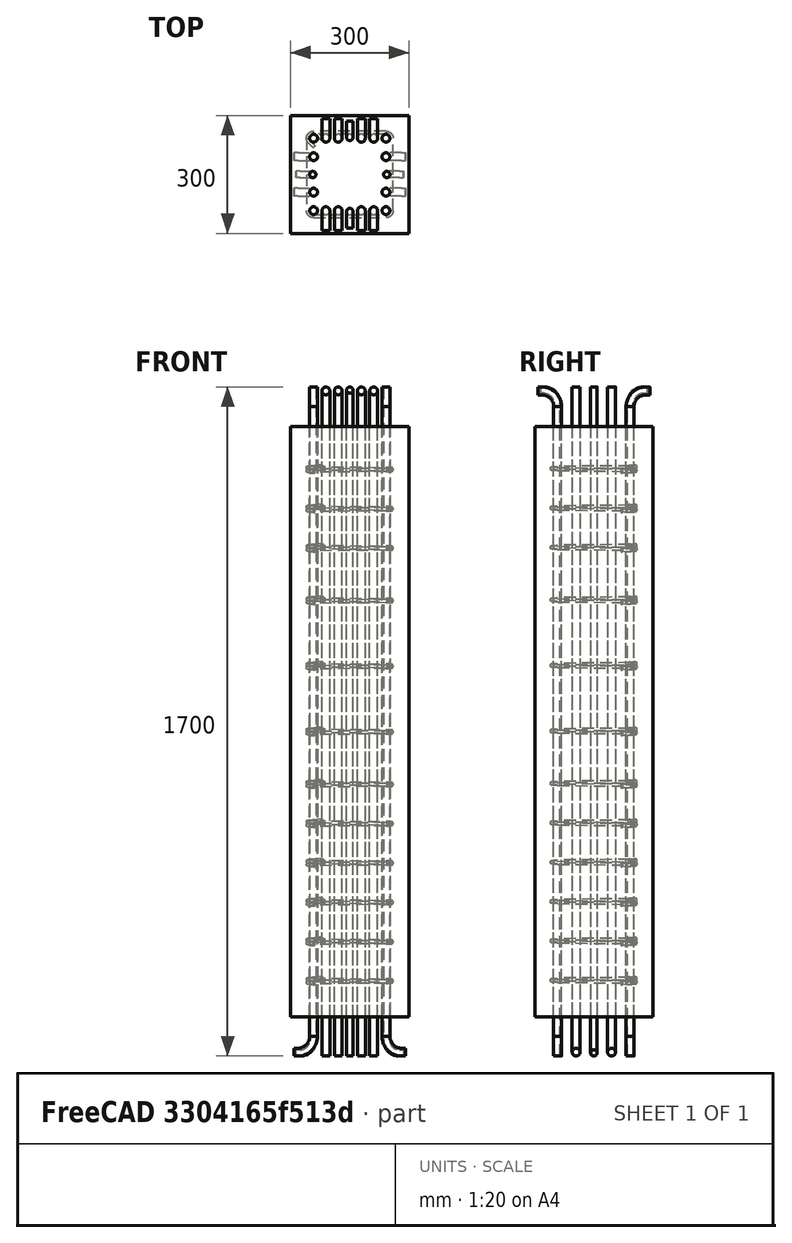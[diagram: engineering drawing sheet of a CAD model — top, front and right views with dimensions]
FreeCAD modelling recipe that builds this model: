
FCSTD DOCUMENT  (FreeCAD 0.19R20802 (Git))
Label: column_drawing_dimensioning
License: All rights reserved
LicenseURL: http://en.wikipedia.org/wiki/All_rights_reserved
objects: TechDraw::DrawViewSymbolPython×86, Part::FeaturePython×16, Sketcher::SketchObject×14, App::DocumentObjectGroupPython×6, TechDraw::DrawSVGTemplate×6, TechDraw::DrawPage×6, Part::Part2DObjectPython×1
note: 31 computed .brp shape members not serialized (recipe doc carries the construction recipe); baked Part::Feature solids carry a one-line shape summary decoded from their .brp

FEATURE [Part::FeaturePython] Structure  label="Column"  # Arch/BIM 24 (typed FeaturePython)
  FaceMaker = 0
  Height = 1500
  HorizontalArea = 90000
  IfcData = attributes={"GlobalId": {"name": "GlobalId", "type": "IfcGloballyUniqueId", "is_enum": false, "enum_values": []}, "Description": {"... (+438 chars omitted),+1 more (map truncated)
  IfcType = 24
  Length = 300
  MoveBase = false
  MoveWithHost = false
  Nodes = (2) [(5.55112e-16,1.51582e-15,0),(5.55112e-16,1.51582e-15,1500)]
  NodesOffset = 0
  Normal = (0,0,0)
  PerimeterLength = 1200
  PredefinedType = 0
  VerticalArea = 1800000
  Width = 300
FEATURE [Sketcher::SketchObject] Sketch
  MapMode = 5
  Placement = pos=(0,-150,0) rot=(1,0,0;1.5708rad)
  Support = -> [Structure]
  sketch-geometry (1):
    g0: LineSegment StartX=92 StartY=-50 StartZ=0 EndX=92 EndY=1550 EndZ=0
FEATURE [Part::FeaturePython] Rebar  label="StraightRebar"  # Arch/BIM 110 (typed FeaturePython)
  Amount = 2
  AmountCheck = true
  Base = -> Sketch
  Cover = 48
  CoverAlong = Right Side
  Diameter = 20
  Direction = (0,0,0)
  Distance = 0
  FrontCover = 48
  HorizontalArea = 0
  Host = -> Structure
  IfcType = 110
  LeftBottomCover = -50
  Length = 1600
  Mark = M
  MoveBase = false
  MoveWithHost = false
  OffsetEnd = 58
  OffsetStart = 58
  Orientation = Vertical
  PerimeterLength = 0
  PlacementList = 2 placements: [(0,58,-1.28786e-14),(0,242,-5.37348e-14)]
  RebarShape = 0
  RightTopCover = -50
  Rounding = 0
  Spacing = 184
  TotalLength = 3200
  TrueSpacing = 2
  VerticalArea = 0
FEATURE [Sketcher::SketchObject] Sketch001
  MapMode = 5
  Placement = pos=(0,-150,0) rot=(1,0,0;1.5708rad)
  Support = -> [Structure]
  sketch-geometry (1):
    g0: LineSegment StartX=-92 StartY=-50 StartZ=0 EndX=-92 EndY=1550 EndZ=0
FEATURE [Part::FeaturePython] Rebar001  label="StraightRebar001"  # Arch/BIM 110 (typed FeaturePython)
  Amount = 2
  AmountCheck = true
  Base = -> Sketch001
  Cover = 48
  CoverAlong = Left Side
  Diameter = 20
  Direction = (0,0,0)
  Distance = 0
  FrontCover = 48
  HorizontalArea = 0
  Host = -> Structure
  IfcType = 110
  LeftBottomCover = -50
  Length = 1600
  Mark = M
  MoveBase = false
  MoveWithHost = false
  OffsetEnd = 58
  OffsetStart = 58
  Orientation = Vertical
  PerimeterLength = 0
  PlacementList = 2 placements: [(0,58,-1.28786e-14),(0,242,-5.37348e-14)]
  RebarShape = 0
  RightTopCover = -50
  Rounding = 0
  Spacing = 184
  TotalLength = 3200
  TrueSpacing = 2
  VerticalArea = 0
FEATURE [Part::Part2DObjectPython] Wire  # Draft 2D object (typed FeaturePython)
  Area = 0
  ChamferSize = 0
  Closed = false
  End = (-90.5858,70.7868,1489.07)
  FilletRadius = 0
  Length = 987.335
  MakeFace = true
  Points = (7) [(-70.7868,90.5858,1502.19),(-106,125.799,1500),(-106,-106,1497.81),(106,-106,1495.63),(106,106,1493.44),(-125.799,106,1491.25),(-90.5858,70.7868,1489.07)]
  Start = (-70.7868,90.5858,1502.19)
  Subdivisions = 0
  Support = -> [Structure]
FEATURE [Part::FeaturePython] Rebar002  label="Stirrup"  # Arch/BIM 110 (typed FeaturePython)
  Amount = 12
  AmountCheck = true
  Base = -> Wire
  BentAngle = 135
  BentFactor = 2
  BottomCover = 40
  CustomSpacing = 3@100.0+3@166.66666666666666+6@100.0
  Diameter = 8
  Direction = (0,0,-1)
  Distance = 0
  FrontCover = 100
  HorizontalArea = 0
  Host = -> Structure
  IfcType = 110
  LeftCover = 40
  Length = 987.335
  Mark = Strp
  MoveBase = false
  MoveWithHost = false
  OffsetEnd = 104
  OffsetStart = 104
  PerimeterLength = 0
  PlacementList = 12 placements: [(0,0,-104),(0,0,-204),(0,0,-304),(0,0,-437.333),(0,0,-604),(0,0,-770.667),(0,0,-904),(0,0,-1004),(0,0,-1104),(0,0,-1204),(0,0,-1304),(0,0,-1404)]
  RebarShape = 3
  RightCover = 40
  Rounding = 1.75
  Spacing = 0
  TopCover = 40
  TotalLength = 11848
  TrueSpacing = 5
  VerticalArea = 0
FEATURE [App::DocumentObjectGroupPython] Ties  # scripted group (container) (typed FeaturePython)
  BottomCover = 40
  Group = -> [Rebar002]
  LeftCover = 40
  RightCover = 40
  Ties = -> [Rebar002]
  TiesConfiguration = SingleTie
  TopCover = 40
FEATURE [App::DocumentObjectGroupPython] MainRebars  # scripted group (container) (typed FeaturePython)
  BottomOffset = -50
  Group = -> [Rebar,Rebar001]
  HookExtendAlong = x-axis
  HookExtension = 40
  HookOrientation = Top Inside
  MainRebars = -> [Rebar,Rebar001]
  RebarType = StraightRebar
  TopOffset = -50
FEATURE [Sketcher::SketchObject] Sketch014
  MapMode = 5
  Placement = pos=(150,0,0) rot=(0.57735,0.57735,0.57735;2.0944rad)
  Support = -> [Structure]
  sketch-geometry (2):
    g0: LineSegment StartX=-92 StartY=-100 StartZ=0 EndX=-92 EndY=1590 EndZ=0
    g1: LineSegment StartX=-92 StartY=1590 StartZ=0 EndX=-142 EndY=1590 EndZ=0
FEATURE [Part::FeaturePython] Rebar015  label="LShapeRebar"  # Arch/BIM 110 (typed FeaturePython)
  Amount = 2
  AmountCheck = true
  Base = -> Sketch014
  BottomCover = -100
  Diameter = 20
  Direction = (0,0,0)
  Distance = 0
  FrontCover = 79.3333
  HorizontalArea = 0
  Host = -> Structure
  IfcType = 110
  LeftCover = 48
  Length = 1740
  Mark = XD
  MoveBase = false
  MoveWithHost = false
  OffsetEnd = 179.333
  OffsetStart = 89.3333
  Orientation = Top Left
  PerimeterLength = 0
  PlacementList = 2 placements: [(-89.3333,0,0),(-120.667,0,0)]
  RebarShape = 2
  RightCover = 292
  Rounding = 2
  Spacing = 31.3333
  TopCover = -100
  TotalLength = 3480
  TrueSpacing = 2
  VerticalArea = 0
FEATURE [Sketcher::SketchObject] Sketch015
  MapMode = 5
  Placement = pos=(150,0,0) rot=(0.57735,0.57735,0.57735;2.0944rad)
  Support = -> [Structure]
  sketch-geometry (2):
    g0: LineSegment StartX=-94 StartY=-100 StartZ=0 EndX=-94 EndY=1592 EndZ=0
    g1: LineSegment StartX=-94 StartY=1592 StartZ=0 EndX=-136 EndY=1592 EndZ=0
FEATURE [Part::FeaturePython] Rebar016  label="LShapeRebar001"  # Arch/BIM 110 (typed FeaturePython)
  Amount = 1
  AmountCheck = true
  Base = -> Sketch015
  BottomCover = -100
  Diameter = 16
  Direction = (0,0,0)
  Distance = 0
  FrontCover = 142
  HorizontalArea = 0
  Host = -> Structure
  IfcType = 110
  LeftCover = 48
  Length = 1734
  Mark = XD
  MoveBase = false
  MoveWithHost = false
  OffsetEnd = 150
  OffsetStart = 150
  Orientation = Top Left
  PerimeterLength = 0
  PlacementList = 1 placements: [(-150,0,0)]
  RebarShape = 2
  RightCover = 286
  Rounding = 2
  Spacing = 0
  TopCover = -100
  TotalLength = 1734
  TrueSpacing = 1
  VerticalArea = 0
FEATURE [Sketcher::SketchObject] Sketch016
  MapMode = 5
  Placement = pos=(150,0,0) rot=(0.57735,0.57735,0.57735;2.0944rad)
  Support = -> [Structure]
  sketch-geometry (2):
    g0: LineSegment StartX=-92 StartY=-100 StartZ=0 EndX=-92 EndY=1590 EndZ=0
    g1: LineSegment StartX=-92 StartY=1590 StartZ=0 EndX=-142 EndY=1590 EndZ=0
FEATURE [Part::FeaturePython] Rebar017  label="LShapeRebar002"  # Arch/BIM 110 (typed FeaturePython)
  Amount = 2
  AmountCheck = true
  Base = -> Sketch016
  BottomCover = -100
  Diameter = 20
  Direction = (0,0,0)
  Distance = 0
  FrontCover = 169.333
  HorizontalArea = 0
  Host = -> Structure
  IfcType = 110
  LeftCover = 48
  Length = 1740
  Mark = XD
  MoveBase = false
  MoveWithHost = false
  OffsetEnd = 89.3333
  OffsetStart = 179.333
  Orientation = Top Left
  PerimeterLength = 0
  PlacementList = 2 placements: [(-179.333,0,0),(-210.667,0,0)]
  RebarShape = 2
  RightCover = 292
  Rounding = 2
  Spacing = 31.3333
  TopCover = -100
  TotalLength = 3480
  TrueSpacing = 2
  VerticalArea = 0
FEATURE [Sketcher::SketchObject] Sketch017
  MapMode = 5
  Placement = pos=(150,0,0) rot=(0.57735,0.57735,0.57735;2.0944rad)
  Support = -> [Structure]
  sketch-geometry (2):
    g0: LineSegment StartX=92 StartY=-100 StartZ=0 EndX=92 EndY=1590 EndZ=0
    g1: LineSegment StartX=92 StartY=1590 StartZ=0 EndX=142 EndY=1590 EndZ=0
FEATURE [Part::FeaturePython] Rebar018  label="LShapeRebar003"  # Arch/BIM 110 (typed FeaturePython)
  Amount = 2
  AmountCheck = true
  Base = -> Sketch017
  BottomCover = -100
  Diameter = 20
  Direction = (0,0,0)
  Distance = 0
  FrontCover = 79.3333
  HorizontalArea = 0
  Host = -> Structure
  IfcType = 110
  LeftCover = 292
  Length = 1740
  Mark = XD
  MoveBase = false
  MoveWithHost = false
  OffsetEnd = 179.333
  OffsetStart = 89.3333
  Orientation = Top Right
  PerimeterLength = 0
  PlacementList = 2 placements: [(-89.3333,0,0),(-120.667,0,0)]
  RebarShape = 2
  RightCover = 48
  Rounding = 2
  Spacing = 31.3333
  TopCover = -100
  TotalLength = 3480
  TrueSpacing = 2
  VerticalArea = 0
FEATURE [Sketcher::SketchObject] Sketch018
  MapMode = 5
  Placement = pos=(150,0,0) rot=(0.57735,0.57735,0.57735;2.0944rad)
  Support = -> [Structure]
  sketch-geometry (2):
    g0: LineSegment StartX=94 StartY=-100 StartZ=0 EndX=94 EndY=1592 EndZ=0
    g1: LineSegment StartX=94 StartY=1592 StartZ=0 EndX=136 EndY=1592 EndZ=0
FEATURE [Part::FeaturePython] Rebar019  label="LShapeRebar004"  # Arch/BIM 110 (typed FeaturePython)
  Amount = 1
  AmountCheck = true
  Base = -> Sketch018
  BottomCover = -100
  Diameter = 16
  Direction = (0,0,0)
  Distance = 0
  FrontCover = 142
  HorizontalArea = 0
  Host = -> Structure
  IfcType = 110
  LeftCover = 286
  Length = 1734
  Mark = XD
  MoveBase = false
  MoveWithHost = false
  OffsetEnd = 150
  OffsetStart = 150
  Orientation = Top Right
  PerimeterLength = 0
  PlacementList = 1 placements: [(-150,0,0)]
  RebarShape = 2
  RightCover = 48
  Rounding = 2
  Spacing = 0
  TopCover = -100
  TotalLength = 1734
  TrueSpacing = 1
  VerticalArea = 0
FEATURE [Sketcher::SketchObject] Sketch019
  MapMode = 5
  Placement = pos=(150,0,0) rot=(0.57735,0.57735,0.57735;2.0944rad)
  Support = -> [Structure]
  sketch-geometry (2):
    g0: LineSegment StartX=92 StartY=-100 StartZ=0 EndX=92 EndY=1590 EndZ=0
    g1: LineSegment StartX=92 StartY=1590 StartZ=0 EndX=142 EndY=1590 EndZ=0
FEATURE [Part::FeaturePython] Rebar020  label="LShapeRebar005"  # Arch/BIM 110 (typed FeaturePython)
  Amount = 2
  AmountCheck = true
  Base = -> Sketch019
  BottomCover = -100
  Diameter = 20
  Direction = (0,0,0)
  Distance = 0
  FrontCover = 169.333
  HorizontalArea = 0
  Host = -> Structure
  IfcType = 110
  LeftCover = 292
  Length = 1740
  Mark = XD
  MoveBase = false
  MoveWithHost = false
  OffsetEnd = 89.3333
  OffsetStart = 179.333
  Orientation = Top Right
  PerimeterLength = 0
  PlacementList = 2 placements: [(-179.333,0,0),(-210.667,0,0)]
  RebarShape = 2
  RightCover = 48
  Rounding = 2
  Spacing = 31.3333
  TopCover = -100
  TotalLength = 3480
  TrueSpacing = 2
  VerticalArea = 0
FEATURE [App::DocumentObjectGroupPython] XDirRebars  # scripted group (container) (typed FeaturePython)
  BottomOffset = -100
  Group = -> [Rebar015,Rebar016,Rebar017,Rebar018,Rebar019,Rebar020]
  HookExtension = 10
  HookOrientation = Top Outside
  NumberDiameter = 2#20mm+1#16mm+2#20mm
  RebarType = LShapeRebar
  TopOffset = -100
  XDirRebars = -> [Rebar015,Rebar016,Rebar017,Rebar018,Rebar019,Rebar020]
FEATURE [Sketcher::SketchObject] Sketch020
  MapMode = 5
  Placement = pos=(0,-150,0) rot=(1,0,0;1.5708rad)
  Support = -> [Structure]
  sketch-geometry (2):
    g0: LineSegment StartX=-92 StartY=1600 StartZ=0 EndX=-92 EndY=-90 EndZ=0
    g1: LineSegment StartX=-92 StartY=-90 StartZ=0 EndX=-142 EndY=-90 EndZ=0
FEATURE [Part::FeaturePython] Rebar021  label="LShapeRebar006"  # Arch/BIM 110 (typed FeaturePython)
  Amount = 1
  AmountCheck = true
  Base = -> Sketch020
  BottomCover = -100
  Diameter = 20
  Direction = (0,0,0)
  Distance = 0
  FrontCover = 95
  HorizontalArea = 0
  Host = -> Structure
  IfcType = 110
  LeftCover = 48
  Length = 1740
  Mark = YD
  MoveBase = false
  MoveWithHost = false
  OffsetEnd = 195
  OffsetStart = 105
  Orientation = Bottom Left
  PerimeterLength = 0
  PlacementList = 1 placements: [(0,105,-2.33147e-14)]
  RebarShape = 2
  RightCover = 292
  Rounding = 2
  Spacing = 0
  TopCover = -100
  TotalLength = 1740
  TrueSpacing = 1
  VerticalArea = 0
FEATURE [Sketcher::SketchObject] Sketch021
  MapMode = 5
  Placement = pos=(0,-150,0) rot=(1,0,0;1.5708rad)
  Support = -> [Structure]
  sketch-geometry (2):
    g0: LineSegment StartX=-94 StartY=1600 StartZ=0 EndX=-94 EndY=-92 EndZ=0
    g1: LineSegment StartX=-94 StartY=-92 StartZ=0 EndX=-136 EndY=-92 EndZ=0
FEATURE [Part::FeaturePython] Rebar022  label="LShapeRebar007"  # Arch/BIM 110 (typed FeaturePython)
  Amount = 1
  AmountCheck = true
  Base = -> Sketch021
  BottomCover = -100
  Diameter = 16
  Direction = (0,0,0)
  Distance = 0
  FrontCover = 142
  HorizontalArea = 0
  Host = -> Structure
  IfcType = 110
  LeftCover = 48
  Length = 1734
  Mark = YD
  MoveBase = false
  MoveWithHost = false
  OffsetEnd = 150
  OffsetStart = 150
  Orientation = Bottom Left
  PerimeterLength = 0
  PlacementList = 1 placements: [(0,150,-3.33067e-14)]
  RebarShape = 2
  RightCover = 286
  Rounding = 2
  Spacing = 0
  TopCover = -100
  TotalLength = 1734
  TrueSpacing = 1
  VerticalArea = 0
FEATURE [Sketcher::SketchObject] Sketch022
  MapMode = 5
  Placement = pos=(0,-150,0) rot=(1,0,0;1.5708rad)
  Support = -> [Structure]
  sketch-geometry (2):
    g0: LineSegment StartX=-92 StartY=1600 StartZ=0 EndX=-92 EndY=-90 EndZ=0
    g1: LineSegment StartX=-92 StartY=-90 StartZ=0 EndX=-142 EndY=-90 EndZ=0
FEATURE [Part::FeaturePython] Rebar023  label="LShapeRebar008"  # Arch/BIM 110 (typed FeaturePython)
  Amount = 1
  AmountCheck = true
  Base = -> Sketch022
  BottomCover = -100
  Diameter = 20
  Direction = (0,0,0)
  Distance = 0
  FrontCover = 185
  HorizontalArea = 0
  Host = -> Structure
  IfcType = 110
  LeftCover = 48
  Length = 1740
  Mark = YD
  MoveBase = false
  MoveWithHost = false
  OffsetEnd = 105
  OffsetStart = 195
  Orientation = Bottom Left
  PerimeterLength = 0
  PlacementList = 1 placements: [(0,195,-4.32987e-14)]
  RebarShape = 2
  RightCover = 292
  Rounding = 2
  Spacing = 0
  TopCover = -100
  TotalLength = 1740
  TrueSpacing = 1
  VerticalArea = 0
FEATURE [Sketcher::SketchObject] Sketch023
  MapMode = 5
  Placement = pos=(0,-150,0) rot=(1,0,0;1.5708rad)
  Support = -> [Structure]
  sketch-geometry (2):
    g0: LineSegment StartX=92 StartY=1600 StartZ=0 EndX=92 EndY=-90 EndZ=0
    g1: LineSegment StartX=92 StartY=-90 StartZ=0 EndX=142 EndY=-90 EndZ=0
FEATURE [Part::FeaturePython] Rebar024  label="LShapeRebar009"  # Arch/BIM 110 (typed FeaturePython)
  Amount = 1
  AmountCheck = true
  Base = -> Sketch023
  BottomCover = -100
  Diameter = 20
  Direction = (0,0,0)
  Distance = 0
  FrontCover = 95
  HorizontalArea = 0
  Host = -> Structure
  IfcType = 110
  LeftCover = 292
  Length = 1740
  Mark = YD
  MoveBase = false
  MoveWithHost = false
  OffsetEnd = 195
  OffsetStart = 105
  Orientation = Bottom Right
  PerimeterLength = 0
  PlacementList = 1 placements: [(0,105,-2.33147e-14)]
  RebarShape = 2
  RightCover = 48
  Rounding = 2
  Spacing = 0
  TopCover = -100
  TotalLength = 1740
  TrueSpacing = 1
  VerticalArea = 0
FEATURE [Sketcher::SketchObject] Sketch024
  MapMode = 5
  Placement = pos=(0,-150,0) rot=(1,0,0;1.5708rad)
  Support = -> [Structure]
  sketch-geometry (2):
    g0: LineSegment StartX=94 StartY=1600 StartZ=0 EndX=94 EndY=-92 EndZ=0
    g1: LineSegment StartX=94 StartY=-92 StartZ=0 EndX=136 EndY=-92 EndZ=0
FEATURE [Part::FeaturePython] Rebar025  label="LShapeRebar010"  # Arch/BIM 110 (typed FeaturePython)
  Amount = 1
  AmountCheck = true
  Base = -> Sketch024
  BottomCover = -100
  Diameter = 16
  Direction = (0,0,0)
  Distance = 0
  FrontCover = 142
  HorizontalArea = 0
  Host = -> Structure
  IfcType = 110
  LeftCover = 286
  Length = 1734
  Mark = YD
  MoveBase = false
  MoveWithHost = false
  OffsetEnd = 150
  OffsetStart = 150
  Orientation = Bottom Right
  PerimeterLength = 0
  PlacementList = 1 placements: [(0,150,-3.33067e-14)]
  RebarShape = 2
  RightCover = 48
  Rounding = 2
  Spacing = 0
  TopCover = -100
  TotalLength = 1734
  TrueSpacing = 1
  VerticalArea = 0
FEATURE [Sketcher::SketchObject] Sketch025
  MapMode = 5
  Placement = pos=(0,-150,0) rot=(1,0,0;1.5708rad)
  Support = -> [Structure]
  sketch-geometry (2):
    g0: LineSegment StartX=92 StartY=1600 StartZ=0 EndX=92 EndY=-90 EndZ=0
    g1: LineSegment StartX=92 StartY=-90 StartZ=0 EndX=142 EndY=-90 EndZ=0
FEATURE [Part::FeaturePython] Rebar026  label="LShapeRebar011"  # Arch/BIM 110 (typed FeaturePython)
  Amount = 1
  AmountCheck = true
  Base = -> Sketch025
  BottomCover = -100
  Diameter = 20
  Direction = (0,0,0)
  Distance = 0
  FrontCover = 185
  HorizontalArea = 0
  Host = -> Structure
  IfcType = 110
  LeftCover = 292
  Length = 1740
  Mark = YD
  MoveBase = false
  MoveWithHost = false
  OffsetEnd = 105
  OffsetStart = 195
  Orientation = Bottom Right
  PerimeterLength = 0
  PlacementList = 1 placements: [(0,195,-4.32987e-14)]
  RebarShape = 2
  RightCover = 48
  Rounding = 2
  Spacing = 0
  TopCover = -100
  TotalLength = 1740
  TrueSpacing = 1
  VerticalArea = 0
FEATURE [App::DocumentObjectGroupPython] YDirRebars  # scripted group (container) (typed FeaturePython)
  BottomOffset = -100
  Group = -> [Rebar021,Rebar022,Rebar023,Rebar024,Rebar025,Rebar026]
  HookExtension = 10
  HookOrientation = Bottom Outside
  NumberDiameter = 1#20mm+1#16mm+1#20mm
  RebarType = LShapeRebar
  TopOffset = -100
  YDirRebars = -> [Rebar021,Rebar022,Rebar023,Rebar024,Rebar025,Rebar026]
FEATURE [App::DocumentObjectGroupPython] SecondaryRebars  # scripted group (container) (typed FeaturePython)
  Group = -> [XDirRebars,YDirRebars]
  SecondaryRebars = -> [XDirRebars,YDirRebars]
FEATURE [App::DocumentObjectGroupPython] ColumnReinforcement  # scripted group (container) (typed FeaturePython)
  ColumnType = RectangularColumn
  Group = -> [Ties,MainRebars,SecondaryRebars]
  RebarGroups = -> [Ties,MainRebars,SecondaryRebars]
FEATURE [TechDraw::DrawSVGTemplate] Template
  Height = 210
  Orientation = 1
  Width = 297
FEATURE [TechDraw::DrawViewSymbolPython] ReinforcementDrawingView  label="Front View"  # drawing view (typed FeaturePython)
  DimensionBottomOffset = 58
  DimensionLeftOffset = 16
  DimensionRightOffset = 34
  DimensionTopOffset = 10
  Height = 1700
  LeftOffset = 136.147
  LockPosition = false
  MaxHeight = 210
  MaxWidth = 297
  MinBottomOffset = 50
  MinRightOffset = 20
  PositionType = 0
  Rebars = -> [Rebar,Rebar001,Rebar002,Rebar015,Rebar016,Rebar017,Rebar018,Rebar019,Rebar020,Rebar021,Rebar022,Rebar023,Rebar024,Rebar025,Rebar026]
  RebarsColorStyle = 0
  RebarsStrokeWidth = 0.35
  Rotation = 0
  Scale = 0.0882353
  ScaleType = 1
  Structure = -> Structure
  StructureColorStyle = 0
  StructureStrokeWidth = 0.5
  Symbol = <blob: 8015 chars omitted>
  Template = -> Template
  TopOffset = 10
  View = 0
  VisibleRebars = -> [Rebar002,Rebar015,Rebar016,Rebar017,Rebar018,Rebar019,Rebar020,Rebar021,Rebar022,Rebar024,Rebar025,Rebar,Rebar001]
  Width = 300
  X = 149.382
  Y = 125
  expr: LeftOffset = .Template.Width.Value / 2 - .Width.Value * .Scale / 2
FEATURE [TechDraw::DrawViewSymbolPython] ReinforcementDimensioning  # drawing view (typed FeaturePython)
  DimensionBottomOffset = 10
  DimensionFormat = %M %C⌀%D,span=%S
  DimensionLeftOffset = 10
  DimensionRightOffset = 10
  DimensionTopOffset = 10
  Font = DejaVu Sans
  FontSize = 3
  LineEndSymbol = 0
  LineMidPointSymbol = 1
  LineStartSymbol = 3
  LineStyle = 0
  LockPosition = false
  MultiRebar_LineEndSymbol = 0
  MultiRebar_LineStartSymbol = 0
  MultiRebar_OuterDimension = true
  MultiRebar_TextPositionType = 0
  ParentDrawingView = -> ReinforcementDrawingView
  Rebar = -> Rebar002
  Rotation = 0
  Scale = 0.0882353
  ScaleType = 2
  SingleRebar_LineEndSymbol = 0
  SingleRebar_LineStartSymbol = 3
  SingleRebar_OuterDimension = false
  SingleRebar_TextPositionType = 1
  StrokeWidth = 0.25
  Symbol = <blob: 5409 chars omitted>
  TextPositionType = 0
  WayPoints = (2) [(0,0,0),(50,0,0)]
  WayPointsType = 0
  X = 149.382
  Y = 125
FEATURE [TechDraw::DrawViewSymbolPython] ReinforcementDimensioning001  # drawing view (typed FeaturePython)
  DimensionBottomOffset = 10
  DimensionFormat = %M %C⌀%D,span=%S
  DimensionLeftOffset = 10
  DimensionRightOffset = 16
  DimensionTopOffset = 10
  Font = DejaVu Sans
  FontSize = 3
  LineEndSymbol = 0
  LineMidPointSymbol = 1
  LineStartSymbol = 3
  LineStyle = 0
  LockPosition = false
  MultiRebar_LineEndSymbol = 0
  MultiRebar_LineStartSymbol = 0
  MultiRebar_OuterDimension = true
  MultiRebar_TextPositionType = 0
  ParentDrawingView = -> ReinforcementDrawingView
  Rebar = -> Rebar015
  Rotation = 0
  Scale = 0.0882353
  ScaleType = 2
  SingleRebar_LineEndSymbol = 0
  SingleRebar_LineStartSymbol = 3
  SingleRebar_OuterDimension = false
  SingleRebar_TextPositionType = 1
  StrokeWidth = 0.25
  Symbol = <svg version="1.1" xmlns="http://www.w3.org/2000/svg" xmlns:xlink="http://www.w3.org/1999/xlink" xmlns:freecad="http://www.freecadweb.org/wiki/index.php?title=Svg_Namespace" width="300.0mm" height="1700.0mm" viewBox="0 0 300.0 1700.0"><g transform="translate(150.0, 1600.0)"><g><path d="M60.66666666666667 156.6666666666667 L60.66666666666667 213.33333333333337 L29.333333333333357 213.33333333333337 L29.333333333333357 156.6666666666667" style="stroke:#00007f;stroke-width:2.833333333333333;stroke-linecap:round;fill:none;" stroke-dasharray="" /><path d="M0,0 -8,-1.5 V1.5 L0,0" style="stroke:#00007f;fill:#00007f;stroke-width:2.833333333333333;stroke-linecap:round;stroke-linejoin:bevel;" transform="translate(60.66666666666667 156.6666666666667) rotate(-90.0 0 0)" /><g id="line_mid_points"><circle cx="0" cy="0" r="5.666666666666666" fill="#00007f" transform="translate(60.66666666666667 213.33333333333337) rotate(90.0 0 0)" /><circle cx="0" cy="0" r="5.666666666666666" fill="#00007f" transform="translate(29.333333333333357 213.33333333333337) rotate(180.0 0 0)" /></g><path d="M0,0 -8,-1.5 V1.5 L0,0" style="stroke:#00007f;fill:#00007f;stroke-width:2.833333333333333;stroke-linecap:round;stroke-linejoin:bevel;" transform="translate(29.333333333333357 156.6666666666667) rotate(-90.0 0 0)" /></g><text x="45.000000000000014" y="207.6666666666667" style="white-space:pre;" fill="#005400" font-family="DejaVu Sans" font-size="34.0" text-anchor="middle" dominant-baseline="baseline" xml:space="preserve" transform="rotate(-0.0 45.000000000000014 213.33333333333337)">XD 2⌀20,span=31</text></g></svg>
  TextPositionType = 0
  WayPoints = (2) [(0,0,0),(50,0,0)]
  WayPointsType = 0
  X = 149.382
  Y = 125
FEATURE [TechDraw::DrawViewSymbolPython] ReinforcementDimensioning002  # drawing view (typed FeaturePython)
  DimensionBottomOffset = 16
  DimensionFormat = %M %C⌀%D,span=%S
  DimensionLeftOffset = 10
  DimensionRightOffset = 16
  DimensionTopOffset = 10
  Font = DejaVu Sans
  FontSize = 3
  LineEndSymbol = 0
  LineMidPointSymbol = 1
  LineStartSymbol = 3
  LineStyle = 0
  LockPosition = false
  MultiRebar_LineEndSymbol = 0
  MultiRebar_LineStartSymbol = 0
  MultiRebar_OuterDimension = true
  MultiRebar_TextPositionType = 0
  ParentDrawingView = -> ReinforcementDrawingView
  Rebar = -> Rebar016
  Rotation = 0
  Scale = 0.0882353
  ScaleType = 2
  SingleRebar_LineEndSymbol = 0
  SingleRebar_LineStartSymbol = 3
  SingleRebar_OuterDimension = false
  SingleRebar_TextPositionType = 1
  StrokeWidth = 0.25
  Symbol = <svg version="1.1" xmlns="http://www.w3.org/2000/svg" xmlns:xlink="http://www.w3.org/1999/xlink" xmlns:freecad="http://www.freecadweb.org/wiki/index.php?title=Svg_Namespace" width="300.0mm" height="1700.0mm" viewBox="0 0 300.0 1700.0"><g transform="translate(150.0, 1600.0)"><g><path d="M331.3333333333333 -870.0 L0.0 -870.0" style="stroke:#00007f;stroke-width:2.833333333333333;stroke-linecap:round;fill:none;" stroke-dasharray="" /><g id="line_mid_points" /><path d="M0,0 -8,-1.5 V1.5 L0,0" style="stroke:#00007f;fill:#00007f;stroke-width:2.833333333333333;stroke-linecap:round;stroke-linejoin:bevel;" transform="translate(0.0 -870.0) rotate(180.0 0 0)" /></g><text x="331.3333333333333" y="-853.0" style="white-space:pre;" fill="#005400" font-family="DejaVu Sans" font-size="34.0" text-anchor="start" dominant-baseline="baseline" xml:space="preserve">XD 1⌀16,span=0</text></g></svg>
  TextPositionType = 0
  WayPoints = (2) [(0,0,0),(50,0,0)]
  WayPointsType = 0
  X = 149.382
  Y = 125
FEATURE [TechDraw::DrawViewSymbolPython] ReinforcementDimensioning003  # drawing view (typed FeaturePython)
  DimensionBottomOffset = 16
  DimensionFormat = %M %C⌀%D,span=%S
  DimensionLeftOffset = 10
  DimensionRightOffset = 22
  DimensionTopOffset = 10
  Font = DejaVu Sans
  FontSize = 3
  LineEndSymbol = 0
  LineMidPointSymbol = 1
  LineStartSymbol = 3
  LineStyle = 0
  LockPosition = false
  MultiRebar_LineEndSymbol = 0
  MultiRebar_LineStartSymbol = 0
  MultiRebar_OuterDimension = true
  MultiRebar_TextPositionType = 0
  ParentDrawingView = -> ReinforcementDrawingView
  Rebar = -> Rebar017
  Rotation = 0
  Scale = 0.0882353
  ScaleType = 2
  SingleRebar_LineEndSymbol = 0
  SingleRebar_LineStartSymbol = 3
  SingleRebar_OuterDimension = false
  SingleRebar_TextPositionType = 1
  StrokeWidth = 0.25
  Symbol = <svg version="1.1" xmlns="http://www.w3.org/2000/svg" xmlns:xlink="http://www.w3.org/1999/xlink" xmlns:freecad="http://www.freecadweb.org/wiki/index.php?title=Svg_Namespace" width="300.0mm" height="1700.0mm" viewBox="0 0 300.0 1700.0"><g transform="translate(150.0, 1600.0)"><g><path d="M-29.333333333333343 224.6666666666667 L-29.333333333333343 281.33333333333337 L-60.66666666666666 281.33333333333337 L-60.66666666666666 224.6666666666667" style="stroke:#00007f;stroke-width:2.833333333333333;stroke-linecap:round;fill:none;" stroke-dasharray="" /><path d="M0,0 -8,-1.5 V1.5 L0,0" style="stroke:#00007f;fill:#00007f;stroke-width:2.833333333333333;stroke-linecap:round;stroke-linejoin:bevel;" transform="translate(-29.333333333333343 224.6666666666667) rotate(-90.0 0 0)" /><g id="line_mid_points"><circle cx="0" cy="0" r="5.666666666666666" fill="#00007f" transform="translate(-29.333333333333343 281.33333333333337) rotate(90.0 0 0)" /><circle cx="0" cy="0" r="5.666666666666666" fill="#00007f" transform="translate(-60.66666666666666 281.33333333333337) rotate(180.0 0 0)" /></g><path d="M0,0 -8,-1.5 V1.5 L0,0" style="stroke:#00007f;fill:#00007f;stroke-width:2.833333333333333;stroke-linecap:round;stroke-linejoin:bevel;" transform="translate(-60.66666666666666 224.6666666666667) rotate(-90.0 0 0)" /></g><text x="-45.0" y="275.6666666666667" style="white-space:pre;" fill="#005400" font-family="DejaVu Sans" font-size="34.0" text-anchor="middle" dominant-baseline="baseline" xml:space="preserve" transform="rotate(-0.0 -45.0 281.33333333333337)">XD 2⌀20,span=31</text></g></svg>
  TextPositionType = 0
  WayPoints = (2) [(0,0,0),(50,0,0)]
  WayPointsType = 0
  X = 149.382
  Y = 125
FEATURE [TechDraw::DrawViewSymbolPython] ReinforcementDimensioning004  # drawing view (typed FeaturePython)
  DimensionBottomOffset = 22
  DimensionFormat = %M %C⌀%D,span=%S
  DimensionLeftOffset = 10
  DimensionRightOffset = 22
  DimensionTopOffset = 10
  Font = DejaVu Sans
  FontSize = 3
  LineEndSymbol = 0
  LineMidPointSymbol = 1
  LineStartSymbol = 3
  LineStyle = 0
  LockPosition = false
  MultiRebar_LineEndSymbol = 0
  MultiRebar_LineStartSymbol = 0
  MultiRebar_OuterDimension = true
  MultiRebar_TextPositionType = 0
  ParentDrawingView = -> ReinforcementDrawingView
  Rebar = -> Rebar018
  Rotation = 0
  Scale = 0.0882353
  ScaleType = 2
  SingleRebar_LineEndSymbol = 0
  SingleRebar_LineStartSymbol = 3
  SingleRebar_OuterDimension = false
  SingleRebar_TextPositionType = 1
  StrokeWidth = 0.25
  Symbol = <svg version="1.1" xmlns="http://www.w3.org/2000/svg" xmlns:xlink="http://www.w3.org/1999/xlink" xmlns:freecad="http://www.freecadweb.org/wiki/index.php?title=Svg_Namespace" width="300.0mm" height="1700.0mm" viewBox="0 0 300.0 1700.0"><g transform="translate(150.0, 1600.0)"><g><path d="M60.66666666666667 292.6666666666667 L60.66666666666667 349.33333333333337 L29.333333333333357 349.33333333333337 L29.333333333333357 292.6666666666667" style="stroke:#00007f;stroke-width:2.833333333333333;stroke-linecap:round;fill:none;" stroke-dasharray="" /><path d="M0,0 -8,-1.5 V1.5 L0,0" style="stroke:#00007f;fill:#00007f;stroke-width:2.833333333333333;stroke-linecap:round;stroke-linejoin:bevel;" transform="translate(60.66666666666667 292.6666666666667) rotate(-90.0 0 0)" /><g id="line_mid_points"><circle cx="0" cy="0" r="5.666666666666666" fill="#00007f" transform="translate(60.66666666666667 349.33333333333337) rotate(90.0 0 0)" /><circle cx="0" cy="0" r="5.666666666666666" fill="#00007f" transform="translate(29.333333333333357 349.33333333333337) rotate(180.0 0 0)" /></g><path d="M0,0 -8,-1.5 V1.5 L0,0" style="stroke:#00007f;fill:#00007f;stroke-width:2.833333333333333;stroke-linecap:round;stroke-linejoin:bevel;" transform="translate(29.333333333333357 292.6666666666667) rotate(-90.0 0 0)" /></g><text x="45.000000000000014" y="343.6666666666667" style="white-space:pre;" fill="#005400" font-family="DejaVu Sans" font-size="34.0" text-anchor="middle" dominant-baseline="baseline" xml:space="preserve" transform="rotate(-0.0 45.000000000000014 349.33333333333337)">XD 2⌀20,span=31</text></g></svg>
  TextPositionType = 0
  WayPoints = (2) [(0,0,0),(50,0,0)]
  WayPointsType = 0
  X = 149.382
  Y = 125
FEATURE [TechDraw::DrawViewSymbolPython] ReinforcementDimensioning005  # drawing view (typed FeaturePython)
  DimensionBottomOffset = 28
  DimensionFormat = %M %C⌀%D,span=%S
  DimensionLeftOffset = 10
  DimensionRightOffset = 22
  DimensionTopOffset = 10
  Font = DejaVu Sans
  FontSize = 3
  LineEndSymbol = 0
  LineMidPointSymbol = 1
  LineStartSymbol = 3
  LineStyle = 0
  LockPosition = false
  MultiRebar_LineEndSymbol = 0
  MultiRebar_LineStartSymbol = 0
  MultiRebar_OuterDimension = true
  MultiRebar_TextPositionType = 0
  ParentDrawingView = -> ReinforcementDrawingView
  Rebar = -> Rebar019
  Rotation = 0
  Scale = 0.0882353
  ScaleType = 2
  SingleRebar_LineEndSymbol = 0
  SingleRebar_LineStartSymbol = 3
  SingleRebar_OuterDimension = false
  SingleRebar_TextPositionType = 1
  StrokeWidth = 0.25
  Symbol = <svg version="1.1" xmlns="http://www.w3.org/2000/svg" xmlns:xlink="http://www.w3.org/1999/xlink" xmlns:freecad="http://www.freecadweb.org/wiki/index.php?title=Svg_Namespace" width="300.0mm" height="1700.0mm" viewBox="0 0 300.0 1700.0"><g transform="translate(150.0, 1600.0)"><g><path d="M399.3333333333333 -161.0 L0.0 -161.0" style="stroke:#00007f;stroke-width:2.833333333333333;stroke-linecap:round;fill:none;" stroke-dasharray="" /><g id="line_mid_points" /><path d="M0,0 -8,-1.5 V1.5 L0,0" style="stroke:#00007f;fill:#00007f;stroke-width:2.833333333333333;stroke-linecap:round;stroke-linejoin:bevel;" transform="translate(0.0 -161.0) rotate(180.0 0 0)" /></g><text x="399.3333333333333" y="-144.0" style="white-space:pre;" fill="#005400" font-family="DejaVu Sans" font-size="34.0" text-anchor="start" dominant-baseline="baseline" xml:space="preserve">XD 1⌀16,span=0</text></g></svg>
  TextPositionType = 0
  WayPoints = (2) [(0,0,0),(50,0,0)]
  WayPointsType = 0
  X = 149.382
  Y = 125
FEATURE [TechDraw::DrawViewSymbolPython] ReinforcementDimensioning006  # drawing view (typed FeaturePython)
  DimensionBottomOffset = 28
  DimensionFormat = %M %C⌀%D,span=%S
  DimensionLeftOffset = 10
  DimensionRightOffset = 28
  DimensionTopOffset = 10
  Font = DejaVu Sans
  FontSize = 3
  LineEndSymbol = 0
  LineMidPointSymbol = 1
  LineStartSymbol = 3
  LineStyle = 0
  LockPosition = false
  MultiRebar_LineEndSymbol = 0
  MultiRebar_LineStartSymbol = 0
  MultiRebar_OuterDimension = true
  MultiRebar_TextPositionType = 0
  ParentDrawingView = -> ReinforcementDrawingView
  Rebar = -> Rebar020
  Rotation = 0
  Scale = 0.0882353
  ScaleType = 2
  SingleRebar_LineEndSymbol = 0
  SingleRebar_LineStartSymbol = 3
  SingleRebar_OuterDimension = false
  SingleRebar_TextPositionType = 1
  StrokeWidth = 0.25
  Symbol = <svg version="1.1" xmlns="http://www.w3.org/2000/svg" xmlns:xlink="http://www.w3.org/1999/xlink" xmlns:freecad="http://www.freecadweb.org/wiki/index.php?title=Svg_Namespace" width="300.0mm" height="1700.0mm" viewBox="0 0 300.0 1700.0"><g transform="translate(150.0, 1600.0)"><g><path d="M-29.333333333333343 360.6666666666667 L-29.333333333333343 417.33333333333337 L-60.66666666666666 417.33333333333337 L-60.66666666666666 360.6666666666667" style="stroke:#00007f;stroke-width:2.833333333333333;stroke-linecap:round;fill:none;" stroke-dasharray="" /><path d="M0,0 -8,-1.5 V1.5 L0,0" style="stroke:#00007f;fill:#00007f;stroke-width:2.833333333333333;stroke-linecap:round;stroke-linejoin:bevel;" transform="translate(-29.333333333333343 360.6666666666667) rotate(-90.0 0 0)" /><g id="line_mid_points"><circle cx="0" cy="0" r="5.666666666666666" fill="#00007f" transform="translate(-29.333333333333343 417.33333333333337) rotate(90.0 0 0)" /><circle cx="0" cy="0" r="5.666666666666666" fill="#00007f" transform="translate(-60.66666666666666 417.33333333333337) rotate(180.0 0 0)" /></g><path d="M0,0 -8,-1.5 V1.5 L0,0" style="stroke:#00007f;fill:#00007f;stroke-width:2.833333333333333;stroke-linecap:round;stroke-linejoin:bevel;" transform="translate(-60.66666666666666 360.6666666666667) rotate(-90.0 0 0)" /></g><text x="-45.0" y="411.6666666666667" style="white-space:pre;" fill="#005400" font-family="DejaVu Sans" font-size="34.0" text-anchor="middle" dominant-baseline="baseline" xml:space="preserve" transform="rotate(-0.0 -45.0 417.33333333333337)">XD 2⌀20,span=31</text></g></svg>
  TextPositionType = 0
  WayPoints = (2) [(0,0,0),(50,0,0)]
  WayPointsType = 0
  X = 149.382
  Y = 125
FEATURE [TechDraw::DrawViewSymbolPython] ReinforcementDimensioning007  # drawing view (typed FeaturePython)
  DimensionBottomOffset = 34
  DimensionFormat = %M %C⌀%D,span=%S
  DimensionLeftOffset = 10
  DimensionRightOffset = 28
  DimensionTopOffset = 10
  Font = DejaVu Sans
  FontSize = 3
  LineEndSymbol = 0
  LineMidPointSymbol = 1
  LineStartSymbol = 3
  LineStyle = 0
  LockPosition = false
  MultiRebar_LineEndSymbol = 0
  MultiRebar_LineStartSymbol = 0
  MultiRebar_OuterDimension = true
  MultiRebar_TextPositionType = 0
  ParentDrawingView = -> ReinforcementDrawingView
  Rebar = -> Rebar021
  Rotation = 0
  Scale = 0.0882353
  ScaleType = 2
  SingleRebar_LineEndSymbol = 0
  SingleRebar_LineStartSymbol = 3
  SingleRebar_OuterDimension = false
  SingleRebar_TextPositionType = 1
  StrokeWidth = 0.25
  Symbol = <svg version="1.1" xmlns="http://www.w3.org/2000/svg" xmlns:xlink="http://www.w3.org/1999/xlink" xmlns:freecad="http://www.freecadweb.org/wiki/index.php?title=Svg_Namespace" width="300.0mm" height="1700.0mm" viewBox="0 0 300.0 1700.0"><g transform="translate(150.0, 1600.0)"><g><path d="M-95.0 485.33333333333337 L-95.0 90.00000000000003" style="stroke:#00007f;stroke-width:2.833333333333333;stroke-linecap:round;fill:none;" stroke-dasharray="" /><g id="line_mid_points" /><path d="M0,0 -8,-1.5 V1.5 L0,0" style="stroke:#00007f;fill:#00007f;stroke-width:2.833333333333333;stroke-linecap:round;stroke-linejoin:bevel;" transform="translate(-95.0 90.00000000000003) rotate(-90.0 0 0)" /></g><text x="-95.0" y="502.33333333333337" style="white-space:pre;" fill="#005400" font-family="DejaVu Sans" font-size="34.0" text-anchor="middle" dominant-baseline="baseline" xml:space="preserve">YD 1⌀20,span=0</text></g></svg>
  TextPositionType = 0
  WayPoints = (2) [(0,0,0),(50,0,0)]
  WayPointsType = 0
  X = 149.382
  Y = 125
FEATURE [TechDraw::DrawViewSymbolPython] ReinforcementDimensioning008  # drawing view (typed FeaturePython)
  DimensionBottomOffset = 40
  DimensionFormat = %M %C⌀%D,span=%S
  DimensionLeftOffset = 10
  DimensionRightOffset = 28
  DimensionTopOffset = 10
  Font = DejaVu Sans
  FontSize = 3
  LineEndSymbol = 0
  LineMidPointSymbol = 1
  LineStartSymbol = 3
  LineStyle = 0
  LockPosition = false
  MultiRebar_LineEndSymbol = 0
  MultiRebar_LineStartSymbol = 0
  MultiRebar_OuterDimension = true
  MultiRebar_TextPositionType = 0
  ParentDrawingView = -> ReinforcementDrawingView
  Rebar = -> Rebar022
  Rotation = 0
  Scale = 0.0882353
  ScaleType = 2
  SingleRebar_LineEndSymbol = 0
  SingleRebar_LineStartSymbol = 3
  SingleRebar_OuterDimension = false
  SingleRebar_TextPositionType = 1
  StrokeWidth = 0.25
  Symbol = <svg version="1.1" xmlns="http://www.w3.org/2000/svg" xmlns:xlink="http://www.w3.org/1999/xlink" xmlns:freecad="http://www.freecadweb.org/wiki/index.php?title=Svg_Namespace" width="300.0mm" height="1700.0mm" viewBox="0 0 300.0 1700.0"><g transform="translate(150.0, 1600.0)"><g><path d="M-110.0 553.3333333333334 L-110.0 92.00000000000003" style="stroke:#00007f;stroke-width:2.833333333333333;stroke-linecap:round;fill:none;" stroke-dasharray="" /><g id="line_mid_points" /><path d="M0,0 -8,-1.5 V1.5 L0,0" style="stroke:#00007f;fill:#00007f;stroke-width:2.833333333333333;stroke-linecap:round;stroke-linejoin:bevel;" transform="translate(-110.0 92.00000000000003) rotate(-90.0 0 0)" /></g><text x="-110.0" y="570.3333333333334" style="white-space:pre;" fill="#005400" font-family="DejaVu Sans" font-size="34.0" text-anchor="middle" dominant-baseline="baseline" xml:space="preserve">YD 1⌀16,span=0</text></g></svg>
  TextPositionType = 0
  WayPoints = (2) [(0,0,0),(50,0,0)]
  WayPointsType = 0
  X = 149.382
  Y = 125
FEATURE [TechDraw::DrawViewSymbolPython] ReinforcementDimensioning009  # drawing view (typed FeaturePython)
  DimensionBottomOffset = 46
  DimensionFormat = %M %C⌀%D,span=%S
  DimensionLeftOffset = 10
  DimensionRightOffset = 28
  DimensionTopOffset = 10
  Font = DejaVu Sans
  FontSize = 3
  LineEndSymbol = 0
  LineMidPointSymbol = 1
  LineStartSymbol = 3
  LineStyle = 0
  LockPosition = false
  MultiRebar_LineEndSymbol = 0
  MultiRebar_LineStartSymbol = 0
  MultiRebar_OuterDimension = true
  MultiRebar_TextPositionType = 0
  ParentDrawingView = -> ReinforcementDrawingView
  Rebar = -> Rebar024
  Rotation = 0
  Scale = 0.0882353
  ScaleType = 2
  SingleRebar_LineEndSymbol = 0
  SingleRebar_LineStartSymbol = 3
  SingleRebar_OuterDimension = false
  SingleRebar_TextPositionType = 1
  StrokeWidth = 0.25
  Symbol = <svg version="1.1" xmlns="http://www.w3.org/2000/svg" xmlns:xlink="http://www.w3.org/1999/xlink" xmlns:freecad="http://www.freecadweb.org/wiki/index.php?title=Svg_Namespace" width="300.0mm" height="1700.0mm" viewBox="0 0 300.0 1700.0"><g transform="translate(150.0, 1600.0)"><g><path d="M92.0 621.3333333333333 L92.0 90.00000000000003" style="stroke:#00007f;stroke-width:2.833333333333333;stroke-linecap:round;fill:none;" stroke-dasharray="" /><g id="line_mid_points" /><path d="M0,0 -8,-1.5 V1.5 L0,0" style="stroke:#00007f;fill:#00007f;stroke-width:2.833333333333333;stroke-linecap:round;stroke-linejoin:bevel;" transform="translate(92.0 90.00000000000003) rotate(-90.0 0 0)" /></g><text x="92.0" y="638.3333333333333" style="white-space:pre;" fill="#005400" font-family="DejaVu Sans" font-size="34.0" text-anchor="middle" dominant-baseline="baseline" xml:space="preserve">YD 1⌀20,span=0</text></g></svg>
  TextPositionType = 0
  WayPoints = (2) [(0,0,0),(50,0,0)]
  WayPointsType = 0
  X = 149.382
  Y = 125
FEATURE [TechDraw::DrawViewSymbolPython] ReinforcementDimensioning010  # drawing view (typed FeaturePython)
  DimensionBottomOffset = 52
  DimensionFormat = %M %C⌀%D,span=%S
  DimensionLeftOffset = 10
  DimensionRightOffset = 28
  DimensionTopOffset = 10
  Font = DejaVu Sans
  FontSize = 3
  LineEndSymbol = 0
  LineMidPointSymbol = 1
  LineStartSymbol = 3
  LineStyle = 0
  LockPosition = false
  MultiRebar_LineEndSymbol = 0
  MultiRebar_LineStartSymbol = 0
  MultiRebar_OuterDimension = true
  MultiRebar_TextPositionType = 0
  ParentDrawingView = -> ReinforcementDrawingView
  Rebar = -> Rebar025
  Rotation = 0
  Scale = 0.0882353
  ScaleType = 2
  SingleRebar_LineEndSymbol = 0
  SingleRebar_LineStartSymbol = 3
  SingleRebar_OuterDimension = false
  SingleRebar_TextPositionType = 1
  StrokeWidth = 0.25
  Symbol = <svg version="1.1" xmlns="http://www.w3.org/2000/svg" xmlns:xlink="http://www.w3.org/1999/xlink" xmlns:freecad="http://www.freecadweb.org/wiki/index.php?title=Svg_Namespace" width="300.0mm" height="1700.0mm" viewBox="0 0 300.0 1700.0"><g transform="translate(150.0, 1600.0)"><g><path d="M99.0 689.3333333333333 L99.0 92.00000000000003" style="stroke:#00007f;stroke-width:2.833333333333333;stroke-linecap:round;fill:none;" stroke-dasharray="" /><g id="line_mid_points" /><path d="M0,0 -8,-1.5 V1.5 L0,0" style="stroke:#00007f;fill:#00007f;stroke-width:2.833333333333333;stroke-linecap:round;stroke-linejoin:bevel;" transform="translate(99.0 92.00000000000003) rotate(-90.0 0 0)" /></g><text x="99.0" y="706.3333333333333" style="white-space:pre;" fill="#005400" font-family="DejaVu Sans" font-size="34.0" text-anchor="middle" dominant-baseline="baseline" xml:space="preserve">YD 1⌀16,span=0</text></g></svg>
  TextPositionType = 0
  WayPoints = (2) [(0,0,0),(50,0,0)]
  WayPointsType = 0
  X = 149.382
  Y = 125
FEATURE [TechDraw::DrawViewSymbolPython] ReinforcementDimensioning011  # drawing view (typed FeaturePython)
  DimensionBottomOffset = 58
  DimensionFormat = %M %C⌀%D,span=%S
  DimensionLeftOffset = 10
  DimensionRightOffset = 28
  DimensionTopOffset = 10
  Font = DejaVu Sans
  FontSize = 3
  LineEndSymbol = 0
  LineMidPointSymbol = 1
  LineStartSymbol = 3
  LineStyle = 0
  LockPosition = false
  MultiRebar_LineEndSymbol = 0
  MultiRebar_LineStartSymbol = 0
  MultiRebar_OuterDimension = true
  MultiRebar_TextPositionType = 0
  ParentDrawingView = -> ReinforcementDrawingView
  Rebar = -> Rebar
  Rotation = 0
  Scale = 0.0882353
  ScaleType = 2
  SingleRebar_LineEndSymbol = 0
  SingleRebar_LineStartSymbol = 3
  SingleRebar_OuterDimension = false
  SingleRebar_TextPositionType = 1
  StrokeWidth = 0.25
  Symbol = <svg version="1.1" xmlns="http://www.w3.org/2000/svg" xmlns:xlink="http://www.w3.org/1999/xlink" xmlns:freecad="http://www.freecadweb.org/wiki/index.php?title=Svg_Namespace" width="300.0mm" height="1700.0mm" viewBox="0 0 300.0 1700.0"><g transform="translate(150.0, 1600.0)"><g><path d="M467.3333333333333 -215.0 L92.0 -215.0" style="stroke:#00007f;stroke-width:2.833333333333333;stroke-linecap:round;fill:none;" stroke-dasharray="" /><g id="line_mid_points" /><path d="M0,0 -8,-1.5 V1.5 L0,0" style="stroke:#00007f;fill:#00007f;stroke-width:2.833333333333333;stroke-linecap:round;stroke-linejoin:bevel;" transform="translate(92.0 -215.0) rotate(180.0 0 0)" /></g><text x="467.3333333333333" y="-198.0" style="white-space:pre;" fill="#005400" font-family="DejaVu Sans" font-size="34.0" text-anchor="start" dominant-baseline="baseline" xml:space="preserve">M 2⌀20,span=184</text></g></svg>
  TextPositionType = 0
  WayPoints = (2) [(0,0,0),(50,0,0)]
  WayPointsType = 0
  X = 149.382
  Y = 125
FEATURE [TechDraw::DrawViewSymbolPython] ReinforcementDimensioning012  # drawing view (typed FeaturePython)
  DimensionBottomOffset = 58
  DimensionFormat = %M %C⌀%D,span=%S
  DimensionLeftOffset = 10
  DimensionRightOffset = 34
  DimensionTopOffset = 10
  Font = DejaVu Sans
  FontSize = 3
  LineEndSymbol = 0
  LineMidPointSymbol = 1
  LineStartSymbol = 3
  LineStyle = 0
  LockPosition = false
  MultiRebar_LineEndSymbol = 0
  MultiRebar_LineStartSymbol = 0
  MultiRebar_OuterDimension = true
  MultiRebar_TextPositionType = 0
  ParentDrawingView = -> ReinforcementDrawingView
  Rebar = -> Rebar001
  Rotation = 0
  Scale = 0.0882353
  ScaleType = 2
  SingleRebar_LineEndSymbol = 0
  SingleRebar_LineStartSymbol = 3
  SingleRebar_OuterDimension = false
  SingleRebar_TextPositionType = 1
  StrokeWidth = 0.25
  Symbol = <svg version="1.1" xmlns="http://www.w3.org/2000/svg" xmlns:xlink="http://www.w3.org/1999/xlink" xmlns:freecad="http://www.freecadweb.org/wiki/index.php?title=Svg_Namespace" width="300.0mm" height="1700.0mm" viewBox="0 0 300.0 1700.0"><g transform="translate(150.0, 1600.0)"><g><path d="M-263.3333333333333 -751.0 L-92.0 -751.0" style="stroke:#00007f;stroke-width:2.833333333333333;stroke-linecap:round;fill:none;" stroke-dasharray="" /><g id="line_mid_points" /><path d="M0,0 -8,-1.5 V1.5 L0,0" style="stroke:#00007f;fill:#00007f;stroke-width:2.833333333333333;stroke-linecap:round;stroke-linejoin:bevel;" transform="translate(-92.0 -751.0) rotate(0.0 0 0)" /></g><text x="-263.3333333333333" y="-734.0" style="white-space:pre;" fill="#005400" font-family="DejaVu Sans" font-size="34.0" text-anchor="end" dominant-baseline="baseline" xml:space="preserve">M 2⌀20,span=184</text></g></svg>
  TextPositionType = 0
  WayPoints = (2) [(0,0,0),(50,0,0)]
  WayPointsType = 0
  X = 149.382
  Y = 125
FEATURE [TechDraw::DrawPage] TechDraw__DrawPage  label="Column Drawing"
  KeepUpdated = true
  NextBalloonIndex = 1
  ProjectionType = 0
  Template = -> Template
  Views = -> [ReinforcementDrawingView,ReinforcementDimensioning,ReinforcementDimensioning001,ReinforcementDimensioning002,ReinforcementDimensioning003,ReinforcementDimensioning004,ReinforcementDimensioning005,ReinforcementDimensioning006,ReinforcementDimensioning007,ReinforcementDimensioning008,ReinforcementDimensioning009,ReinforcementDimensioning010,ReinforcementDimensioning011,ReinforcementDimensioning012]
FEATURE [TechDraw::DrawSVGTemplate] Template001
  Height = 210
  Orientation = 1
  Width = 297
FEATURE [TechDraw::DrawViewSymbolPython] ReinforcementDrawingView001  label="Rear View"  # drawing view (typed FeaturePython)
  DimensionBottomOffset = 58
  DimensionLeftOffset = 16
  DimensionRightOffset = 34
  DimensionTopOffset = 10
  Height = 1700
  LeftOffset = 134.382
  LockPosition = false
  MaxHeight = 210
  MaxWidth = 297
  MinBottomOffset = 50
  MinRightOffset = 20
  PositionType = 0
  Rebars = -> [Rebar,Rebar001,Rebar002,Rebar015,Rebar016,Rebar017,Rebar018,Rebar019,Rebar020,Rebar021,Rebar022,Rebar023,Rebar024,Rebar025,Rebar026]
  RebarsColorStyle = 0
  RebarsStrokeWidth = 0.35
  Rotation = 0
  Scale = 0.0882353
  ScaleType = 1
  Structure = -> Structure
  StructureColorStyle = 0
  StructureStrokeWidth = 0.5
  Symbol = <blob: 8015 chars omitted>
  Template = -> Template001
  TopOffset = 10
  View = 1
  VisibleRebars = -> [Rebar002,Rebar015,Rebar016,Rebar017,Rebar018,Rebar019,Rebar020,Rebar021,Rebar022,Rebar024,Rebar025,Rebar,Rebar001]
  Width = 300
  X = 147.618
  Y = 125
  expr: LeftOffset = .Template.Width.Value / 2 - .Width.Value * .Scale / 2
FEATURE [TechDraw::DrawViewSymbolPython] ReinforcementDimensioning013  # drawing view (typed FeaturePython)
  DimensionBottomOffset = 10
  DimensionFormat = %M %C⌀%D,span=%S
  DimensionLeftOffset = 10
  DimensionRightOffset = 10
  DimensionTopOffset = 10
  Font = DejaVu Sans
  FontSize = 3
  LineEndSymbol = 0
  LineMidPointSymbol = 1
  LineStartSymbol = 3
  LineStyle = 0
  LockPosition = false
  MultiRebar_LineEndSymbol = 0
  MultiRebar_LineStartSymbol = 0
  MultiRebar_OuterDimension = true
  MultiRebar_TextPositionType = 0
  ParentDrawingView = -> ReinforcementDrawingView001
  Rebar = -> Rebar002
  Rotation = 0
  Scale = 0.0882353
  ScaleType = 2
  SingleRebar_LineEndSymbol = 0
  SingleRebar_LineStartSymbol = 3
  SingleRebar_OuterDimension = false
  SingleRebar_TextPositionType = 1
  StrokeWidth = 0.25
  Symbol = <blob: 5409 chars omitted>
  TextPositionType = 0
  WayPoints = (2) [(0,0,0),(50,0,0)]
  WayPointsType = 0
  X = 147.618
  Y = 125
FEATURE [TechDraw::DrawViewSymbolPython] ReinforcementDimensioning014  # drawing view (typed FeaturePython)
  DimensionBottomOffset = 10
  DimensionFormat = %M %C⌀%D,span=%S
  DimensionLeftOffset = 10
  DimensionRightOffset = 16
  DimensionTopOffset = 10
  Font = DejaVu Sans
  FontSize = 3
  LineEndSymbol = 0
  LineMidPointSymbol = 1
  LineStartSymbol = 3
  LineStyle = 0
  LockPosition = false
  MultiRebar_LineEndSymbol = 0
  MultiRebar_LineStartSymbol = 0
  MultiRebar_OuterDimension = true
  MultiRebar_TextPositionType = 0
  ParentDrawingView = -> ReinforcementDrawingView001
  Rebar = -> Rebar015
  Rotation = 0
  Scale = 0.0882353
  ScaleType = 2
  SingleRebar_LineEndSymbol = 0
  SingleRebar_LineStartSymbol = 3
  SingleRebar_OuterDimension = false
  SingleRebar_TextPositionType = 1
  StrokeWidth = 0.25
  Symbol = <svg version="1.1" xmlns="http://www.w3.org/2000/svg" xmlns:xlink="http://www.w3.org/1999/xlink" xmlns:freecad="http://www.freecadweb.org/wiki/index.php?title=Svg_Namespace" width="300.0mm" height="1700.0mm" viewBox="0 0 300.0 1700.0"><g transform="translate(150.0, 1600.0)"><g><path d="M-60.66666666666667 156.6666666666667 L-60.66666666666667 213.33333333333337 L-29.333333333333357 213.33333333333337 L-29.333333333333357 156.6666666666667" style="stroke:#00007f;stroke-width:2.833333333333333;stroke-linecap:round;fill:none;" stroke-dasharray="" /><path d="M0,0 -8,-1.5 V1.5 L0,0" style="stroke:#00007f;fill:#00007f;stroke-width:2.833333333333333;stroke-linecap:round;stroke-linejoin:bevel;" transform="translate(-60.66666666666667 156.6666666666667) rotate(-90.0 0 0)" /><g id="line_mid_points"><circle cx="0" cy="0" r="5.666666666666666" fill="#00007f" transform="translate(-60.66666666666667 213.33333333333337) rotate(90.0 0 0)" /><circle cx="0" cy="0" r="5.666666666666666" fill="#00007f" transform="translate(-29.333333333333357 213.33333333333337) rotate(0.0 0 0)" /></g><path d="M0,0 -8,-1.5 V1.5 L0,0" style="stroke:#00007f;fill:#00007f;stroke-width:2.833333333333333;stroke-linecap:round;stroke-linejoin:bevel;" transform="translate(-29.333333333333357 156.6666666666667) rotate(-90.0 0 0)" /></g><text x="-45.000000000000014" y="207.6666666666667" style="white-space:pre;" fill="#005400" font-family="DejaVu Sans" font-size="34.0" text-anchor="middle" dominant-baseline="baseline" xml:space="preserve" transform="rotate(0.0 -45.000000000000014 213.33333333333337)">XD 2⌀20,span=31</text></g></svg>
  TextPositionType = 0
  WayPoints = (2) [(0,0,0),(50,0,0)]
  WayPointsType = 0
  X = 147.618
  Y = 125
FEATURE [TechDraw::DrawViewSymbolPython] ReinforcementDimensioning015  # drawing view (typed FeaturePython)
  DimensionBottomOffset = 16
  DimensionFormat = %M %C⌀%D,span=%S
  DimensionLeftOffset = 10
  DimensionRightOffset = 16
  DimensionTopOffset = 10
  Font = DejaVu Sans
  FontSize = 3
  LineEndSymbol = 0
  LineMidPointSymbol = 1
  LineStartSymbol = 3
  LineStyle = 0
  LockPosition = false
  MultiRebar_LineEndSymbol = 0
  MultiRebar_LineStartSymbol = 0
  MultiRebar_OuterDimension = true
  MultiRebar_TextPositionType = 0
  ParentDrawingView = -> ReinforcementDrawingView001
  Rebar = -> Rebar016
  Rotation = 0
  Scale = 0.0882353
  ScaleType = 2
  SingleRebar_LineEndSymbol = 0
  SingleRebar_LineStartSymbol = 3
  SingleRebar_OuterDimension = false
  SingleRebar_TextPositionType = 1
  StrokeWidth = 0.25
  Symbol = <svg version="1.1" xmlns="http://www.w3.org/2000/svg" xmlns:xlink="http://www.w3.org/1999/xlink" xmlns:freecad="http://www.freecadweb.org/wiki/index.php?title=Svg_Namespace" width="300.0mm" height="1700.0mm" viewBox="0 0 300.0 1700.0"><g transform="translate(150.0, 1600.0)"><g><path d="M331.3333333333333 -404.0 L0.0 -404.0" style="stroke:#00007f;stroke-width:2.833333333333333;stroke-linecap:round;fill:none;" stroke-dasharray="" /><g id="line_mid_points" /><path d="M0,0 -8,-1.5 V1.5 L0,0" style="stroke:#00007f;fill:#00007f;stroke-width:2.833333333333333;stroke-linecap:round;stroke-linejoin:bevel;" transform="translate(0.0 -404.0) rotate(180.0 0 0)" /></g><text x="331.3333333333333" y="-387.0" style="white-space:pre;" fill="#005400" font-family="DejaVu Sans" font-size="34.0" text-anchor="start" dominant-baseline="baseline" xml:space="preserve">XD 1⌀16,span=0</text></g></svg>
  TextPositionType = 0
  WayPoints = (2) [(0,0,0),(50,0,0)]
  WayPointsType = 0
  X = 147.618
  Y = 125
FEATURE [TechDraw::DrawViewSymbolPython] ReinforcementDimensioning016  # drawing view (typed FeaturePython)
  DimensionBottomOffset = 16
  DimensionFormat = %M %C⌀%D,span=%S
  DimensionLeftOffset = 10
  DimensionRightOffset = 22
  DimensionTopOffset = 10
  Font = DejaVu Sans
  FontSize = 3
  LineEndSymbol = 0
  LineMidPointSymbol = 1
  LineStartSymbol = 3
  LineStyle = 0
  LockPosition = false
  MultiRebar_LineEndSymbol = 0
  MultiRebar_LineStartSymbol = 0
  MultiRebar_OuterDimension = true
  MultiRebar_TextPositionType = 0
  ParentDrawingView = -> ReinforcementDrawingView001
  Rebar = -> Rebar017
  Rotation = 0
  Scale = 0.0882353
  ScaleType = 2
  SingleRebar_LineEndSymbol = 0
  SingleRebar_LineStartSymbol = 3
  SingleRebar_OuterDimension = false
  SingleRebar_TextPositionType = 1
  StrokeWidth = 0.25
  Symbol = <svg version="1.1" xmlns="http://www.w3.org/2000/svg" xmlns:xlink="http://www.w3.org/1999/xlink" xmlns:freecad="http://www.freecadweb.org/wiki/index.php?title=Svg_Namespace" width="300.0mm" height="1700.0mm" viewBox="0 0 300.0 1700.0"><g transform="translate(150.0, 1600.0)"><g><path d="M29.333333333333343 224.6666666666667 L29.333333333333343 281.33333333333337 L60.66666666666666 281.33333333333337 L60.66666666666666 224.6666666666667" style="stroke:#00007f;stroke-width:2.833333333333333;stroke-linecap:round;fill:none;" stroke-dasharray="" /><path d="M0,0 -8,-1.5 V1.5 L0,0" style="stroke:#00007f;fill:#00007f;stroke-width:2.833333333333333;stroke-linecap:round;stroke-linejoin:bevel;" transform="translate(29.333333333333343 224.6666666666667) rotate(-90.0 0 0)" /><g id="line_mid_points"><circle cx="0" cy="0" r="5.666666666666666" fill="#00007f" transform="translate(29.333333333333343 281.33333333333337) rotate(90.0 0 0)" /><circle cx="0" cy="0" r="5.666666666666666" fill="#00007f" transform="translate(60.66666666666666 281.33333333333337) rotate(0.0 0 0)" /></g><path d="M0,0 -8,-1.5 V1.5 L0,0" style="stroke:#00007f;fill:#00007f;stroke-width:2.833333333333333;stroke-linecap:round;stroke-linejoin:bevel;" transform="translate(60.66666666666666 224.6666666666667) rotate(-90.0 0 0)" /></g><text x="45.0" y="275.6666666666667" style="white-space:pre;" fill="#005400" font-family="DejaVu Sans" font-size="34.0" text-anchor="middle" dominant-baseline="baseline" xml:space="preserve" transform="rotate(0.0 45.0 281.33333333333337)">XD 2⌀20,span=31</text></g></svg>
  TextPositionType = 0
  WayPoints = (2) [(0,0,0),(50,0,0)]
  WayPointsType = 0
  X = 147.618
  Y = 125
FEATURE [TechDraw::DrawViewSymbolPython] ReinforcementDimensioning017  # drawing view (typed FeaturePython)
  DimensionBottomOffset = 22
  DimensionFormat = %M %C⌀%D,span=%S
  DimensionLeftOffset = 10
  DimensionRightOffset = 22
  DimensionTopOffset = 10
  Font = DejaVu Sans
  FontSize = 3
  LineEndSymbol = 0
  LineMidPointSymbol = 1
  LineStartSymbol = 3
  LineStyle = 0
  LockPosition = false
  MultiRebar_LineEndSymbol = 0
  MultiRebar_LineStartSymbol = 0
  MultiRebar_OuterDimension = true
  MultiRebar_TextPositionType = 0
  ParentDrawingView = -> ReinforcementDrawingView001
  Rebar = -> Rebar018
  Rotation = 0
  Scale = 0.0882353
  ScaleType = 2
  SingleRebar_LineEndSymbol = 0
  SingleRebar_LineStartSymbol = 3
  SingleRebar_OuterDimension = false
  SingleRebar_TextPositionType = 1
  StrokeWidth = 0.25
  Symbol = <svg version="1.1" xmlns="http://www.w3.org/2000/svg" xmlns:xlink="http://www.w3.org/1999/xlink" xmlns:freecad="http://www.freecadweb.org/wiki/index.php?title=Svg_Namespace" width="300.0mm" height="1700.0mm" viewBox="0 0 300.0 1700.0"><g transform="translate(150.0, 1600.0)"><g><path d="M-60.66666666666667 292.6666666666667 L-60.66666666666667 349.33333333333337 L-29.333333333333357 349.33333333333337 L-29.333333333333357 292.6666666666667" style="stroke:#00007f;stroke-width:2.833333333333333;stroke-linecap:round;fill:none;" stroke-dasharray="" /><path d="M0,0 -8,-1.5 V1.5 L0,0" style="stroke:#00007f;fill:#00007f;stroke-width:2.833333333333333;stroke-linecap:round;stroke-linejoin:bevel;" transform="translate(-60.66666666666667 292.6666666666667) rotate(-90.0 0 0)" /><g id="line_mid_points"><circle cx="0" cy="0" r="5.666666666666666" fill="#00007f" transform="translate(-60.66666666666667 349.33333333333337) rotate(90.0 0 0)" /><circle cx="0" cy="0" r="5.666666666666666" fill="#00007f" transform="translate(-29.333333333333357 349.33333333333337) rotate(0.0 0 0)" /></g><path d="M0,0 -8,-1.5 V1.5 L0,0" style="stroke:#00007f;fill:#00007f;stroke-width:2.833333333333333;stroke-linecap:round;stroke-linejoin:bevel;" transform="translate(-29.333333333333357 292.6666666666667) rotate(-90.0 0 0)" /></g><text x="-45.000000000000014" y="343.6666666666667" style="white-space:pre;" fill="#005400" font-family="DejaVu Sans" font-size="34.0" text-anchor="middle" dominant-baseline="baseline" xml:space="preserve" transform="rotate(0.0 -45.000000000000014 349.33333333333337)">XD 2⌀20,span=31</text></g></svg>
  TextPositionType = 0
  WayPoints = (2) [(0,0,0),(50,0,0)]
  WayPointsType = 0
  X = 147.618
  Y = 125
FEATURE [TechDraw::DrawViewSymbolPython] ReinforcementDimensioning018  # drawing view (typed FeaturePython)
  DimensionBottomOffset = 28
  DimensionFormat = %M %C⌀%D,span=%S
  DimensionLeftOffset = 10
  DimensionRightOffset = 22
  DimensionTopOffset = 10
  Font = DejaVu Sans
  FontSize = 3
  LineEndSymbol = 0
  LineMidPointSymbol = 1
  LineStartSymbol = 3
  LineStyle = 0
  LockPosition = false
  MultiRebar_LineEndSymbol = 0
  MultiRebar_LineStartSymbol = 0
  MultiRebar_OuterDimension = true
  MultiRebar_TextPositionType = 0
  ParentDrawingView = -> ReinforcementDrawingView001
  Rebar = -> Rebar019
  Rotation = 0
  Scale = 0.0882353
  ScaleType = 2
  SingleRebar_LineEndSymbol = 0
  SingleRebar_LineStartSymbol = 3
  SingleRebar_OuterDimension = false
  SingleRebar_TextPositionType = 1
  StrokeWidth = 0.25
  Symbol = <svg version="1.1" xmlns="http://www.w3.org/2000/svg" xmlns:xlink="http://www.w3.org/1999/xlink" xmlns:freecad="http://www.freecadweb.org/wiki/index.php?title=Svg_Namespace" width="300.0mm" height="1700.0mm" viewBox="0 0 300.0 1700.0"><g transform="translate(150.0, 1600.0)"><g><path d="M399.3333333333333 -323.0 L0.0 -323.0" style="stroke:#00007f;stroke-width:2.833333333333333;stroke-linecap:round;fill:none;" stroke-dasharray="" /><g id="line_mid_points" /><path d="M0,0 -8,-1.5 V1.5 L0,0" style="stroke:#00007f;fill:#00007f;stroke-width:2.833333333333333;stroke-linecap:round;stroke-linejoin:bevel;" transform="translate(0.0 -323.0) rotate(180.0 0 0)" /></g><text x="399.3333333333333" y="-306.0" style="white-space:pre;" fill="#005400" font-family="DejaVu Sans" font-size="34.0" text-anchor="start" dominant-baseline="baseline" xml:space="preserve">XD 1⌀16,span=0</text></g></svg>
  TextPositionType = 0
  WayPoints = (2) [(0,0,0),(50,0,0)]
  WayPointsType = 0
  X = 147.618
  Y = 125
FEATURE [TechDraw::DrawViewSymbolPython] ReinforcementDimensioning019  # drawing view (typed FeaturePython)
  DimensionBottomOffset = 28
  DimensionFormat = %M %C⌀%D,span=%S
  DimensionLeftOffset = 10
  DimensionRightOffset = 28
  DimensionTopOffset = 10
  Font = DejaVu Sans
  FontSize = 3
  LineEndSymbol = 0
  LineMidPointSymbol = 1
  LineStartSymbol = 3
  LineStyle = 0
  LockPosition = false
  MultiRebar_LineEndSymbol = 0
  MultiRebar_LineStartSymbol = 0
  MultiRebar_OuterDimension = true
  MultiRebar_TextPositionType = 0
  ParentDrawingView = -> ReinforcementDrawingView001
  Rebar = -> Rebar020
  Rotation = 0
  Scale = 0.0882353
  ScaleType = 2
  SingleRebar_LineEndSymbol = 0
  SingleRebar_LineStartSymbol = 3
  SingleRebar_OuterDimension = false
  SingleRebar_TextPositionType = 1
  StrokeWidth = 0.25
  Symbol = <svg version="1.1" xmlns="http://www.w3.org/2000/svg" xmlns:xlink="http://www.w3.org/1999/xlink" xmlns:freecad="http://www.freecadweb.org/wiki/index.php?title=Svg_Namespace" width="300.0mm" height="1700.0mm" viewBox="0 0 300.0 1700.0"><g transform="translate(150.0, 1600.0)"><g><path d="M29.333333333333343 360.6666666666667 L29.333333333333343 417.33333333333337 L60.66666666666666 417.33333333333337 L60.66666666666666 360.6666666666667" style="stroke:#00007f;stroke-width:2.833333333333333;stroke-linecap:round;fill:none;" stroke-dasharray="" /><path d="M0,0 -8,-1.5 V1.5 L0,0" style="stroke:#00007f;fill:#00007f;stroke-width:2.833333333333333;stroke-linecap:round;stroke-linejoin:bevel;" transform="translate(29.333333333333343 360.6666666666667) rotate(-90.0 0 0)" /><g id="line_mid_points"><circle cx="0" cy="0" r="5.666666666666666" fill="#00007f" transform="translate(29.333333333333343 417.33333333333337) rotate(90.0 0 0)" /><circle cx="0" cy="0" r="5.666666666666666" fill="#00007f" transform="translate(60.66666666666666 417.33333333333337) rotate(0.0 0 0)" /></g><path d="M0,0 -8,-1.5 V1.5 L0,0" style="stroke:#00007f;fill:#00007f;stroke-width:2.833333333333333;stroke-linecap:round;stroke-linejoin:bevel;" transform="translate(60.66666666666666 360.6666666666667) rotate(-90.0 0 0)" /></g><text x="45.0" y="411.6666666666667" style="white-space:pre;" fill="#005400" font-family="DejaVu Sans" font-size="34.0" text-anchor="middle" dominant-baseline="baseline" xml:space="preserve" transform="rotate(0.0 45.0 417.33333333333337)">XD 2⌀20,span=31</text></g></svg>
  TextPositionType = 0
  WayPoints = (2) [(0,0,0),(50,0,0)]
  WayPointsType = 0
  X = 147.618
  Y = 125
FEATURE [TechDraw::DrawViewSymbolPython] ReinforcementDimensioning020  # drawing view (typed FeaturePython)
  DimensionBottomOffset = 34
  DimensionFormat = %M %C⌀%D,span=%S
  DimensionLeftOffset = 10
  DimensionRightOffset = 28
  DimensionTopOffset = 10
  Font = DejaVu Sans
  FontSize = 3
  LineEndSymbol = 0
  LineMidPointSymbol = 1
  LineStartSymbol = 3
  LineStyle = 0
  LockPosition = false
  MultiRebar_LineEndSymbol = 0
  MultiRebar_LineStartSymbol = 0
  MultiRebar_OuterDimension = true
  MultiRebar_TextPositionType = 0
  ParentDrawingView = -> ReinforcementDrawingView001
  Rebar = -> Rebar021
  Rotation = 0
  Scale = 0.0882353
  ScaleType = 2
  SingleRebar_LineEndSymbol = 0
  SingleRebar_LineStartSymbol = 3
  SingleRebar_OuterDimension = false
  SingleRebar_TextPositionType = 1
  StrokeWidth = 0.25
  Symbol = <svg version="1.1" xmlns="http://www.w3.org/2000/svg" xmlns:xlink="http://www.w3.org/1999/xlink" xmlns:freecad="http://www.freecadweb.org/wiki/index.php?title=Svg_Namespace" width="300.0mm" height="1700.0mm" viewBox="0 0 300.0 1700.0"><g transform="translate(150.0, 1600.0)"><g><path d="M108.0 485.33333333333337 L108.0 90.00000000000003" style="stroke:#00007f;stroke-width:2.833333333333333;stroke-linecap:round;fill:none;" stroke-dasharray="" /><g id="line_mid_points" /><path d="M0,0 -8,-1.5 V1.5 L0,0" style="stroke:#00007f;fill:#00007f;stroke-width:2.833333333333333;stroke-linecap:round;stroke-linejoin:bevel;" transform="translate(108.0 90.00000000000003) rotate(-90.0 0 0)" /></g><text x="108.0" y="502.33333333333337" style="white-space:pre;" fill="#005400" font-family="DejaVu Sans" font-size="34.0" text-anchor="middle" dominant-baseline="baseline" xml:space="preserve">YD 1⌀20,span=0</text></g></svg>
  TextPositionType = 0
  WayPoints = (2) [(0,0,0),(50,0,0)]
  WayPointsType = 0
  X = 147.618
  Y = 125
FEATURE [TechDraw::DrawViewSymbolPython] ReinforcementDimensioning021  # drawing view (typed FeaturePython)
  DimensionBottomOffset = 40
  DimensionFormat = %M %C⌀%D,span=%S
  DimensionLeftOffset = 10
  DimensionRightOffset = 28
  DimensionTopOffset = 10
  Font = DejaVu Sans
  FontSize = 3
  LineEndSymbol = 0
  LineMidPointSymbol = 1
  LineStartSymbol = 3
  LineStyle = 0
  LockPosition = false
  MultiRebar_LineEndSymbol = 0
  MultiRebar_LineStartSymbol = 0
  MultiRebar_OuterDimension = true
  MultiRebar_TextPositionType = 0
  ParentDrawingView = -> ReinforcementDrawingView001
  Rebar = -> Rebar022
  Rotation = 0
  Scale = 0.0882353
  ScaleType = 2
  SingleRebar_LineEndSymbol = 0
  SingleRebar_LineStartSymbol = 3
  SingleRebar_OuterDimension = false
  SingleRebar_TextPositionType = 1
  StrokeWidth = 0.25
  Symbol = <svg version="1.1" xmlns="http://www.w3.org/2000/svg" xmlns:xlink="http://www.w3.org/1999/xlink" xmlns:freecad="http://www.freecadweb.org/wiki/index.php?title=Svg_Namespace" width="300.0mm" height="1700.0mm" viewBox="0 0 300.0 1700.0"><g transform="translate(150.0, 1600.0)"><g><path d="M107.0 553.3333333333334 L107.0 92.00000000000003" style="stroke:#00007f;stroke-width:2.833333333333333;stroke-linecap:round;fill:none;" stroke-dasharray="" /><g id="line_mid_points" /><path d="M0,0 -8,-1.5 V1.5 L0,0" style="stroke:#00007f;fill:#00007f;stroke-width:2.833333333333333;stroke-linecap:round;stroke-linejoin:bevel;" transform="translate(107.0 92.00000000000003) rotate(-90.0 0 0)" /></g><text x="107.0" y="570.3333333333334" style="white-space:pre;" fill="#005400" font-family="DejaVu Sans" font-size="34.0" text-anchor="middle" dominant-baseline="baseline" xml:space="preserve">YD 1⌀16,span=0</text></g></svg>
  TextPositionType = 0
  WayPoints = (2) [(0,0,0),(50,0,0)]
  WayPointsType = 0
  X = 147.618
  Y = 125
FEATURE [TechDraw::DrawViewSymbolPython] ReinforcementDimensioning022  # drawing view (typed FeaturePython)
  DimensionBottomOffset = 46
  DimensionFormat = %M %C⌀%D,span=%S
  DimensionLeftOffset = 10
  DimensionRightOffset = 28
  DimensionTopOffset = 10
  Font = DejaVu Sans
  FontSize = 3
  LineEndSymbol = 0
  LineMidPointSymbol = 1
  LineStartSymbol = 3
  LineStyle = 0
  LockPosition = false
  MultiRebar_LineEndSymbol = 0
  MultiRebar_LineStartSymbol = 0
  MultiRebar_OuterDimension = true
  MultiRebar_TextPositionType = 0
  ParentDrawingView = -> ReinforcementDrawingView001
  Rebar = -> Rebar024
  Rotation = 0
  Scale = 0.0882353
  ScaleType = 2
  SingleRebar_LineEndSymbol = 0
  SingleRebar_LineStartSymbol = 3
  SingleRebar_OuterDimension = false
  SingleRebar_TextPositionType = 1
  StrokeWidth = 0.25
  Symbol = <svg version="1.1" xmlns="http://www.w3.org/2000/svg" xmlns:xlink="http://www.w3.org/1999/xlink" xmlns:freecad="http://www.freecadweb.org/wiki/index.php?title=Svg_Namespace" width="300.0mm" height="1700.0mm" viewBox="0 0 300.0 1700.0"><g transform="translate(150.0, 1600.0)"><g><path d="M-114.0 621.3333333333333 L-114.0 90.00000000000003" style="stroke:#00007f;stroke-width:2.833333333333333;stroke-linecap:round;fill:none;" stroke-dasharray="" /><g id="line_mid_points" /><path d="M0,0 -8,-1.5 V1.5 L0,0" style="stroke:#00007f;fill:#00007f;stroke-width:2.833333333333333;stroke-linecap:round;stroke-linejoin:bevel;" transform="translate(-114.0 90.00000000000003) rotate(-90.0 0 0)" /></g><text x="-114.0" y="638.3333333333333" style="white-space:pre;" fill="#005400" font-family="DejaVu Sans" font-size="34.0" text-anchor="middle" dominant-baseline="baseline" xml:space="preserve">YD 1⌀20,span=0</text></g></svg>
  TextPositionType = 0
  WayPoints = (2) [(0,0,0),(50,0,0)]
  WayPointsType = 0
  X = 147.618
  Y = 125
FEATURE [TechDraw::DrawViewSymbolPython] ReinforcementDimensioning023  # drawing view (typed FeaturePython)
  DimensionBottomOffset = 52
  DimensionFormat = %M %C⌀%D,span=%S
  DimensionLeftOffset = 10
  DimensionRightOffset = 28
  DimensionTopOffset = 10
  Font = DejaVu Sans
  FontSize = 3
  LineEndSymbol = 0
  LineMidPointSymbol = 1
  LineStartSymbol = 3
  LineStyle = 0
  LockPosition = false
  MultiRebar_LineEndSymbol = 0
  MultiRebar_LineStartSymbol = 0
  MultiRebar_OuterDimension = true
  MultiRebar_TextPositionType = 0
  ParentDrawingView = -> ReinforcementDrawingView001
  Rebar = -> Rebar025
  Rotation = 0
  Scale = 0.0882353
  ScaleType = 2
  SingleRebar_LineEndSymbol = 0
  SingleRebar_LineStartSymbol = 3
  SingleRebar_OuterDimension = false
  SingleRebar_TextPositionType = 1
  StrokeWidth = 0.25
  Symbol = <svg version="1.1" xmlns="http://www.w3.org/2000/svg" xmlns:xlink="http://www.w3.org/1999/xlink" xmlns:freecad="http://www.freecadweb.org/wiki/index.php?title=Svg_Namespace" width="300.0mm" height="1700.0mm" viewBox="0 0 300.0 1700.0"><g transform="translate(150.0, 1600.0)"><g><path d="M-134.0 689.3333333333333 L-134.0 92.00000000000003" style="stroke:#00007f;stroke-width:2.833333333333333;stroke-linecap:round;fill:none;" stroke-dasharray="" /><g id="line_mid_points" /><path d="M0,0 -8,-1.5 V1.5 L0,0" style="stroke:#00007f;fill:#00007f;stroke-width:2.833333333333333;stroke-linecap:round;stroke-linejoin:bevel;" transform="translate(-134.0 92.00000000000003) rotate(-90.0 0 0)" /></g><text x="-134.0" y="706.3333333333333" style="white-space:pre;" fill="#005400" font-family="DejaVu Sans" font-size="34.0" text-anchor="middle" dominant-baseline="baseline" xml:space="preserve">YD 1⌀16,span=0</text></g></svg>
  TextPositionType = 0
  WayPoints = (2) [(0,0,0),(50,0,0)]
  WayPointsType = 0
  X = 147.618
  Y = 125
FEATURE [TechDraw::DrawViewSymbolPython] ReinforcementDimensioning024  # drawing view (typed FeaturePython)
  DimensionBottomOffset = 58
  DimensionFormat = %M %C⌀%D,span=%S
  DimensionLeftOffset = 10
  DimensionRightOffset = 28
  DimensionTopOffset = 10
  Font = DejaVu Sans
  FontSize = 3
  LineEndSymbol = 0
  LineMidPointSymbol = 1
  LineStartSymbol = 3
  LineStyle = 0
  LockPosition = false
  MultiRebar_LineEndSymbol = 0
  MultiRebar_LineStartSymbol = 0
  MultiRebar_OuterDimension = true
  MultiRebar_TextPositionType = 0
  ParentDrawingView = -> ReinforcementDrawingView001
  Rebar = -> Rebar
  Rotation = 0
  Scale = 0.0882353
  ScaleType = 2
  SingleRebar_LineEndSymbol = 0
  SingleRebar_LineStartSymbol = 3
  SingleRebar_OuterDimension = false
  SingleRebar_TextPositionType = 1
  StrokeWidth = 0.25
  Symbol = <svg version="1.1" xmlns="http://www.w3.org/2000/svg" xmlns:xlink="http://www.w3.org/1999/xlink" xmlns:freecad="http://www.freecadweb.org/wiki/index.php?title=Svg_Namespace" width="300.0mm" height="1700.0mm" viewBox="0 0 300.0 1700.0"><g transform="translate(150.0, 1600.0)"><g><path d="M-263.3333333333333 -261.0 L-92.0 -261.0" style="stroke:#00007f;stroke-width:2.833333333333333;stroke-linecap:round;fill:none;" stroke-dasharray="" /><g id="line_mid_points" /><path d="M0,0 -8,-1.5 V1.5 L0,0" style="stroke:#00007f;fill:#00007f;stroke-width:2.833333333333333;stroke-linecap:round;stroke-linejoin:bevel;" transform="translate(-92.0 -261.0) rotate(0.0 0 0)" /></g><text x="-263.3333333333333" y="-244.0" style="white-space:pre;" fill="#005400" font-family="DejaVu Sans" font-size="34.0" text-anchor="end" dominant-baseline="baseline" xml:space="preserve">M 2⌀20,span=184</text></g></svg>
  TextPositionType = 0
  WayPoints = (2) [(0,0,0),(50,0,0)]
  WayPointsType = 0
  X = 147.618
  Y = 125
FEATURE [TechDraw::DrawViewSymbolPython] ReinforcementDimensioning025  # drawing view (typed FeaturePython)
  DimensionBottomOffset = 58
  DimensionFormat = %M %C⌀%D,span=%S
  DimensionLeftOffset = 16
  DimensionRightOffset = 28
  DimensionTopOffset = 10
  Font = DejaVu Sans
  FontSize = 3
  LineEndSymbol = 0
  LineMidPointSymbol = 1
  LineStartSymbol = 3
  LineStyle = 0
  LockPosition = false
  MultiRebar_LineEndSymbol = 0
  MultiRebar_LineStartSymbol = 0
  MultiRebar_OuterDimension = true
  MultiRebar_TextPositionType = 0
  ParentDrawingView = -> ReinforcementDrawingView001
  Rebar = -> Rebar001
  Rotation = 0
  Scale = 0.0882353
  ScaleType = 2
  SingleRebar_LineEndSymbol = 0
  SingleRebar_LineStartSymbol = 3
  SingleRebar_OuterDimension = false
  SingleRebar_TextPositionType = 1
  StrokeWidth = 0.25
  Symbol = <svg version="1.1" xmlns="http://www.w3.org/2000/svg" xmlns:xlink="http://www.w3.org/1999/xlink" xmlns:freecad="http://www.freecadweb.org/wiki/index.php?title=Svg_Namespace" width="300.0mm" height="1700.0mm" viewBox="0 0 300.0 1700.0"><g transform="translate(150.0, 1600.0)"><g><path d="M467.3333333333333 -577.0 L92.0 -577.0" style="stroke:#00007f;stroke-width:2.833333333333333;stroke-linecap:round;fill:none;" stroke-dasharray="" /><g id="line_mid_points" /><path d="M0,0 -8,-1.5 V1.5 L0,0" style="stroke:#00007f;fill:#00007f;stroke-width:2.833333333333333;stroke-linecap:round;stroke-linejoin:bevel;" transform="translate(92.0 -577.0) rotate(180.0 0 0)" /></g><text x="467.3333333333333" y="-560.0" style="white-space:pre;" fill="#005400" font-family="DejaVu Sans" font-size="34.0" text-anchor="start" dominant-baseline="baseline" xml:space="preserve">M 2⌀20,span=184</text></g></svg>
  TextPositionType = 0
  WayPoints = (2) [(0,0,0),(50,0,0)]
  WayPointsType = 0
  X = 147.618
  Y = 125
FEATURE [TechDraw::DrawPage] TechDraw__DrawPage001  label="Column Drawing001"
  KeepUpdated = true
  NextBalloonIndex = 1
  ProjectionType = 0
  Template = -> Template001
  Views = -> [ReinforcementDrawingView001,ReinforcementDimensioning013,ReinforcementDimensioning014,ReinforcementDimensioning015,ReinforcementDimensioning016,ReinforcementDimensioning017,ReinforcementDimensioning018,ReinforcementDimensioning019,ReinforcementDimensioning020,ReinforcementDimensioning021,ReinforcementDimensioning022,ReinforcementDimensioning023,ReinforcementDimensioning024,+1 more]
FEATURE [TechDraw::DrawSVGTemplate] Template002
  Height = 210
  Orientation = 1
  Width = 297
FEATURE [TechDraw::DrawViewSymbolPython] ReinforcementDrawingView002  label="Left View"  # drawing view (typed FeaturePython)
  DimensionBottomOffset = 10
  DimensionLeftOffset = 34
  DimensionRightOffset = 28
  DimensionTopOffset = 40
  Height = 1700
  LeftOffset = 134.382
  LockPosition = false
  MaxHeight = 210
  MaxWidth = 297
  MinBottomOffset = 10
  MinRightOffset = 20
  PositionType = 0
  Rebars = -> [Rebar,Rebar001,Rebar002,Rebar015,Rebar016,Rebar017,Rebar018,Rebar019,Rebar020,Rebar021,Rebar022,Rebar023,Rebar024,Rebar025,Rebar026]
  RebarsColorStyle = 0
  RebarsStrokeWidth = 0.35
  Rotation = 0
  Scale = 0.1
  ScaleType = 1
  Structure = -> Structure
  StructureColorStyle = 0
  StructureStrokeWidth = 0.5
  Symbol = <blob: 6612 chars omitted>
  Template = -> Template002
  TopOffset = 30
  View = 2
  VisibleRebars = -> [Rebar002,Rebar015,Rebar016,Rebar018,Rebar019,Rebar021,Rebar022,Rebar023,Rebar024,Rebar025,Rebar026,Rebar]
  Width = 300
  X = 149.382
  Y = 95
  expr: LeftOffset = .Template.Width.Value / 2 - .Width.Value * .Scale / 2
FEATURE [TechDraw::DrawViewSymbolPython] ReinforcementDimensioning026  # drawing view (typed FeaturePython)
  DimensionBottomOffset = 10
  DimensionFormat = %M %C⌀%D,span=%S
  DimensionLeftOffset = 10
  DimensionRightOffset = 10
  DimensionTopOffset = 10
  Font = DejaVu Sans
  FontSize = 3
  LineEndSymbol = 0
  LineMidPointSymbol = 1
  LineStartSymbol = 3
  LineStyle = 0
  LockPosition = false
  MultiRebar_LineEndSymbol = 0
  MultiRebar_LineStartSymbol = 0
  MultiRebar_OuterDimension = true
  MultiRebar_TextPositionType = 0
  ParentDrawingView = -> ReinforcementDrawingView002
  Rebar = -> Rebar002
  Rotation = 0
  Scale = 0.1
  ScaleType = 2
  SingleRebar_LineEndSymbol = 0
  SingleRebar_LineStartSymbol = 3
  SingleRebar_OuterDimension = false
  SingleRebar_TextPositionType = 1
  StrokeWidth = 0.25
  Symbol = <blob: 4599 chars omitted>
  TextPositionType = 0
  WayPoints = (2) [(0,0,0),(50,0,0)]
  WayPointsType = 0
  X = 149.382
  Y = 95
FEATURE [TechDraw::DrawViewSymbolPython] ReinforcementDimensioning027  # drawing view (typed FeaturePython)
  DimensionBottomOffset = 10
  DimensionFormat = %M %C⌀%D,span=%S
  DimensionLeftOffset = 10
  DimensionRightOffset = 16
  DimensionTopOffset = 10
  Font = DejaVu Sans
  FontSize = 3
  LineEndSymbol = 0
  LineMidPointSymbol = 1
  LineStartSymbol = 3
  LineStyle = 0
  LockPosition = false
  MultiRebar_LineEndSymbol = 0
  MultiRebar_LineStartSymbol = 0
  MultiRebar_OuterDimension = true
  MultiRebar_TextPositionType = 0
  ParentDrawingView = -> ReinforcementDrawingView002
  Rebar = -> Rebar015
  Rotation = 0
  Scale = 0.1
  ScaleType = 2
  SingleRebar_LineEndSymbol = 0
  SingleRebar_LineStartSymbol = 3
  SingleRebar_OuterDimension = false
  SingleRebar_TextPositionType = 1
  StrokeWidth = 0.25
  Symbol = <svg version="1.1" xmlns="http://www.w3.org/2000/svg" xmlns:xlink="http://www.w3.org/1999/xlink" xmlns:freecad="http://www.freecadweb.org/wiki/index.php?title=Svg_Namespace" width="300.0mm" height="1700.0mm" viewBox="0 0 300.0 1700.0"><g transform="translate(150.0, 1600.0)"><g><path d="M128.0 -1700.0 L128.0 -1590.0" style="stroke:#00007f;stroke-width:2.5;stroke-linecap:round;fill:none;" stroke-dasharray="" /><g id="line_mid_points" /><path d="M0,0 -8,-1.5 V1.5 L0,0" style="stroke:#00007f;fill:#00007f;stroke-width:2.5;stroke-linecap:round;stroke-linejoin:bevel;" transform="translate(128.0 -1590.0) rotate(90.0 0 0)" /></g><text x="128.0" y="-1700.0" style="white-space:pre;" fill="#005400" font-family="DejaVu Sans" font-size="30.0" text-anchor="middle" dominant-baseline="baseline" xml:space="preserve">XD 2⌀20,span=31</text></g></svg>
  TextPositionType = 0
  WayPoints = (2) [(0,0,0),(50,0,0)]
  WayPointsType = 0
  X = 149.382
  Y = 95
FEATURE [TechDraw::DrawViewSymbolPython] ReinforcementDimensioning028  # drawing view (typed FeaturePython)
  DimensionBottomOffset = 10
  DimensionFormat = %M %C⌀%D,span=%S
  DimensionLeftOffset = 10
  DimensionRightOffset = 16
  DimensionTopOffset = 16
  Font = DejaVu Sans
  FontSize = 3
  LineEndSymbol = 0
  LineMidPointSymbol = 1
  LineStartSymbol = 3
  LineStyle = 0
  LockPosition = false
  MultiRebar_LineEndSymbol = 0
  MultiRebar_LineStartSymbol = 0
  MultiRebar_OuterDimension = true
  MultiRebar_TextPositionType = 0
  ParentDrawingView = -> ReinforcementDrawingView002
  Rebar = -> Rebar016
  Rotation = 0
  Scale = 0.1
  ScaleType = 2
  SingleRebar_LineEndSymbol = 0
  SingleRebar_LineStartSymbol = 3
  SingleRebar_OuterDimension = false
  SingleRebar_TextPositionType = 1
  StrokeWidth = 0.25
  Symbol = <svg version="1.1" xmlns="http://www.w3.org/2000/svg" xmlns:xlink="http://www.w3.org/1999/xlink" xmlns:freecad="http://www.freecadweb.org/wiki/index.php?title=Svg_Namespace" width="300.0mm" height="1700.0mm" viewBox="0 0 300.0 1700.0"><g transform="translate(150.0, 1600.0)"><g><path d="M111.0 -1760.0 L111.0 -1592.0" style="stroke:#00007f;stroke-width:2.5;stroke-linecap:round;fill:none;" stroke-dasharray="" /><g id="line_mid_points" /><path d="M0,0 -8,-1.5 V1.5 L0,0" style="stroke:#00007f;fill:#00007f;stroke-width:2.5;stroke-linecap:round;stroke-linejoin:bevel;" transform="translate(111.0 -1592.0) rotate(90.0 0 0)" /></g><text x="111.0" y="-1760.0" style="white-space:pre;" fill="#005400" font-family="DejaVu Sans" font-size="30.0" text-anchor="middle" dominant-baseline="baseline" xml:space="preserve">XD 1⌀16,span=0</text></g></svg>
  TextPositionType = 0
  WayPoints = (2) [(0,0,0),(50,0,0)]
  WayPointsType = 0
  X = 149.382
  Y = 95
FEATURE [TechDraw::DrawViewSymbolPython] ReinforcementDimensioning029  # drawing view (typed FeaturePython)
  DimensionBottomOffset = 10
  DimensionFormat = %M %C⌀%D,span=%S
  DimensionLeftOffset = 10
  DimensionRightOffset = 16
  DimensionTopOffset = 22
  Font = DejaVu Sans
  FontSize = 3
  LineEndSymbol = 0
  LineMidPointSymbol = 1
  LineStartSymbol = 3
  LineStyle = 0
  LockPosition = false
  MultiRebar_LineEndSymbol = 0
  MultiRebar_LineStartSymbol = 0
  MultiRebar_OuterDimension = true
  MultiRebar_TextPositionType = 0
  ParentDrawingView = -> ReinforcementDrawingView002
  Rebar = -> Rebar018
  Rotation = 0
  Scale = 0.1
  ScaleType = 2
  SingleRebar_LineEndSymbol = 0
  SingleRebar_LineStartSymbol = 3
  SingleRebar_OuterDimension = false
  SingleRebar_TextPositionType = 1
  StrokeWidth = 0.25
  Symbol = <svg version="1.1" xmlns="http://www.w3.org/2000/svg" xmlns:xlink="http://www.w3.org/1999/xlink" xmlns:freecad="http://www.freecadweb.org/wiki/index.php?title=Svg_Namespace" width="300.0mm" height="1700.0mm" viewBox="0 0 300.0 1700.0"><g transform="translate(150.0, 1600.0)"><g><path d="M-137.0 -1820.0 L-137.0 -1590.0" style="stroke:#00007f;stroke-width:2.5;stroke-linecap:round;fill:none;" stroke-dasharray="" /><g id="line_mid_points" /><path d="M0,0 -8,-1.5 V1.5 L0,0" style="stroke:#00007f;fill:#00007f;stroke-width:2.5;stroke-linecap:round;stroke-linejoin:bevel;" transform="translate(-137.0 -1590.0) rotate(90.0 0 0)" /></g><text x="-137.0" y="-1820.0" style="white-space:pre;" fill="#005400" font-family="DejaVu Sans" font-size="30.0" text-anchor="middle" dominant-baseline="baseline" xml:space="preserve">XD 2⌀20,span=31</text></g></svg>
  TextPositionType = 0
  WayPoints = (2) [(0,0,0),(50,0,0)]
  WayPointsType = 0
  X = 149.382
  Y = 95
FEATURE [TechDraw::DrawViewSymbolPython] ReinforcementDimensioning030  # drawing view (typed FeaturePython)
  DimensionBottomOffset = 10
  DimensionFormat = %M %C⌀%D,span=%S
  DimensionLeftOffset = 10
  DimensionRightOffset = 16
  DimensionTopOffset = 28
  Font = DejaVu Sans
  FontSize = 3
  LineEndSymbol = 0
  LineMidPointSymbol = 1
  LineStartSymbol = 3
  LineStyle = 0
  LockPosition = false
  MultiRebar_LineEndSymbol = 0
  MultiRebar_LineStartSymbol = 0
  MultiRebar_OuterDimension = true
  MultiRebar_TextPositionType = 0
  ParentDrawingView = -> ReinforcementDrawingView002
  Rebar = -> Rebar019
  Rotation = 0
  Scale = 0.1
  ScaleType = 2
  SingleRebar_LineEndSymbol = 0
  SingleRebar_LineStartSymbol = 3
  SingleRebar_OuterDimension = false
  SingleRebar_TextPositionType = 1
  StrokeWidth = 0.25
  Symbol = <svg version="1.1" xmlns="http://www.w3.org/2000/svg" xmlns:xlink="http://www.w3.org/1999/xlink" xmlns:freecad="http://www.freecadweb.org/wiki/index.php?title=Svg_Namespace" width="300.0mm" height="1700.0mm" viewBox="0 0 300.0 1700.0"><g transform="translate(150.0, 1600.0)"><g><path d="M-114.0 -1880.0 L-114.0 -1592.0" style="stroke:#00007f;stroke-width:2.5;stroke-linecap:round;fill:none;" stroke-dasharray="" /><g id="line_mid_points" /><path d="M0,0 -8,-1.5 V1.5 L0,0" style="stroke:#00007f;fill:#00007f;stroke-width:2.5;stroke-linecap:round;stroke-linejoin:bevel;" transform="translate(-114.0 -1592.0) rotate(90.0 0 0)" /></g><text x="-114.0" y="-1880.0" style="white-space:pre;" fill="#005400" font-family="DejaVu Sans" font-size="30.0" text-anchor="middle" dominant-baseline="baseline" xml:space="preserve">XD 1⌀16,span=0</text></g></svg>
  TextPositionType = 0
  WayPoints = (2) [(0,0,0),(50,0,0)]
  WayPointsType = 0
  X = 149.382
  Y = 95
FEATURE [TechDraw::DrawViewSymbolPython] ReinforcementDimensioning031  # drawing view (typed FeaturePython)
  DimensionBottomOffset = 10
  DimensionFormat = %M %C⌀%D,span=%S
  DimensionLeftOffset = 10
  DimensionRightOffset = 16
  DimensionTopOffset = 34
  Font = DejaVu Sans
  FontSize = 3
  LineEndSymbol = 0
  LineMidPointSymbol = 1
  LineStartSymbol = 3
  LineStyle = 0
  LockPosition = false
  MultiRebar_LineEndSymbol = 0
  MultiRebar_LineStartSymbol = 0
  MultiRebar_OuterDimension = true
  MultiRebar_TextPositionType = 0
  ParentDrawingView = -> ReinforcementDrawingView002
  Rebar = -> Rebar021
  Rotation = 0
  Scale = 0.1
  ScaleType = 2
  SingleRebar_LineEndSymbol = 0
  SingleRebar_LineStartSymbol = 3
  SingleRebar_OuterDimension = false
  SingleRebar_TextPositionType = 1
  StrokeWidth = 0.25
  Symbol = <svg version="1.1" xmlns="http://www.w3.org/2000/svg" xmlns:xlink="http://www.w3.org/1999/xlink" xmlns:freecad="http://www.freecadweb.org/wiki/index.php?title=Svg_Namespace" width="300.0mm" height="1700.0mm" viewBox="0 0 300.0 1700.0"><g transform="translate(150.0, 1600.0)"><g><path d="M310.0 -368.0 L44.99999999999993 -368.0" style="stroke:#00007f;stroke-width:2.5;stroke-linecap:round;fill:none;" stroke-dasharray="" /><g id="line_mid_points" /><path d="M0,0 -8,-1.5 V1.5 L0,0" style="stroke:#00007f;fill:#00007f;stroke-width:2.5;stroke-linecap:round;stroke-linejoin:bevel;" transform="translate(44.99999999999993 -368.0) rotate(180.0 0 0)" /></g><text x="310.0" y="-353.0" style="white-space:pre;" fill="#005400" font-family="DejaVu Sans" font-size="30.0" text-anchor="start" dominant-baseline="baseline" xml:space="preserve">YD 1⌀20,span=0</text></g></svg>
  TextPositionType = 0
  WayPoints = (2) [(0,0,0),(50,0,0)]
  WayPointsType = 0
  X = 149.382
  Y = 95
FEATURE [TechDraw::DrawViewSymbolPython] ReinforcementDimensioning032  # drawing view (typed FeaturePython)
  DimensionBottomOffset = 10
  DimensionFormat = %M %C⌀%D,span=%S
  DimensionLeftOffset = 10
  DimensionRightOffset = 22
  DimensionTopOffset = 34
  Font = DejaVu Sans
  FontSize = 3
  LineEndSymbol = 0
  LineMidPointSymbol = 1
  LineStartSymbol = 3
  LineStyle = 0
  LockPosition = false
  MultiRebar_LineEndSymbol = 0
  MultiRebar_LineStartSymbol = 0
  MultiRebar_OuterDimension = true
  MultiRebar_TextPositionType = 0
  ParentDrawingView = -> ReinforcementDrawingView002
  Rebar = -> Rebar022
  Rotation = 0
  Scale = 0.1
  ScaleType = 2
  SingleRebar_LineEndSymbol = 0
  SingleRebar_LineStartSymbol = 3
  SingleRebar_OuterDimension = false
  SingleRebar_TextPositionType = 1
  StrokeWidth = 0.25
  Symbol = <svg version="1.1" xmlns="http://www.w3.org/2000/svg" xmlns:xlink="http://www.w3.org/1999/xlink" xmlns:freecad="http://www.freecadweb.org/wiki/index.php?title=Svg_Namespace" width="300.0mm" height="1700.0mm" viewBox="0 0 300.0 1700.0"><g transform="translate(150.0, 1600.0)"><g><path d="M-250.0 -625.0 L-1.6090517413347518e-13 -625.0" style="stroke:#00007f;stroke-width:2.5;stroke-linecap:round;fill:none;" stroke-dasharray="" /><g id="line_mid_points" /><path d="M0,0 -8,-1.5 V1.5 L0,0" style="stroke:#00007f;fill:#00007f;stroke-width:2.5;stroke-linecap:round;stroke-linejoin:bevel;" transform="translate(-1.6090517413347518e-13 -625.0) rotate(0.0 0 0)" /></g><text x="-250.0" y="-610.0" style="white-space:pre;" fill="#005400" font-family="DejaVu Sans" font-size="30.0" text-anchor="end" dominant-baseline="baseline" xml:space="preserve">YD 1⌀16,span=0</text></g></svg>
  TextPositionType = 0
  WayPoints = (2) [(0,0,0),(50,0,0)]
  WayPointsType = 0
  X = 149.382
  Y = 95
FEATURE [TechDraw::DrawViewSymbolPython] ReinforcementDimensioning033  # drawing view (typed FeaturePython)
  DimensionBottomOffset = 10
  DimensionFormat = %M %C⌀%D,span=%S
  DimensionLeftOffset = 16
  DimensionRightOffset = 22
  DimensionTopOffset = 34
  Font = DejaVu Sans
  FontSize = 3
  LineEndSymbol = 0
  LineMidPointSymbol = 1
  LineStartSymbol = 3
  LineStyle = 0
  LockPosition = false
  MultiRebar_LineEndSymbol = 0
  MultiRebar_LineStartSymbol = 0
  MultiRebar_OuterDimension = true
  MultiRebar_TextPositionType = 0
  ParentDrawingView = -> ReinforcementDrawingView002
  Rebar = -> Rebar023
  Rotation = 0
  Scale = 0.1
  ScaleType = 2
  SingleRebar_LineEndSymbol = 0
  SingleRebar_LineStartSymbol = 3
  SingleRebar_OuterDimension = false
  SingleRebar_TextPositionType = 1
  StrokeWidth = 0.25
  Symbol = <svg version="1.1" xmlns="http://www.w3.org/2000/svg" xmlns:xlink="http://www.w3.org/1999/xlink" xmlns:freecad="http://www.freecadweb.org/wiki/index.php?title=Svg_Namespace" width="300.0mm" height="1700.0mm" viewBox="0 0 300.0 1700.0"><g transform="translate(150.0, 1600.0)"><g><path d="M-310.0 -347.0 L-45.000000000000064 -347.0" style="stroke:#00007f;stroke-width:2.5;stroke-linecap:round;fill:none;" stroke-dasharray="" /><g id="line_mid_points" /><path d="M0,0 -8,-1.5 V1.5 L0,0" style="stroke:#00007f;fill:#00007f;stroke-width:2.5;stroke-linecap:round;stroke-linejoin:bevel;" transform="translate(-45.000000000000064 -347.0) rotate(0.0 0 0)" /></g><text x="-310.0" y="-332.0" style="white-space:pre;" fill="#005400" font-family="DejaVu Sans" font-size="30.0" text-anchor="end" dominant-baseline="baseline" xml:space="preserve">YD 1⌀20,span=0</text></g></svg>
  TextPositionType = 0
  WayPoints = (2) [(0,0,0),(50,0,0)]
  WayPointsType = 0
  X = 149.382
  Y = 95
FEATURE [TechDraw::DrawViewSymbolPython] ReinforcementDimensioning034  # drawing view (typed FeaturePython)
  DimensionBottomOffset = 10
  DimensionFormat = %M %C⌀%D,span=%S
  DimensionLeftOffset = 22
  DimensionRightOffset = 22
  DimensionTopOffset = 34
  Font = DejaVu Sans
  FontSize = 3
  LineEndSymbol = 0
  LineMidPointSymbol = 1
  LineStartSymbol = 3
  LineStyle = 0
  LockPosition = false
  MultiRebar_LineEndSymbol = 0
  MultiRebar_LineStartSymbol = 0
  MultiRebar_OuterDimension = true
  MultiRebar_TextPositionType = 0
  ParentDrawingView = -> ReinforcementDrawingView002
  Rebar = -> Rebar024
  Rotation = 0
  Scale = 0.1
  ScaleType = 2
  SingleRebar_LineEndSymbol = 0
  SingleRebar_LineStartSymbol = 3
  SingleRebar_OuterDimension = false
  SingleRebar_TextPositionType = 1
  StrokeWidth = 0.25
  Symbol = <svg version="1.1" xmlns="http://www.w3.org/2000/svg" xmlns:xlink="http://www.w3.org/1999/xlink" xmlns:freecad="http://www.freecadweb.org/wiki/index.php?title=Svg_Namespace" width="300.0mm" height="1700.0mm" viewBox="0 0 300.0 1700.0"><g transform="translate(150.0, 1600.0)"><g><path d="M370.0 -142.0 L44.99999999999998 -142.0" style="stroke:#00007f;stroke-width:2.5;stroke-linecap:round;fill:none;" stroke-dasharray="" /><g id="line_mid_points" /><path d="M0,0 -8,-1.5 V1.5 L0,0" style="stroke:#00007f;fill:#00007f;stroke-width:2.5;stroke-linecap:round;stroke-linejoin:bevel;" transform="translate(44.99999999999998 -142.0) rotate(180.0 0 0)" /></g><text x="370.0" y="-127.0" style="white-space:pre;" fill="#005400" font-family="DejaVu Sans" font-size="30.0" text-anchor="start" dominant-baseline="baseline" xml:space="preserve">YD 1⌀20,span=0</text></g></svg>
  TextPositionType = 0
  WayPoints = (2) [(0,0,0),(50,0,0)]
  WayPointsType = 0
  X = 149.382
  Y = 95
FEATURE [TechDraw::DrawViewSymbolPython] ReinforcementDimensioning035  # drawing view (typed FeaturePython)
  DimensionBottomOffset = 10
  DimensionFormat = %M %C⌀%D,span=%S
  DimensionLeftOffset = 22
  DimensionRightOffset = 28
  DimensionTopOffset = 34
  Font = DejaVu Sans
  FontSize = 3
  LineEndSymbol = 0
  LineMidPointSymbol = 1
  LineStartSymbol = 3
  LineStyle = 0
  LockPosition = false
  MultiRebar_LineEndSymbol = 0
  MultiRebar_LineStartSymbol = 0
  MultiRebar_OuterDimension = true
  MultiRebar_TextPositionType = 0
  ParentDrawingView = -> ReinforcementDrawingView002
  Rebar = -> Rebar025
  Rotation = 0
  Scale = 0.1
  ScaleType = 2
  SingleRebar_LineEndSymbol = 0
  SingleRebar_LineStartSymbol = 3
  SingleRebar_OuterDimension = false
  SingleRebar_TextPositionType = 1
  StrokeWidth = 0.25
  Symbol = <svg version="1.1" xmlns="http://www.w3.org/2000/svg" xmlns:xlink="http://www.w3.org/1999/xlink" xmlns:freecad="http://www.freecadweb.org/wiki/index.php?title=Svg_Namespace" width="300.0mm" height="1700.0mm" viewBox="0 0 300.0 1700.0"><g transform="translate(150.0, 1600.0)"><g><path d="M-370.0 -799.0 L-1.9305597309907404e-13 -799.0" style="stroke:#00007f;stroke-width:2.5;stroke-linecap:round;fill:none;" stroke-dasharray="" /><g id="line_mid_points" /><path d="M0,0 -8,-1.5 V1.5 L0,0" style="stroke:#00007f;fill:#00007f;stroke-width:2.5;stroke-linecap:round;stroke-linejoin:bevel;" transform="translate(-1.9305597309907404e-13 -799.0) rotate(0.0 0 0)" /></g><text x="-370.0" y="-784.0" style="white-space:pre;" fill="#005400" font-family="DejaVu Sans" font-size="30.0" text-anchor="end" dominant-baseline="baseline" xml:space="preserve">YD 1⌀16,span=0</text></g></svg>
  TextPositionType = 0
  WayPoints = (2) [(0,0,0),(50,0,0)]
  WayPointsType = 0
  X = 149.382
  Y = 95
FEATURE [TechDraw::DrawViewSymbolPython] ReinforcementDimensioning036  # drawing view (typed FeaturePython)
  DimensionBottomOffset = 10
  DimensionFormat = %M %C⌀%D,span=%S
  DimensionLeftOffset = 28
  DimensionRightOffset = 28
  DimensionTopOffset = 34
  Font = DejaVu Sans
  FontSize = 3
  LineEndSymbol = 0
  LineMidPointSymbol = 1
  LineStartSymbol = 3
  LineStyle = 0
  LockPosition = false
  MultiRebar_LineEndSymbol = 0
  MultiRebar_LineStartSymbol = 0
  MultiRebar_OuterDimension = true
  MultiRebar_TextPositionType = 0
  ParentDrawingView = -> ReinforcementDrawingView002
  Rebar = -> Rebar026
  Rotation = 0
  Scale = 0.1
  ScaleType = 2
  SingleRebar_LineEndSymbol = 0
  SingleRebar_LineStartSymbol = 3
  SingleRebar_OuterDimension = false
  SingleRebar_TextPositionType = 1
  StrokeWidth = 0.25
  Symbol = <svg version="1.1" xmlns="http://www.w3.org/2000/svg" xmlns:xlink="http://www.w3.org/1999/xlink" xmlns:freecad="http://www.freecadweb.org/wiki/index.php?title=Svg_Namespace" width="300.0mm" height="1700.0mm" viewBox="0 0 300.0 1700.0"><g transform="translate(150.0, 1600.0)"><g><path d="M-430.0 -539.0 L-45.00000000000011 -539.0" style="stroke:#00007f;stroke-width:2.5;stroke-linecap:round;fill:none;" stroke-dasharray="" /><g id="line_mid_points" /><path d="M0,0 -8,-1.5 V1.5 L0,0" style="stroke:#00007f;fill:#00007f;stroke-width:2.5;stroke-linecap:round;stroke-linejoin:bevel;" transform="translate(-45.00000000000011 -539.0) rotate(0.0 0 0)" /></g><text x="-430.0" y="-524.0" style="white-space:pre;" fill="#005400" font-family="DejaVu Sans" font-size="30.0" text-anchor="end" dominant-baseline="baseline" xml:space="preserve">YD 1⌀20,span=0</text></g></svg>
  TextPositionType = 0
  WayPoints = (2) [(0,0,0),(50,0,0)]
  WayPointsType = 0
  X = 149.382
  Y = 95
FEATURE [TechDraw::DrawViewSymbolPython] ReinforcementDimensioning037  # drawing view (typed FeaturePython)
  DimensionBottomOffset = 10
  DimensionFormat = %M %C⌀%D,span=%S
  DimensionLeftOffset = 34
  DimensionRightOffset = 28
  DimensionTopOffset = 34
  Font = DejaVu Sans
  FontSize = 3
  LineEndSymbol = 0
  LineMidPointSymbol = 1
  LineStartSymbol = 3
  LineStyle = 0
  LockPosition = false
  MultiRebar_LineEndSymbol = 0
  MultiRebar_LineStartSymbol = 0
  MultiRebar_OuterDimension = true
  MultiRebar_TextPositionType = 0
  ParentDrawingView = -> ReinforcementDrawingView002
  Rebar = -> Rebar
  Rotation = 0
  Scale = 0.1
  ScaleType = 2
  SingleRebar_LineEndSymbol = 0
  SingleRebar_LineStartSymbol = 3
  SingleRebar_OuterDimension = false
  SingleRebar_TextPositionType = 1
  StrokeWidth = 0.25
  Symbol = <svg version="1.1" xmlns="http://www.w3.org/2000/svg" xmlns:xlink="http://www.w3.org/1999/xlink" xmlns:freecad="http://www.freecadweb.org/wiki/index.php?title=Svg_Namespace" width="300.0mm" height="1700.0mm" viewBox="0 0 300.0 1700.0"><g transform="translate(150.0, 1600.0)"><g><path d="M91.99999999999966 -1890.0 L91.99999999999966 -1940.0 L-92.00000000000068 -1940.0 L-92.00000000000068 -1890.0" style="stroke:#00007f;stroke-width:2.5;stroke-linecap:round;fill:none;" stroke-dasharray="" /><path d="M0,0 -8,-1.5 V1.5 L0,0" style="stroke:#00007f;fill:#00007f;stroke-width:2.5;stroke-linecap:round;stroke-linejoin:bevel;" transform="translate(91.99999999999966 -1890.0) rotate(90.0 0 0)" /><g id="line_mid_points"><circle cx="0" cy="0" r="5.0" fill="#00007f" transform="translate(91.99999999999966 -1940.0) rotate(-90.0 0 0)" /><circle cx="0" cy="0" r="5.0" fill="#00007f" transform="translate(-92.00000000000068 -1940.0) rotate(180.0 0 0)" /></g><path d="M0,0 -8,-1.5 V1.5 L0,0" style="stroke:#00007f;fill:#00007f;stroke-width:2.5;stroke-linecap:round;stroke-linejoin:bevel;" transform="translate(-92.00000000000068 -1890.0) rotate(90.0 0 0)" /></g><text x="-5.115907697472721e-13" y="-1945.0" style="white-space:pre;" fill="#005400" font-family="DejaVu Sans" font-size="30.0" text-anchor="middle" dominant-baseline="baseline" xml:space="preserve" transform="rotate(-0.0 -5.115907697472721e-13 -1940.0)">M 2⌀20,span=184</text></g></svg>
  TextPositionType = 0
  WayPoints = (2) [(0,0,0),(50,0,0)]
  WayPointsType = 0
  X = 149.382
  Y = 95
FEATURE [TechDraw::DrawPage] TechDraw__DrawPage002  label="Column Drawing002"
  KeepUpdated = true
  NextBalloonIndex = 1
  ProjectionType = 0
  Template = -> Template002
  Views = -> [ReinforcementDrawingView002,ReinforcementDimensioning026,ReinforcementDimensioning027,ReinforcementDimensioning028,ReinforcementDimensioning029,ReinforcementDimensioning030,ReinforcementDimensioning031,ReinforcementDimensioning032,ReinforcementDimensioning033,ReinforcementDimensioning034,ReinforcementDimensioning035,ReinforcementDimensioning036,ReinforcementDimensioning037]
FEATURE [TechDraw::DrawSVGTemplate] Template003
  Height = 210
  Orientation = 1
  Width = 297
FEATURE [TechDraw::DrawViewSymbolPython] ReinforcementDrawingView003  label="Right View"  # drawing view (typed FeaturePython)
  DimensionBottomOffset = 10
  DimensionLeftOffset = 34
  DimensionRightOffset = 28
  DimensionTopOffset = 40
  Height = 1700
  LeftOffset = 134.382
  LockPosition = false
  MaxHeight = 210
  MaxWidth = 297
  MinBottomOffset = 10
  MinRightOffset = 20
  PositionType = 0
  Rebars = -> [Rebar,Rebar001,Rebar002,Rebar015,Rebar016,Rebar017,Rebar018,Rebar019,Rebar020,Rebar021,Rebar022,Rebar023,Rebar024,Rebar025,Rebar026]
  RebarsColorStyle = 0
  RebarsStrokeWidth = 0.35
  Rotation = 0
  Scale = 0.1
  ScaleType = 1
  Structure = -> Structure
  StructureColorStyle = 0
  StructureStrokeWidth = 0.5
  Symbol = <blob: 6614 chars omitted>
  Template = -> Template003
  TopOffset = 30
  View = 3
  VisibleRebars = -> [Rebar002,Rebar015,Rebar016,Rebar018,Rebar019,Rebar021,Rebar022,Rebar023,Rebar024,Rebar025,Rebar026,Rebar]
  Width = 300
  X = 149.382
  Y = 95
  expr: LeftOffset = .Template.Width.Value / 2 - .Width.Value * .Scale / 2
FEATURE [TechDraw::DrawViewSymbolPython] ReinforcementDimensioning038  # drawing view (typed FeaturePython)
  DimensionBottomOffset = 10
  DimensionFormat = %M %C⌀%D,span=%S
  DimensionLeftOffset = 10
  DimensionRightOffset = 10
  DimensionTopOffset = 10
  Font = DejaVu Sans
  FontSize = 3
  LineEndSymbol = 0
  LineMidPointSymbol = 1
  LineStartSymbol = 3
  LineStyle = 0
  LockPosition = false
  MultiRebar_LineEndSymbol = 0
  MultiRebar_LineStartSymbol = 0
  MultiRebar_OuterDimension = true
  MultiRebar_TextPositionType = 0
  ParentDrawingView = -> ReinforcementDrawingView003
  Rebar = -> Rebar002
  Rotation = 0
  Scale = 0.1
  ScaleType = 2
  SingleRebar_LineEndSymbol = 0
  SingleRebar_LineStartSymbol = 3
  SingleRebar_OuterDimension = false
  SingleRebar_TextPositionType = 1
  StrokeWidth = 0.25
  Symbol = <blob: 4599 chars omitted>
  TextPositionType = 0
  WayPoints = (2) [(0,0,0),(50,0,0)]
  WayPointsType = 0
  X = 149.382
  Y = 95
FEATURE [TechDraw::DrawViewSymbolPython] ReinforcementDimensioning039  # drawing view (typed FeaturePython)
  DimensionBottomOffset = 10
  DimensionFormat = %M %C⌀%D,span=%S
  DimensionLeftOffset = 10
  DimensionRightOffset = 16
  DimensionTopOffset = 10
  Font = DejaVu Sans
  FontSize = 3
  LineEndSymbol = 0
  LineMidPointSymbol = 1
  LineStartSymbol = 3
  LineStyle = 0
  LockPosition = false
  MultiRebar_LineEndSymbol = 0
  MultiRebar_LineStartSymbol = 0
  MultiRebar_OuterDimension = true
  MultiRebar_TextPositionType = 0
  ParentDrawingView = -> ReinforcementDrawingView003
  Rebar = -> Rebar015
  Rotation = 0
  Scale = 0.1
  ScaleType = 2
  SingleRebar_LineEndSymbol = 0
  SingleRebar_LineStartSymbol = 3
  SingleRebar_OuterDimension = false
  SingleRebar_TextPositionType = 1
  StrokeWidth = 0.25
  Symbol = <svg version="1.1" xmlns="http://www.w3.org/2000/svg" xmlns:xlink="http://www.w3.org/1999/xlink" xmlns:freecad="http://www.freecadweb.org/wiki/index.php?title=Svg_Namespace" width="300.0mm" height="1700.0mm" viewBox="0 0 300.0 1700.0"><g transform="translate(150.0, 1600.0)"><g><path d="M-112.0 -1700.0 L-112.0 -1590.0" style="stroke:#00007f;stroke-width:2.5;stroke-linecap:round;fill:none;" stroke-dasharray="" /><g id="line_mid_points" /><path d="M0,0 -8,-1.5 V1.5 L0,0" style="stroke:#00007f;fill:#00007f;stroke-width:2.5;stroke-linecap:round;stroke-linejoin:bevel;" transform="translate(-112.0 -1590.0) rotate(90.0 0 0)" /></g><text x="-112.0" y="-1700.0" style="white-space:pre;" fill="#005400" font-family="DejaVu Sans" font-size="30.0" text-anchor="middle" dominant-baseline="baseline" xml:space="preserve">XD 2⌀20,span=31</text></g></svg>
  TextPositionType = 0
  WayPoints = (2) [(0,0,0),(50,0,0)]
  WayPointsType = 0
  X = 149.382
  Y = 95
FEATURE [TechDraw::DrawViewSymbolPython] ReinforcementDimensioning040  # drawing view (typed FeaturePython)
  DimensionBottomOffset = 10
  DimensionFormat = %M %C⌀%D,span=%S
  DimensionLeftOffset = 10
  DimensionRightOffset = 16
  DimensionTopOffset = 16
  Font = DejaVu Sans
  FontSize = 3
  LineEndSymbol = 0
  LineMidPointSymbol = 1
  LineStartSymbol = 3
  LineStyle = 0
  LockPosition = false
  MultiRebar_LineEndSymbol = 0
  MultiRebar_LineStartSymbol = 0
  MultiRebar_OuterDimension = true
  MultiRebar_TextPositionType = 0
  ParentDrawingView = -> ReinforcementDrawingView003
  Rebar = -> Rebar016
  Rotation = 0
  Scale = 0.1
  ScaleType = 2
  SingleRebar_LineEndSymbol = 0
  SingleRebar_LineStartSymbol = 3
  SingleRebar_OuterDimension = false
  SingleRebar_TextPositionType = 1
  StrokeWidth = 0.25
  Symbol = <svg version="1.1" xmlns="http://www.w3.org/2000/svg" xmlns:xlink="http://www.w3.org/1999/xlink" xmlns:freecad="http://www.freecadweb.org/wiki/index.php?title=Svg_Namespace" width="300.0mm" height="1700.0mm" viewBox="0 0 300.0 1700.0"><g transform="translate(150.0, 1600.0)"><g><path d="M-131.0 -1760.0 L-131.0 -1592.0" style="stroke:#00007f;stroke-width:2.5;stroke-linecap:round;fill:none;" stroke-dasharray="" /><g id="line_mid_points" /><path d="M0,0 -8,-1.5 V1.5 L0,0" style="stroke:#00007f;fill:#00007f;stroke-width:2.5;stroke-linecap:round;stroke-linejoin:bevel;" transform="translate(-131.0 -1592.0) rotate(90.0 0 0)" /></g><text x="-131.0" y="-1760.0" style="white-space:pre;" fill="#005400" font-family="DejaVu Sans" font-size="30.0" text-anchor="middle" dominant-baseline="baseline" xml:space="preserve">XD 1⌀16,span=0</text></g></svg>
  TextPositionType = 0
  WayPoints = (2) [(0,0,0),(50,0,0)]
  WayPointsType = 0
  X = 149.382
  Y = 95
FEATURE [TechDraw::DrawViewSymbolPython] ReinforcementDimensioning041  # drawing view (typed FeaturePython)
  DimensionBottomOffset = 10
  DimensionFormat = %M %C⌀%D,span=%S
  DimensionLeftOffset = 10
  DimensionRightOffset = 16
  DimensionTopOffset = 22
  Font = DejaVu Sans
  FontSize = 3
  LineEndSymbol = 0
  LineMidPointSymbol = 1
  LineStartSymbol = 3
  LineStyle = 0
  LockPosition = false
  MultiRebar_LineEndSymbol = 0
  MultiRebar_LineStartSymbol = 0
  MultiRebar_OuterDimension = true
  MultiRebar_TextPositionType = 0
  ParentDrawingView = -> ReinforcementDrawingView003
  Rebar = -> Rebar018
  Rotation = 0
  Scale = 0.1
  ScaleType = 2
  SingleRebar_LineEndSymbol = 0
  SingleRebar_LineStartSymbol = 3
  SingleRebar_OuterDimension = false
  SingleRebar_TextPositionType = 1
  StrokeWidth = 0.25
  Symbol = <svg version="1.1" xmlns="http://www.w3.org/2000/svg" xmlns:xlink="http://www.w3.org/1999/xlink" xmlns:freecad="http://www.freecadweb.org/wiki/index.php?title=Svg_Namespace" width="300.0mm" height="1700.0mm" viewBox="0 0 300.0 1700.0"><g transform="translate(150.0, 1600.0)"><g><path d="M135.0 -1820.0 L135.0 -1590.0" style="stroke:#00007f;stroke-width:2.5;stroke-linecap:round;fill:none;" stroke-dasharray="" /><g id="line_mid_points" /><path d="M0,0 -8,-1.5 V1.5 L0,0" style="stroke:#00007f;fill:#00007f;stroke-width:2.5;stroke-linecap:round;stroke-linejoin:bevel;" transform="translate(135.0 -1590.0) rotate(90.0 0 0)" /></g><text x="135.0" y="-1820.0" style="white-space:pre;" fill="#005400" font-family="DejaVu Sans" font-size="30.0" text-anchor="middle" dominant-baseline="baseline" xml:space="preserve">XD 2⌀20,span=31</text></g></svg>
  TextPositionType = 0
  WayPoints = (2) [(0,0,0),(50,0,0)]
  WayPointsType = 0
  X = 149.382
  Y = 95
FEATURE [TechDraw::DrawViewSymbolPython] ReinforcementDimensioning042  # drawing view (typed FeaturePython)
  DimensionBottomOffset = 10
  DimensionFormat = %M %C⌀%D,span=%S
  DimensionLeftOffset = 10
  DimensionRightOffset = 16
  DimensionTopOffset = 28
  Font = DejaVu Sans
  FontSize = 3
  LineEndSymbol = 0
  LineMidPointSymbol = 1
  LineStartSymbol = 3
  LineStyle = 0
  LockPosition = false
  MultiRebar_LineEndSymbol = 0
  MultiRebar_LineStartSymbol = 0
  MultiRebar_OuterDimension = true
  MultiRebar_TextPositionType = 0
  ParentDrawingView = -> ReinforcementDrawingView003
  Rebar = -> Rebar019
  Rotation = 0
  Scale = 0.1
  ScaleType = 2
  SingleRebar_LineEndSymbol = 0
  SingleRebar_LineStartSymbol = 3
  SingleRebar_OuterDimension = false
  SingleRebar_TextPositionType = 1
  StrokeWidth = 0.25
  Symbol = <svg version="1.1" xmlns="http://www.w3.org/2000/svg" xmlns:xlink="http://www.w3.org/1999/xlink" xmlns:freecad="http://www.freecadweb.org/wiki/index.php?title=Svg_Namespace" width="300.0mm" height="1700.0mm" viewBox="0 0 300.0 1700.0"><g transform="translate(150.0, 1600.0)"><g><path d="M108.0 -1880.0 L108.0 -1592.0" style="stroke:#00007f;stroke-width:2.5;stroke-linecap:round;fill:none;" stroke-dasharray="" /><g id="line_mid_points" /><path d="M0,0 -8,-1.5 V1.5 L0,0" style="stroke:#00007f;fill:#00007f;stroke-width:2.5;stroke-linecap:round;stroke-linejoin:bevel;" transform="translate(108.0 -1592.0) rotate(90.0 0 0)" /></g><text x="108.0" y="-1880.0" style="white-space:pre;" fill="#005400" font-family="DejaVu Sans" font-size="30.0" text-anchor="middle" dominant-baseline="baseline" xml:space="preserve">XD 1⌀16,span=0</text></g></svg>
  TextPositionType = 0
  WayPoints = (2) [(0,0,0),(50,0,0)]
  WayPointsType = 0
  X = 149.382
  Y = 95
FEATURE [TechDraw::DrawViewSymbolPython] ReinforcementDimensioning043  # drawing view (typed FeaturePython)
  DimensionBottomOffset = 10
  DimensionFormat = %M %C⌀%D,span=%S
  DimensionLeftOffset = 10
  DimensionRightOffset = 16
  DimensionTopOffset = 34
  Font = DejaVu Sans
  FontSize = 3
  LineEndSymbol = 0
  LineMidPointSymbol = 1
  LineStartSymbol = 3
  LineStyle = 0
  LockPosition = false
  MultiRebar_LineEndSymbol = 0
  MultiRebar_LineStartSymbol = 0
  MultiRebar_OuterDimension = true
  MultiRebar_TextPositionType = 0
  ParentDrawingView = -> ReinforcementDrawingView003
  Rebar = -> Rebar021
  Rotation = 0
  Scale = 0.1
  ScaleType = 2
  SingleRebar_LineEndSymbol = 0
  SingleRebar_LineStartSymbol = 3
  SingleRebar_OuterDimension = false
  SingleRebar_TextPositionType = 1
  StrokeWidth = 0.25
  Symbol = <svg version="1.1" xmlns="http://www.w3.org/2000/svg" xmlns:xlink="http://www.w3.org/1999/xlink" xmlns:freecad="http://www.freecadweb.org/wiki/index.php?title=Svg_Namespace" width="300.0mm" height="1700.0mm" viewBox="0 0 300.0 1700.0"><g transform="translate(150.0, 1600.0)"><g><path d="M-250.0 79.0 L-45.00000000000003 79.0" style="stroke:#00007f;stroke-width:2.5;stroke-linecap:round;fill:none;" stroke-dasharray="" /><g id="line_mid_points" /><path d="M0,0 -8,-1.5 V1.5 L0,0" style="stroke:#00007f;fill:#00007f;stroke-width:2.5;stroke-linecap:round;stroke-linejoin:bevel;" transform="translate(-45.00000000000003 79.0) rotate(0.0 0 0)" /></g><text x="-250.0" y="94.0" style="white-space:pre;" fill="#005400" font-family="DejaVu Sans" font-size="30.0" text-anchor="end" dominant-baseline="baseline" xml:space="preserve">YD 1⌀20,span=0</text></g></svg>
  TextPositionType = 0
  WayPoints = (2) [(0,0,0),(50,0,0)]
  WayPointsType = 0
  X = 149.382
  Y = 95
FEATURE [TechDraw::DrawViewSymbolPython] ReinforcementDimensioning044  # drawing view (typed FeaturePython)
  DimensionBottomOffset = 10
  DimensionFormat = %M %C⌀%D,span=%S
  DimensionLeftOffset = 16
  DimensionRightOffset = 16
  DimensionTopOffset = 34
  Font = DejaVu Sans
  FontSize = 3
  LineEndSymbol = 0
  LineMidPointSymbol = 1
  LineStartSymbol = 3
  LineStyle = 0
  LockPosition = false
  MultiRebar_LineEndSymbol = 0
  MultiRebar_LineStartSymbol = 0
  MultiRebar_OuterDimension = true
  MultiRebar_TextPositionType = 0
  ParentDrawingView = -> ReinforcementDrawingView003
  Rebar = -> Rebar022
  Rotation = 0
  Scale = 0.1
  ScaleType = 2
  SingleRebar_LineEndSymbol = 0
  SingleRebar_LineStartSymbol = 3
  SingleRebar_OuterDimension = false
  SingleRebar_TextPositionType = 1
  StrokeWidth = 0.25
  Symbol = <svg version="1.1" xmlns="http://www.w3.org/2000/svg" xmlns:xlink="http://www.w3.org/1999/xlink" xmlns:freecad="http://www.freecadweb.org/wiki/index.php?title=Svg_Namespace" width="300.0mm" height="1700.0mm" viewBox="0 0 300.0 1700.0"><g transform="translate(150.0, 1600.0)"><g><path d="M-310.0 -260.0 L-9.346240618839712e-14 -260.0" style="stroke:#00007f;stroke-width:2.5;stroke-linecap:round;fill:none;" stroke-dasharray="" /><g id="line_mid_points" /><path d="M0,0 -8,-1.5 V1.5 L0,0" style="stroke:#00007f;fill:#00007f;stroke-width:2.5;stroke-linecap:round;stroke-linejoin:bevel;" transform="translate(-9.346240618839712e-14 -260.0) rotate(0.0 0 0)" /></g><text x="-310.0" y="-245.0" style="white-space:pre;" fill="#005400" font-family="DejaVu Sans" font-size="30.0" text-anchor="end" dominant-baseline="baseline" xml:space="preserve">YD 1⌀16,span=0</text></g></svg>
  TextPositionType = 0
  WayPoints = (2) [(0,0,0),(50,0,0)]
  WayPointsType = 0
  X = 149.382
  Y = 95
FEATURE [TechDraw::DrawViewSymbolPython] ReinforcementDimensioning045  # drawing view (typed FeaturePython)
  DimensionBottomOffset = 10
  DimensionFormat = %M %C⌀%D,span=%S
  DimensionLeftOffset = 22
  DimensionRightOffset = 16
  DimensionTopOffset = 34
  Font = DejaVu Sans
  FontSize = 3
  LineEndSymbol = 0
  LineMidPointSymbol = 1
  LineStartSymbol = 3
  LineStyle = 0
  LockPosition = false
  MultiRebar_LineEndSymbol = 0
  MultiRebar_LineStartSymbol = 0
  MultiRebar_OuterDimension = true
  MultiRebar_TextPositionType = 0
  ParentDrawingView = -> ReinforcementDrawingView003
  Rebar = -> Rebar023
  Rotation = 0
  Scale = 0.1
  ScaleType = 2
  SingleRebar_LineEndSymbol = 0
  SingleRebar_LineStartSymbol = 3
  SingleRebar_OuterDimension = false
  SingleRebar_TextPositionType = 1
  StrokeWidth = 0.25
  Symbol = <svg version="1.1" xmlns="http://www.w3.org/2000/svg" xmlns:xlink="http://www.w3.org/1999/xlink" xmlns:freecad="http://www.freecadweb.org/wiki/index.php?title=Svg_Namespace" width="300.0mm" height="1700.0mm" viewBox="0 0 300.0 1700.0"><g transform="translate(150.0, 1600.0)"><g><path d="M310.0 -237.0 L45.00000000000004 -237.0" style="stroke:#00007f;stroke-width:2.5;stroke-linecap:round;fill:none;" stroke-dasharray="" /><g id="line_mid_points" /><path d="M0,0 -8,-1.5 V1.5 L0,0" style="stroke:#00007f;fill:#00007f;stroke-width:2.5;stroke-linecap:round;stroke-linejoin:bevel;" transform="translate(45.00000000000004 -237.0) rotate(180.0 0 0)" /></g><text x="310.0" y="-222.0" style="white-space:pre;" fill="#005400" font-family="DejaVu Sans" font-size="30.0" text-anchor="start" dominant-baseline="baseline" xml:space="preserve">YD 1⌀20,span=0</text></g></svg>
  TextPositionType = 0
  WayPoints = (2) [(0,0,0),(50,0,0)]
  WayPointsType = 0
  X = 149.382
  Y = 95
FEATURE [TechDraw::DrawViewSymbolPython] ReinforcementDimensioning046  # drawing view (typed FeaturePython)
  DimensionBottomOffset = 10
  DimensionFormat = %M %C⌀%D,span=%S
  DimensionLeftOffset = 22
  DimensionRightOffset = 22
  DimensionTopOffset = 34
  Font = DejaVu Sans
  FontSize = 3
  LineEndSymbol = 0
  LineMidPointSymbol = 1
  LineStartSymbol = 3
  LineStyle = 0
  LockPosition = false
  MultiRebar_LineEndSymbol = 0
  MultiRebar_LineStartSymbol = 0
  MultiRebar_OuterDimension = true
  MultiRebar_TextPositionType = 0
  ParentDrawingView = -> ReinforcementDrawingView003
  Rebar = -> Rebar024
  Rotation = 0
  Scale = 0.1
  ScaleType = 2
  SingleRebar_LineEndSymbol = 0
  SingleRebar_LineStartSymbol = 3
  SingleRebar_OuterDimension = false
  SingleRebar_TextPositionType = 1
  StrokeWidth = 0.25
  Symbol = <svg version="1.1" xmlns="http://www.w3.org/2000/svg" xmlns:xlink="http://www.w3.org/1999/xlink" xmlns:freecad="http://www.freecadweb.org/wiki/index.php?title=Svg_Namespace" width="300.0mm" height="1700.0mm" viewBox="0 0 300.0 1700.0"><g transform="translate(150.0, 1600.0)"><g><path d="M-370.0 -958.0 L-44.9999999999998 -958.0" style="stroke:#00007f;stroke-width:2.5;stroke-linecap:round;fill:none;" stroke-dasharray="" /><g id="line_mid_points" /><path d="M0,0 -8,-1.5 V1.5 L0,0" style="stroke:#00007f;fill:#00007f;stroke-width:2.5;stroke-linecap:round;stroke-linejoin:bevel;" transform="translate(-44.9999999999998 -958.0) rotate(0.0 0 0)" /></g><text x="-370.0" y="-943.0" style="white-space:pre;" fill="#005400" font-family="DejaVu Sans" font-size="30.0" text-anchor="end" dominant-baseline="baseline" xml:space="preserve">YD 1⌀20,span=0</text></g></svg>
  TextPositionType = 0
  WayPoints = (2) [(0,0,0),(50,0,0)]
  WayPointsType = 0
  X = 149.382
  Y = 95
FEATURE [TechDraw::DrawViewSymbolPython] ReinforcementDimensioning047  # drawing view (typed FeaturePython)
  DimensionBottomOffset = 10
  DimensionFormat = %M %C⌀%D,span=%S
  DimensionLeftOffset = 28
  DimensionRightOffset = 22
  DimensionTopOffset = 34
  Font = DejaVu Sans
  FontSize = 3
  LineEndSymbol = 0
  LineMidPointSymbol = 1
  LineStartSymbol = 3
  LineStyle = 0
  LockPosition = false
  MultiRebar_LineEndSymbol = 0
  MultiRebar_LineStartSymbol = 0
  MultiRebar_OuterDimension = true
  MultiRebar_TextPositionType = 0
  ParentDrawingView = -> ReinforcementDrawingView003
  Rebar = -> Rebar025
  Rotation = 0
  Scale = 0.1
  ScaleType = 2
  SingleRebar_LineEndSymbol = 0
  SingleRebar_LineStartSymbol = 3
  SingleRebar_OuterDimension = false
  SingleRebar_TextPositionType = 1
  StrokeWidth = 0.25
  Symbol = <svg version="1.1" xmlns="http://www.w3.org/2000/svg" xmlns:xlink="http://www.w3.org/1999/xlink" xmlns:freecad="http://www.freecadweb.org/wiki/index.php?title=Svg_Namespace" width="300.0mm" height="1700.0mm" viewBox="0 0 300.0 1700.0"><g transform="translate(150.0, 1600.0)"><g><path d="M-430.0 -711.0 L-1.7679579890957576e-13 -711.0" style="stroke:#00007f;stroke-width:2.5;stroke-linecap:round;fill:none;" stroke-dasharray="" /><g id="line_mid_points" /><path d="M0,0 -8,-1.5 V1.5 L0,0" style="stroke:#00007f;fill:#00007f;stroke-width:2.5;stroke-linecap:round;stroke-linejoin:bevel;" transform="translate(-1.7679579890957576e-13 -711.0) rotate(0.0 0 0)" /></g><text x="-430.0" y="-696.0" style="white-space:pre;" fill="#005400" font-family="DejaVu Sans" font-size="30.0" text-anchor="end" dominant-baseline="baseline" xml:space="preserve">YD 1⌀16,span=0</text></g></svg>
  TextPositionType = 0
  WayPoints = (2) [(0,0,0),(50,0,0)]
  WayPointsType = 0
  X = 149.382
  Y = 95
FEATURE [TechDraw::DrawViewSymbolPython] ReinforcementDimensioning048  # drawing view (typed FeaturePython)
  DimensionBottomOffset = 10
  DimensionFormat = %M %C⌀%D,span=%S
  DimensionLeftOffset = 34
  DimensionRightOffset = 22
  DimensionTopOffset = 34
  Font = DejaVu Sans
  FontSize = 3
  LineEndSymbol = 0
  LineMidPointSymbol = 1
  LineStartSymbol = 3
  LineStyle = 0
  LockPosition = false
  MultiRebar_LineEndSymbol = 0
  MultiRebar_LineStartSymbol = 0
  MultiRebar_OuterDimension = true
  MultiRebar_TextPositionType = 0
  ParentDrawingView = -> ReinforcementDrawingView003
  Rebar = -> Rebar026
  Rotation = 0
  Scale = 0.1
  ScaleType = 2
  SingleRebar_LineEndSymbol = 0
  SingleRebar_LineStartSymbol = 3
  SingleRebar_OuterDimension = false
  SingleRebar_TextPositionType = 1
  StrokeWidth = 0.25
  Symbol = <svg version="1.1" xmlns="http://www.w3.org/2000/svg" xmlns:xlink="http://www.w3.org/1999/xlink" xmlns:freecad="http://www.freecadweb.org/wiki/index.php?title=Svg_Namespace" width="300.0mm" height="1700.0mm" viewBox="0 0 300.0 1700.0"><g transform="translate(150.0, 1600.0)"><g><path d="M370.0 -428.0 L45.000000000000085 -428.0" style="stroke:#00007f;stroke-width:2.5;stroke-linecap:round;fill:none;" stroke-dasharray="" /><g id="line_mid_points" /><path d="M0,0 -8,-1.5 V1.5 L0,0" style="stroke:#00007f;fill:#00007f;stroke-width:2.5;stroke-linecap:round;stroke-linejoin:bevel;" transform="translate(45.000000000000085 -428.0) rotate(180.0 0 0)" /></g><text x="370.0" y="-413.0" style="white-space:pre;" fill="#005400" font-family="DejaVu Sans" font-size="30.0" text-anchor="start" dominant-baseline="baseline" xml:space="preserve">YD 1⌀20,span=0</text></g></svg>
  TextPositionType = 0
  WayPoints = (2) [(0,0,0),(50,0,0)]
  WayPointsType = 0
  X = 149.382
  Y = 95
FEATURE [TechDraw::DrawViewSymbolPython] ReinforcementDimensioning049  # drawing view (typed FeaturePython)
  DimensionBottomOffset = 10
  DimensionFormat = %M %C⌀%D,span=%S
  DimensionLeftOffset = 34
  DimensionRightOffset = 28
  DimensionTopOffset = 34
  Font = DejaVu Sans
  FontSize = 3
  LineEndSymbol = 0
  LineMidPointSymbol = 1
  LineStartSymbol = 3
  LineStyle = 0
  LockPosition = false
  MultiRebar_LineEndSymbol = 0
  MultiRebar_LineStartSymbol = 0
  MultiRebar_OuterDimension = true
  MultiRebar_TextPositionType = 0
  ParentDrawingView = -> ReinforcementDrawingView003
  Rebar = -> Rebar
  Rotation = 0
  Scale = 0.1
  ScaleType = 2
  SingleRebar_LineEndSymbol = 0
  SingleRebar_LineStartSymbol = 3
  SingleRebar_OuterDimension = false
  SingleRebar_TextPositionType = 1
  StrokeWidth = 0.25
  Symbol = <svg version="1.1" xmlns="http://www.w3.org/2000/svg" xmlns:xlink="http://www.w3.org/1999/xlink" xmlns:freecad="http://www.freecadweb.org/wiki/index.php?title=Svg_Namespace" width="300.0mm" height="1700.0mm" viewBox="0 0 300.0 1700.0"><g transform="translate(150.0, 1600.0)"><g><path d="M-91.99999999999966 -1890.0 L-91.99999999999966 -1940.0 L92.00000000000068 -1940.0 L92.00000000000068 -1890.0" style="stroke:#00007f;stroke-width:2.5;stroke-linecap:round;fill:none;" stroke-dasharray="" /><path d="M0,0 -8,-1.5 V1.5 L0,0" style="stroke:#00007f;fill:#00007f;stroke-width:2.5;stroke-linecap:round;stroke-linejoin:bevel;" transform="translate(-91.99999999999966 -1890.0) rotate(90.0 0 0)" /><g id="line_mid_points"><circle cx="0" cy="0" r="5.0" fill="#00007f" transform="translate(-91.99999999999966 -1940.0) rotate(-90.0 0 0)" /><circle cx="0" cy="0" r="5.0" fill="#00007f" transform="translate(92.00000000000068 -1940.0) rotate(0.0 0 0)" /></g><path d="M0,0 -8,-1.5 V1.5 L0,0" style="stroke:#00007f;fill:#00007f;stroke-width:2.5;stroke-linecap:round;stroke-linejoin:bevel;" transform="translate(92.00000000000068 -1890.0) rotate(90.0 0 0)" /></g><text x="5.115907697472721e-13" y="-1945.0" style="white-space:pre;" fill="#005400" font-family="DejaVu Sans" font-size="30.0" text-anchor="middle" dominant-baseline="baseline" xml:space="preserve" transform="rotate(0.0 5.115907697472721e-13 -1940.0)">M 2⌀20,span=184</text></g></svg>
  TextPositionType = 0
  WayPoints = (2) [(0,0,0),(50,0,0)]
  WayPointsType = 0
  X = 149.382
  Y = 95
FEATURE [TechDraw::DrawPage] TechDraw__DrawPage003  label="Column Drawing003"
  KeepUpdated = true
  NextBalloonIndex = 1
  ProjectionType = 0
  Template = -> Template003
  Views = -> [ReinforcementDrawingView003,ReinforcementDimensioning038,ReinforcementDimensioning039,ReinforcementDimensioning040,ReinforcementDimensioning041,ReinforcementDimensioning042,ReinforcementDimensioning043,ReinforcementDimensioning044,ReinforcementDimensioning045,ReinforcementDimensioning046,ReinforcementDimensioning047,ReinforcementDimensioning048,ReinforcementDimensioning049]
FEATURE [TechDraw::DrawSVGTemplate] Template004
  Height = 210
  Orientation = 1
  Width = 297
FEATURE [TechDraw::DrawViewSymbolPython] ReinforcementDrawingView004  label="Top View"  # drawing view (typed FeaturePython)
  DimensionBottomOffset = 34
  DimensionLeftOffset = 16
  DimensionRightOffset = 28
  DimensionTopOffset = 46
  Height = 300
  LeftOffset = 78.5
  LockPosition = false
  MaxHeight = 210
  MaxWidth = 297
  MinBottomOffset = 30
  MinRightOffset = 20
  PositionType = 0
  Rebars = -> [Rebar,Rebar001,Rebar002,Rebar015,Rebar016,Rebar017,Rebar018,Rebar019,Rebar020,Rebar021,Rebar022,Rebar023,Rebar024,Rebar025,Rebar026]
  RebarsColorStyle = 0
  RebarsStrokeWidth = 0.35
  Rotation = 0
  Scale = 0.466667
  ScaleType = 1
  Structure = -> Structure
  StructureColorStyle = 0
  StructureStrokeWidth = 0.5
  Symbol = <blob: 8977 chars omitted>
  Template = -> Template004
  TopOffset = 40
  View = 4
  VisibleRebars = -> [Rebar002,Rebar015,Rebar016,Rebar017,Rebar018,Rebar019,Rebar020,Rebar021,Rebar022,Rebar023,Rebar024,Rebar025,Rebar026,Rebar,Rebar001]
  Width = 300
  X = 148.5
  Y = 100
  expr: LeftOffset = .Template.Width.Value / 2 - .Width.Value * .Scale / 2
FEATURE [TechDraw::DrawViewSymbolPython] ReinforcementDimensioning050  # drawing view (typed FeaturePython)
  DimensionBottomOffset = 10
  DimensionFormat = %M %C⌀%D,span=%S
  DimensionLeftOffset = 10
  DimensionRightOffset = 10
  DimensionTopOffset = 10
  Font = DejaVu Sans
  FontSize = 3
  LineEndSymbol = 0
  LineMidPointSymbol = 1
  LineStartSymbol = 3
  LineStyle = 0
  LockPosition = false
  MultiRebar_LineEndSymbol = 0
  MultiRebar_LineStartSymbol = 0
  MultiRebar_OuterDimension = true
  MultiRebar_TextPositionType = 0
  ParentDrawingView = -> ReinforcementDrawingView004
  Rebar = -> Rebar002
  Rotation = 0
  Scale = 0.466667
  ScaleType = 2
  SingleRebar_LineEndSymbol = 0
  SingleRebar_LineStartSymbol = 3
  SingleRebar_OuterDimension = false
  SingleRebar_TextPositionType = 1
  StrokeWidth = 0.25
  Symbol = <svg version="1.1" xmlns="http://www.w3.org/2000/svg" xmlns:xlink="http://www.w3.org/1999/xlink" xmlns:freecad="http://www.freecadweb.org/wiki/index.php?title=Svg_Namespace" width="300.0mm" height="300.0mm" viewBox="0 0 300.0 300.0"><text x="106.0" y="-0.0" style="white-space:pre;" fill="#005400" font-family="DejaVu Sans" font-size="6.428571428571429" text-anchor="middle" dominant-baseline="baseline" xml:space="preserve" transform="translate(150.0, 150.0)">Strp 12⌀8,span=1300</text></svg>
  TextPositionType = 0
  WayPoints = (2) [(0,0,0),(50,0,0)]
  WayPointsType = 0
  X = 148.5
  Y = 100
FEATURE [TechDraw::DrawViewSymbolPython] ReinforcementDimensioning051  # drawing view (typed FeaturePython)
  DimensionBottomOffset = 10
  DimensionFormat = %M %C⌀%D,span=%S
  DimensionLeftOffset = 10
  DimensionRightOffset = 10
  DimensionTopOffset = 10
  Font = DejaVu Sans
  FontSize = 3
  LineEndSymbol = 0
  LineMidPointSymbol = 1
  LineStartSymbol = 3
  LineStyle = 0
  LockPosition = false
  MultiRebar_LineEndSymbol = 0
  MultiRebar_LineStartSymbol = 0
  MultiRebar_OuterDimension = true
  MultiRebar_TextPositionType = 0
  ParentDrawingView = -> ReinforcementDrawingView004
  Rebar = -> Rebar015
  Rotation = 0
  Scale = 0.466667
  ScaleType = 2
  SingleRebar_LineEndSymbol = 0
  SingleRebar_LineStartSymbol = 3
  SingleRebar_OuterDimension = false
  SingleRebar_TextPositionType = 1
  StrokeWidth = 0.25
  Symbol = <svg version="1.1" xmlns="http://www.w3.org/2000/svg" xmlns:xlink="http://www.w3.org/1999/xlink" xmlns:freecad="http://www.freecadweb.org/wiki/index.php?title=Svg_Namespace" width="300.0mm" height="300.0mm" viewBox="0 0 300.0 300.0"><g transform="translate(150.0, 150.0)"><g><path d="M60.66666666666667 160.7142857142857 L60.66666666666667 171.42857142857142 L29.333333333333357 171.42857142857142 L29.333333333333357 160.7142857142857" style="stroke:#00007f;stroke-width:0.5357142857142857;stroke-linecap:round;fill:none;" stroke-dasharray="" /><path d="M0,0 -8,-1.5 V1.5 L0,0" style="stroke:#00007f;fill:#00007f;stroke-width:0.5357142857142857;stroke-linecap:round;stroke-linejoin:bevel;" transform="translate(60.66666666666667 160.7142857142857) rotate(-90.0 0 0)" /><g id="line_mid_points"><circle cx="0" cy="0" r="1.0714285714285714" fill="#00007f" transform="translate(60.66666666666667 171.42857142857142) rotate(90.0 0 0)" /><circle cx="0" cy="0" r="1.0714285714285714" fill="#00007f" transform="translate(29.333333333333357 171.42857142857142) rotate(180.0 0 0)" /></g><path d="M0,0 -8,-1.5 V1.5 L0,0" style="stroke:#00007f;fill:#00007f;stroke-width:0.5357142857142857;stroke-linecap:round;stroke-linejoin:bevel;" transform="translate(29.333333333333357 160.7142857142857) rotate(-90.0 0 0)" /></g><text x="45.000000000000014" y="170.35714285714283" style="white-space:pre;" fill="#005400" font-family="DejaVu Sans" font-size="6.428571428571429" text-anchor="middle" dominant-baseline="baseline" xml:space="preserve" transform="rotate(-0.0 45.000000000000014 171.42857142857142)">XD 2⌀20,span=31</text></g></svg>
  TextPositionType = 0
  WayPoints = (2) [(0,0,0),(50,0,0)]
  WayPointsType = 0
  X = 148.5
  Y = 100
FEATURE [TechDraw::DrawViewSymbolPython] ReinforcementDimensioning052  # drawing view (typed FeaturePython)
  DimensionBottomOffset = 16
  DimensionFormat = %M %C⌀%D,span=%S
  DimensionLeftOffset = 10
  DimensionRightOffset = 10
  DimensionTopOffset = 10
  Font = DejaVu Sans
  FontSize = 3
  LineEndSymbol = 0
  LineMidPointSymbol = 1
  LineStartSymbol = 3
  LineStyle = 0
  LockPosition = false
  MultiRebar_LineEndSymbol = 0
  MultiRebar_LineStartSymbol = 0
  MultiRebar_OuterDimension = true
  MultiRebar_TextPositionType = 0
  ParentDrawingView = -> ReinforcementDrawingView004
  Rebar = -> Rebar016
  Rotation = 0
  Scale = 0.466667
  ScaleType = 2
  SingleRebar_LineEndSymbol = 0
  SingleRebar_LineStartSymbol = 3
  SingleRebar_OuterDimension = false
  SingleRebar_TextPositionType = 1
  StrokeWidth = 0.25
  Symbol = <svg version="1.1" xmlns="http://www.w3.org/2000/svg" xmlns:xlink="http://www.w3.org/1999/xlink" xmlns:freecad="http://www.freecadweb.org/wiki/index.php?title=Svg_Namespace" width="300.0mm" height="300.0mm" viewBox="0 0 300.0 300.0"><g transform="translate(150.0, 150.0)"><g><path d="M171.42857142857142 129.0 L0.0 129.0" style="stroke:#00007f;stroke-width:0.5357142857142857;stroke-linecap:round;fill:none;" stroke-dasharray="" /><g id="line_mid_points" /><path d="M0,0 -8,-1.5 V1.5 L0,0" style="stroke:#00007f;fill:#00007f;stroke-width:0.5357142857142857;stroke-linecap:round;stroke-linejoin:bevel;" transform="translate(0.0 129.0) rotate(180.0 0 0)" /></g><text x="171.42857142857142" y="132.21428571428572" style="white-space:pre;" fill="#005400" font-family="DejaVu Sans" font-size="6.428571428571429" text-anchor="start" dominant-baseline="baseline" xml:space="preserve">XD 1⌀16,span=0</text></g></svg>
  TextPositionType = 0
  WayPoints = (2) [(0,0,0),(50,0,0)]
  WayPointsType = 0
  X = 148.5
  Y = 100
FEATURE [TechDraw::DrawViewSymbolPython] ReinforcementDimensioning053  # drawing view (typed FeaturePython)
  DimensionBottomOffset = 16
  DimensionFormat = %M %C⌀%D,span=%S
  DimensionLeftOffset = 10
  DimensionRightOffset = 16
  DimensionTopOffset = 10
  Font = DejaVu Sans
  FontSize = 3
  LineEndSymbol = 0
  LineMidPointSymbol = 1
  LineStartSymbol = 3
  LineStyle = 0
  LockPosition = false
  MultiRebar_LineEndSymbol = 0
  MultiRebar_LineStartSymbol = 0
  MultiRebar_OuterDimension = true
  MultiRebar_TextPositionType = 0
  ParentDrawingView = -> ReinforcementDrawingView004
  Rebar = -> Rebar017
  Rotation = 0
  Scale = 0.466667
  ScaleType = 2
  SingleRebar_LineEndSymbol = 0
  SingleRebar_LineStartSymbol = 3
  SingleRebar_OuterDimension = false
  SingleRebar_TextPositionType = 1
  StrokeWidth = 0.25
  Symbol = <svg version="1.1" xmlns="http://www.w3.org/2000/svg" xmlns:xlink="http://www.w3.org/1999/xlink" xmlns:freecad="http://www.freecadweb.org/wiki/index.php?title=Svg_Namespace" width="300.0mm" height="300.0mm" viewBox="0 0 300.0 300.0"><g transform="translate(150.0, 150.0)"><g><path d="M-29.333333333333343 173.57142857142856 L-29.333333333333343 184.28571428571428 L-60.66666666666666 184.28571428571428 L-60.66666666666666 173.57142857142856" style="stroke:#00007f;stroke-width:0.5357142857142857;stroke-linecap:round;fill:none;" stroke-dasharray="" /><path d="M0,0 -8,-1.5 V1.5 L0,0" style="stroke:#00007f;fill:#00007f;stroke-width:0.5357142857142857;stroke-linecap:round;stroke-linejoin:bevel;" transform="translate(-29.333333333333343 173.57142857142856) rotate(-90.0 0 0)" /><g id="line_mid_points"><circle cx="0" cy="0" r="1.0714285714285714" fill="#00007f" transform="translate(-29.333333333333343 184.28571428571428) rotate(90.0 0 0)" /><circle cx="0" cy="0" r="1.0714285714285714" fill="#00007f" transform="translate(-60.66666666666666 184.28571428571428) rotate(180.0 0 0)" /></g><path d="M0,0 -8,-1.5 V1.5 L0,0" style="stroke:#00007f;fill:#00007f;stroke-width:0.5357142857142857;stroke-linecap:round;stroke-linejoin:bevel;" transform="translate(-60.66666666666666 173.57142857142856) rotate(-90.0 0 0)" /></g><text x="-45.0" y="183.2142857142857" style="white-space:pre;" fill="#005400" font-family="DejaVu Sans" font-size="6.428571428571429" text-anchor="middle" dominant-baseline="baseline" xml:space="preserve" transform="rotate(-0.0 -45.0 184.28571428571428)">XD 2⌀20,span=31</text></g></svg>
  TextPositionType = 0
  WayPoints = (2) [(0,0,0),(50,0,0)]
  WayPointsType = 0
  X = 148.5
  Y = 100
FEATURE [TechDraw::DrawViewSymbolPython] ReinforcementDimensioning054  # drawing view (typed FeaturePython)
  DimensionBottomOffset = 22
  DimensionFormat = %M %C⌀%D,span=%S
  DimensionLeftOffset = 10
  DimensionRightOffset = 16
  DimensionTopOffset = 10
  Font = DejaVu Sans
  FontSize = 3
  LineEndSymbol = 0
  LineMidPointSymbol = 1
  LineStartSymbol = 3
  LineStyle = 0
  LockPosition = false
  MultiRebar_LineEndSymbol = 0
  MultiRebar_LineStartSymbol = 0
  MultiRebar_OuterDimension = true
  MultiRebar_TextPositionType = 0
  ParentDrawingView = -> ReinforcementDrawingView004
  Rebar = -> Rebar018
  Rotation = 0
  Scale = 0.466667
  ScaleType = 2
  SingleRebar_LineEndSymbol = 0
  SingleRebar_LineStartSymbol = 3
  SingleRebar_OuterDimension = false
  SingleRebar_TextPositionType = 1
  StrokeWidth = 0.25
  Symbol = <svg version="1.1" xmlns="http://www.w3.org/2000/svg" xmlns:xlink="http://www.w3.org/1999/xlink" xmlns:freecad="http://www.freecadweb.org/wiki/index.php?title=Svg_Namespace" width="300.0mm" height="300.0mm" viewBox="0 0 300.0 300.0"><g transform="translate(150.0, 150.0)"><g><path d="M60.66666666666667 -160.7142857142857 L60.66666666666667 -171.42857142857142 L29.333333333333357 -171.42857142857142 L29.333333333333357 -160.7142857142857" style="stroke:#00007f;stroke-width:0.5357142857142857;stroke-linecap:round;fill:none;" stroke-dasharray="" /><path d="M0,0 -8,-1.5 V1.5 L0,0" style="stroke:#00007f;fill:#00007f;stroke-width:0.5357142857142857;stroke-linecap:round;stroke-linejoin:bevel;" transform="translate(60.66666666666667 -160.7142857142857) rotate(90.0 0 0)" /><g id="line_mid_points"><circle cx="0" cy="0" r="1.0714285714285714" fill="#00007f" transform="translate(60.66666666666667 -171.42857142857142) rotate(-90.0 0 0)" /><circle cx="0" cy="0" r="1.0714285714285714" fill="#00007f" transform="translate(29.333333333333357 -171.42857142857142) rotate(180.0 0 0)" /></g><path d="M0,0 -8,-1.5 V1.5 L0,0" style="stroke:#00007f;fill:#00007f;stroke-width:0.5357142857142857;stroke-linecap:round;stroke-linejoin:bevel;" transform="translate(29.333333333333357 -160.7142857142857) rotate(90.0 0 0)" /></g><text x="45.000000000000014" y="-172.5" style="white-space:pre;" fill="#005400" font-family="DejaVu Sans" font-size="6.428571428571429" text-anchor="middle" dominant-baseline="baseline" xml:space="preserve" transform="rotate(-0.0 45.000000000000014 -171.42857142857142)">XD 2⌀20,span=31</text></g></svg>
  TextPositionType = 0
  WayPoints = (2) [(0,0,0),(50,0,0)]
  WayPointsType = 0
  X = 148.5
  Y = 100
FEATURE [TechDraw::DrawViewSymbolPython] ReinforcementDimensioning055  # drawing view (typed FeaturePython)
  DimensionBottomOffset = 22
  DimensionFormat = %M %C⌀%D,span=%S
  DimensionLeftOffset = 10
  DimensionRightOffset = 16
  DimensionTopOffset = 16
  Font = DejaVu Sans
  FontSize = 3
  LineEndSymbol = 0
  LineMidPointSymbol = 1
  LineStartSymbol = 3
  LineStyle = 0
  LockPosition = false
  MultiRebar_LineEndSymbol = 0
  MultiRebar_LineStartSymbol = 0
  MultiRebar_OuterDimension = true
  MultiRebar_TextPositionType = 0
  ParentDrawingView = -> ReinforcementDrawingView004
  Rebar = -> Rebar019
  Rotation = 0
  Scale = 0.466667
  ScaleType = 2
  SingleRebar_LineEndSymbol = 0
  SingleRebar_LineStartSymbol = 3
  SingleRebar_OuterDimension = false
  SingleRebar_TextPositionType = 1
  StrokeWidth = 0.25
  Symbol = <svg version="1.1" xmlns="http://www.w3.org/2000/svg" xmlns:xlink="http://www.w3.org/1999/xlink" xmlns:freecad="http://www.freecadweb.org/wiki/index.php?title=Svg_Namespace" width="300.0mm" height="300.0mm" viewBox="0 0 300.0 300.0"><g transform="translate(150.0, 150.0)"><g><path d="M184.28571428571428 -125.0 L0.0 -125.0" style="stroke:#00007f;stroke-width:0.5357142857142857;stroke-linecap:round;fill:none;" stroke-dasharray="" /><g id="line_mid_points" /><path d="M0,0 -8,-1.5 V1.5 L0,0" style="stroke:#00007f;fill:#00007f;stroke-width:0.5357142857142857;stroke-linecap:round;stroke-linejoin:bevel;" transform="translate(0.0 -125.0) rotate(180.0 0 0)" /></g><text x="184.28571428571428" y="-121.78571428571429" style="white-space:pre;" fill="#005400" font-family="DejaVu Sans" font-size="6.428571428571429" text-anchor="start" dominant-baseline="baseline" xml:space="preserve">XD 1⌀16,span=0</text></g></svg>
  TextPositionType = 0
  WayPoints = (2) [(0,0,0),(50,0,0)]
  WayPointsType = 0
  X = 148.5
  Y = 100
FEATURE [TechDraw::DrawViewSymbolPython] ReinforcementDimensioning056  # drawing view (typed FeaturePython)
  DimensionBottomOffset = 22
  DimensionFormat = %M %C⌀%D,span=%S
  DimensionLeftOffset = 10
  DimensionRightOffset = 22
  DimensionTopOffset = 16
  Font = DejaVu Sans
  FontSize = 3
  LineEndSymbol = 0
  LineMidPointSymbol = 1
  LineStartSymbol = 3
  LineStyle = 0
  LockPosition = false
  MultiRebar_LineEndSymbol = 0
  MultiRebar_LineStartSymbol = 0
  MultiRebar_OuterDimension = true
  MultiRebar_TextPositionType = 0
  ParentDrawingView = -> ReinforcementDrawingView004
  Rebar = -> Rebar020
  Rotation = 0
  Scale = 0.466667
  ScaleType = 2
  SingleRebar_LineEndSymbol = 0
  SingleRebar_LineStartSymbol = 3
  SingleRebar_OuterDimension = false
  SingleRebar_TextPositionType = 1
  StrokeWidth = 0.25
  Symbol = <svg version="1.1" xmlns="http://www.w3.org/2000/svg" xmlns:xlink="http://www.w3.org/1999/xlink" xmlns:freecad="http://www.freecadweb.org/wiki/index.php?title=Svg_Namespace" width="300.0mm" height="300.0mm" viewBox="0 0 300.0 300.0"><g transform="translate(150.0, 150.0)"><g><path d="M-29.333333333333343 -173.57142857142856 L-29.333333333333343 -184.28571428571428 L-60.66666666666666 -184.28571428571428 L-60.66666666666666 -173.57142857142856" style="stroke:#00007f;stroke-width:0.5357142857142857;stroke-linecap:round;fill:none;" stroke-dasharray="" /><path d="M0,0 -8,-1.5 V1.5 L0,0" style="stroke:#00007f;fill:#00007f;stroke-width:0.5357142857142857;stroke-linecap:round;stroke-linejoin:bevel;" transform="translate(-29.333333333333343 -173.57142857142856) rotate(90.0 0 0)" /><g id="line_mid_points"><circle cx="0" cy="0" r="1.0714285714285714" fill="#00007f" transform="translate(-29.333333333333343 -184.28571428571428) rotate(-90.0 0 0)" /><circle cx="0" cy="0" r="1.0714285714285714" fill="#00007f" transform="translate(-60.66666666666666 -184.28571428571428) rotate(180.0 0 0)" /></g><path d="M0,0 -8,-1.5 V1.5 L0,0" style="stroke:#00007f;fill:#00007f;stroke-width:0.5357142857142857;stroke-linecap:round;stroke-linejoin:bevel;" transform="translate(-60.66666666666666 -173.57142857142856) rotate(90.0 0 0)" /></g><text x="-45.0" y="-185.35714285714286" style="white-space:pre;" fill="#005400" font-family="DejaVu Sans" font-size="6.428571428571429" text-anchor="middle" dominant-baseline="baseline" xml:space="preserve" transform="rotate(-0.0 -45.0 -184.28571428571428)">XD 2⌀20,span=31</text></g></svg>
  TextPositionType = 0
  WayPoints = (2) [(0,0,0),(50,0,0)]
  WayPointsType = 0
  X = 148.5
  Y = 100
FEATURE [TechDraw::DrawViewSymbolPython] ReinforcementDimensioning057  # drawing view (typed FeaturePython)
  DimensionBottomOffset = 22
  DimensionFormat = %M %C⌀%D,span=%S
  DimensionLeftOffset = 10
  DimensionRightOffset = 22
  DimensionTopOffset = 22
  Font = DejaVu Sans
  FontSize = 3
  LineEndSymbol = 0
  LineMidPointSymbol = 1
  LineStartSymbol = 3
  LineStyle = 0
  LockPosition = false
  MultiRebar_LineEndSymbol = 0
  MultiRebar_LineStartSymbol = 0
  MultiRebar_OuterDimension = true
  MultiRebar_TextPositionType = 0
  ParentDrawingView = -> ReinforcementDrawingView004
  Rebar = -> Rebar021
  Rotation = 0
  Scale = 0.466667
  ScaleType = 2
  SingleRebar_LineEndSymbol = 0
  SingleRebar_LineStartSymbol = 3
  SingleRebar_OuterDimension = false
  SingleRebar_TextPositionType = 1
  StrokeWidth = 0.25
  Symbol = <svg version="1.1" xmlns="http://www.w3.org/2000/svg" xmlns:xlink="http://www.w3.org/1999/xlink" xmlns:freecad="http://www.freecadweb.org/wiki/index.php?title=Svg_Namespace" width="300.0mm" height="300.0mm" viewBox="0 0 300.0 300.0"><g transform="translate(150.0, 150.0)"><g><path d="M-133.0 197.14285714285714 L-133.0 45.00000000000003" style="stroke:#00007f;stroke-width:0.5357142857142857;stroke-linecap:round;fill:none;" stroke-dasharray="" /><g id="line_mid_points" /><path d="M0,0 -8,-1.5 V1.5 L0,0" style="stroke:#00007f;fill:#00007f;stroke-width:0.5357142857142857;stroke-linecap:round;stroke-linejoin:bevel;" transform="translate(-133.0 45.00000000000003) rotate(-90.0 0 0)" /></g><text x="-133.0" y="200.35714285714286" style="white-space:pre;" fill="#005400" font-family="DejaVu Sans" font-size="6.428571428571429" text-anchor="middle" dominant-baseline="baseline" xml:space="preserve">YD 1⌀20,span=0</text></g></svg>
  TextPositionType = 0
  WayPoints = (2) [(0,0,0),(50,0,0)]
  WayPointsType = 0
  X = 148.5
  Y = 100
FEATURE [TechDraw::DrawViewSymbolPython] ReinforcementDimensioning058  # drawing view (typed FeaturePython)
  DimensionBottomOffset = 28
  DimensionFormat = %M %C⌀%D,span=%S
  DimensionLeftOffset = 10
  DimensionRightOffset = 22
  DimensionTopOffset = 22
  Font = DejaVu Sans
  FontSize = 3
  LineEndSymbol = 0
  LineMidPointSymbol = 1
  LineStartSymbol = 3
  LineStyle = 0
  LockPosition = false
  MultiRebar_LineEndSymbol = 0
  MultiRebar_LineStartSymbol = 0
  MultiRebar_OuterDimension = true
  MultiRebar_TextPositionType = 0
  ParentDrawingView = -> ReinforcementDrawingView004
  Rebar = -> Rebar022
  Rotation = 0
  Scale = 0.466667
  ScaleType = 2
  SingleRebar_LineEndSymbol = 0
  SingleRebar_LineStartSymbol = 3
  SingleRebar_OuterDimension = false
  SingleRebar_TextPositionType = 1
  StrokeWidth = 0.25
  Symbol = <svg version="1.1" xmlns="http://www.w3.org/2000/svg" xmlns:xlink="http://www.w3.org/1999/xlink" xmlns:freecad="http://www.freecadweb.org/wiki/index.php?title=Svg_Namespace" width="300.0mm" height="300.0mm" viewBox="0 0 300.0 300.0"><g transform="translate(150.0, 150.0)"><g><path d="M-115.0 -197.14285714285714 L-115.0 -2.842170943040401e-14" style="stroke:#00007f;stroke-width:0.5357142857142857;stroke-linecap:round;fill:none;" stroke-dasharray="" /><g id="line_mid_points" /><path d="M0,0 -8,-1.5 V1.5 L0,0" style="stroke:#00007f;fill:#00007f;stroke-width:0.5357142857142857;stroke-linecap:round;stroke-linejoin:bevel;" transform="translate(-115.0 -2.842170943040401e-14) rotate(90.0 0 0)" /></g><text x="-115.0" y="-197.14285714285714" style="white-space:pre;" fill="#005400" font-family="DejaVu Sans" font-size="6.428571428571429" text-anchor="middle" dominant-baseline="baseline" xml:space="preserve">YD 1⌀16,span=0</text></g></svg>
  TextPositionType = 0
  WayPoints = (2) [(0,0,0),(50,0,0)]
  WayPointsType = 0
  X = 148.5
  Y = 100
FEATURE [TechDraw::DrawViewSymbolPython] ReinforcementDimensioning059  # drawing view (typed FeaturePython)
  DimensionBottomOffset = 28
  DimensionFormat = %M %C⌀%D,span=%S
  DimensionLeftOffset = 10
  DimensionRightOffset = 22
  DimensionTopOffset = 28
  Font = DejaVu Sans
  FontSize = 3
  LineEndSymbol = 0
  LineMidPointSymbol = 1
  LineStartSymbol = 3
  LineStyle = 0
  LockPosition = false
  MultiRebar_LineEndSymbol = 0
  MultiRebar_LineStartSymbol = 0
  MultiRebar_OuterDimension = true
  MultiRebar_TextPositionType = 0
  ParentDrawingView = -> ReinforcementDrawingView004
  Rebar = -> Rebar023
  Rotation = 0
  Scale = 0.466667
  ScaleType = 2
  SingleRebar_LineEndSymbol = 0
  SingleRebar_LineStartSymbol = 3
  SingleRebar_OuterDimension = false
  SingleRebar_TextPositionType = 1
  StrokeWidth = 0.25
  Symbol = <svg version="1.1" xmlns="http://www.w3.org/2000/svg" xmlns:xlink="http://www.w3.org/1999/xlink" xmlns:freecad="http://www.freecadweb.org/wiki/index.php?title=Svg_Namespace" width="300.0mm" height="300.0mm" viewBox="0 0 300.0 300.0"><g transform="translate(150.0, 150.0)"><g><path d="M-133.0 -210.0 L-133.0 -44.99999999999997" style="stroke:#00007f;stroke-width:0.5357142857142857;stroke-linecap:round;fill:none;" stroke-dasharray="" /><g id="line_mid_points" /><path d="M0,0 -8,-1.5 V1.5 L0,0" style="stroke:#00007f;fill:#00007f;stroke-width:0.5357142857142857;stroke-linecap:round;stroke-linejoin:bevel;" transform="translate(-133.0 -44.99999999999997) rotate(90.0 0 0)" /></g><text x="-133.0" y="-210.0" style="white-space:pre;" fill="#005400" font-family="DejaVu Sans" font-size="6.428571428571429" text-anchor="middle" dominant-baseline="baseline" xml:space="preserve">YD 1⌀20,span=0</text></g></svg>
  TextPositionType = 0
  WayPoints = (2) [(0,0,0),(50,0,0)]
  WayPointsType = 0
  X = 148.5
  Y = 100
FEATURE [TechDraw::DrawViewSymbolPython] ReinforcementDimensioning060  # drawing view (typed FeaturePython)
  DimensionBottomOffset = 28
  DimensionFormat = %M %C⌀%D,span=%S
  DimensionLeftOffset = 10
  DimensionRightOffset = 22
  DimensionTopOffset = 34
  Font = DejaVu Sans
  FontSize = 3
  LineEndSymbol = 0
  LineMidPointSymbol = 1
  LineStartSymbol = 3
  LineStyle = 0
  LockPosition = false
  MultiRebar_LineEndSymbol = 0
  MultiRebar_LineStartSymbol = 0
  MultiRebar_OuterDimension = true
  MultiRebar_TextPositionType = 0
  ParentDrawingView = -> ReinforcementDrawingView004
  Rebar = -> Rebar024
  Rotation = 0
  Scale = 0.466667
  ScaleType = 2
  SingleRebar_LineEndSymbol = 0
  SingleRebar_LineStartSymbol = 3
  SingleRebar_OuterDimension = false
  SingleRebar_TextPositionType = 1
  StrokeWidth = 0.25
  Symbol = <svg version="1.1" xmlns="http://www.w3.org/2000/svg" xmlns:xlink="http://www.w3.org/1999/xlink" xmlns:freecad="http://www.freecadweb.org/wiki/index.php?title=Svg_Namespace" width="300.0mm" height="300.0mm" viewBox="0 0 300.0 300.0"><g transform="translate(150.0, 150.0)"><g><path d="M118.0 210.0 L118.0 45.00000000000003" style="stroke:#00007f;stroke-width:0.5357142857142857;stroke-linecap:round;fill:none;" stroke-dasharray="" /><g id="line_mid_points" /><path d="M0,0 -8,-1.5 V1.5 L0,0" style="stroke:#00007f;fill:#00007f;stroke-width:0.5357142857142857;stroke-linecap:round;stroke-linejoin:bevel;" transform="translate(118.0 45.00000000000003) rotate(-90.0 0 0)" /></g><text x="118.0" y="213.21428571428572" style="white-space:pre;" fill="#005400" font-family="DejaVu Sans" font-size="6.428571428571429" text-anchor="middle" dominant-baseline="baseline" xml:space="preserve">YD 1⌀20,span=0</text></g></svg>
  TextPositionType = 0
  WayPoints = (2) [(0,0,0),(50,0,0)]
  WayPointsType = 0
  X = 148.5
  Y = 100
FEATURE [TechDraw::DrawViewSymbolPython] ReinforcementDimensioning061  # drawing view (typed FeaturePython)
  DimensionBottomOffset = 34
  DimensionFormat = %M %C⌀%D,span=%S
  DimensionLeftOffset = 10
  DimensionRightOffset = 22
  DimensionTopOffset = 34
  Font = DejaVu Sans
  FontSize = 3
  LineEndSymbol = 0
  LineMidPointSymbol = 1
  LineStartSymbol = 3
  LineStyle = 0
  LockPosition = false
  MultiRebar_LineEndSymbol = 0
  MultiRebar_LineStartSymbol = 0
  MultiRebar_OuterDimension = true
  MultiRebar_TextPositionType = 0
  ParentDrawingView = -> ReinforcementDrawingView004
  Rebar = -> Rebar025
  Rotation = 0
  Scale = 0.466667
  ScaleType = 2
  SingleRebar_LineEndSymbol = 0
  SingleRebar_LineStartSymbol = 3
  SingleRebar_OuterDimension = false
  SingleRebar_TextPositionType = 1
  StrokeWidth = 0.25
  Symbol = <svg version="1.1" xmlns="http://www.w3.org/2000/svg" xmlns:xlink="http://www.w3.org/1999/xlink" xmlns:freecad="http://www.freecadweb.org/wiki/index.php?title=Svg_Namespace" width="300.0mm" height="300.0mm" viewBox="0 0 300.0 300.0"><g transform="translate(150.0, 150.0)"><g><path d="M126.0 -222.85714285714286 L126.0 -2.842170943040401e-14" style="stroke:#00007f;stroke-width:0.5357142857142857;stroke-linecap:round;fill:none;" stroke-dasharray="" /><g id="line_mid_points" /><path d="M0,0 -8,-1.5 V1.5 L0,0" style="stroke:#00007f;fill:#00007f;stroke-width:0.5357142857142857;stroke-linecap:round;stroke-linejoin:bevel;" transform="translate(126.0 -2.842170943040401e-14) rotate(90.0 0 0)" /></g><text x="126.0" y="-222.85714285714286" style="white-space:pre;" fill="#005400" font-family="DejaVu Sans" font-size="6.428571428571429" text-anchor="middle" dominant-baseline="baseline" xml:space="preserve">YD 1⌀16,span=0</text></g></svg>
  TextPositionType = 0
  WayPoints = (2) [(0,0,0),(50,0,0)]
  WayPointsType = 0
  X = 148.5
  Y = 100
FEATURE [TechDraw::DrawViewSymbolPython] ReinforcementDimensioning062  # drawing view (typed FeaturePython)
  DimensionBottomOffset = 34
  DimensionFormat = %M %C⌀%D,span=%S
  DimensionLeftOffset = 10
  DimensionRightOffset = 22
  DimensionTopOffset = 40
  Font = DejaVu Sans
  FontSize = 3
  LineEndSymbol = 0
  LineMidPointSymbol = 1
  LineStartSymbol = 3
  LineStyle = 0
  LockPosition = false
  MultiRebar_LineEndSymbol = 0
  MultiRebar_LineStartSymbol = 0
  MultiRebar_OuterDimension = true
  MultiRebar_TextPositionType = 0
  ParentDrawingView = -> ReinforcementDrawingView004
  Rebar = -> Rebar026
  Rotation = 0
  Scale = 0.466667
  ScaleType = 2
  SingleRebar_LineEndSymbol = 0
  SingleRebar_LineStartSymbol = 3
  SingleRebar_OuterDimension = false
  SingleRebar_TextPositionType = 1
  StrokeWidth = 0.25
  Symbol = <svg version="1.1" xmlns="http://www.w3.org/2000/svg" xmlns:xlink="http://www.w3.org/1999/xlink" xmlns:freecad="http://www.freecadweb.org/wiki/index.php?title=Svg_Namespace" width="300.0mm" height="300.0mm" viewBox="0 0 300.0 300.0"><g transform="translate(150.0, 150.0)"><g><path d="M100.0 -235.71428571428572 L100.0 -44.99999999999997" style="stroke:#00007f;stroke-width:0.5357142857142857;stroke-linecap:round;fill:none;" stroke-dasharray="" /><g id="line_mid_points" /><path d="M0,0 -8,-1.5 V1.5 L0,0" style="stroke:#00007f;fill:#00007f;stroke-width:0.5357142857142857;stroke-linecap:round;stroke-linejoin:bevel;" transform="translate(100.0 -44.99999999999997) rotate(90.0 0 0)" /></g><text x="100.0" y="-235.71428571428572" style="white-space:pre;" fill="#005400" font-family="DejaVu Sans" font-size="6.428571428571429" text-anchor="middle" dominant-baseline="baseline" xml:space="preserve">YD 1⌀20,span=0</text></g></svg>
  TextPositionType = 0
  WayPoints = (2) [(0,0,0),(50,0,0)]
  WayPointsType = 0
  X = 148.5
  Y = 100
FEATURE [TechDraw::DrawViewSymbolPython] ReinforcementDimensioning063  # drawing view (typed FeaturePython)
  DimensionBottomOffset = 34
  DimensionFormat = %M %C⌀%D,span=%S
  DimensionLeftOffset = 10
  DimensionRightOffset = 22
  DimensionTopOffset = 46
  Font = DejaVu Sans
  FontSize = 3
  LineEndSymbol = 0
  LineMidPointSymbol = 1
  LineStartSymbol = 3
  LineStyle = 0
  LockPosition = false
  MultiRebar_LineEndSymbol = 0
  MultiRebar_LineStartSymbol = 0
  MultiRebar_OuterDimension = true
  MultiRebar_TextPositionType = 0
  ParentDrawingView = -> ReinforcementDrawingView004
  Rebar = -> Rebar
  Rotation = 0
  Scale = 0.466667
  ScaleType = 2
  SingleRebar_LineEndSymbol = 0
  SingleRebar_LineStartSymbol = 3
  SingleRebar_OuterDimension = false
  SingleRebar_TextPositionType = 1
  StrokeWidth = 0.25
  Symbol = <svg version="1.1" xmlns="http://www.w3.org/2000/svg" xmlns:xlink="http://www.w3.org/1999/xlink" xmlns:freecad="http://www.freecadweb.org/wiki/index.php?title=Svg_Namespace" width="300.0mm" height="300.0mm" viewBox="0 0 300.0 300.0"><g transform="translate(150.0, 150.0)"><g><path d="M186.42857142857142 91.99999999999966 L197.14285714285714 91.99999999999966 L197.14285714285714 -92.00000000000068 L186.42857142857142 -92.00000000000068" style="stroke:#00007f;stroke-width:0.5357142857142857;stroke-linecap:round;fill:none;" stroke-dasharray="" /><path d="M0,0 -8,-1.5 V1.5 L0,0" style="stroke:#00007f;fill:#00007f;stroke-width:0.5357142857142857;stroke-linecap:round;stroke-linejoin:bevel;" transform="translate(186.42857142857142 91.99999999999966) rotate(180.0 0 0)" /><g id="line_mid_points"><circle cx="0" cy="0" r="1.0714285714285714" fill="#00007f" transform="translate(197.14285714285714 91.99999999999966) rotate(0.0 0 0)" /><circle cx="0" cy="0" r="1.0714285714285714" fill="#00007f" transform="translate(197.14285714285714 -92.00000000000068) rotate(-90.0 0 0)" /></g><path d="M0,0 -8,-1.5 V1.5 L0,0" style="stroke:#00007f;fill:#00007f;stroke-width:0.5357142857142857;stroke-linecap:round;stroke-linejoin:bevel;" transform="translate(186.42857142857142 -92.00000000000068) rotate(180.0 0 0)" /></g><text x="197.14285714285714" y="-1.071428571429083" style="white-space:pre;" fill="#005400" font-family="DejaVu Sans" font-size="6.428571428571429" text-anchor="middle" dominant-baseline="baseline" xml:space="preserve" transform="rotate(-90 197.14285714285714 -5.115907697472721e-13)">M 2⌀20,span=184</text></g></svg>
  TextPositionType = 0
  WayPoints = (2) [(0,0,0),(50,0,0)]
  WayPointsType = 0
  X = 148.5
  Y = 100
FEATURE [TechDraw::DrawViewSymbolPython] ReinforcementDimensioning064  # drawing view (typed FeaturePython)
  DimensionBottomOffset = 34
  DimensionFormat = %M %C⌀%D,span=%S
  DimensionLeftOffset = 10
  DimensionRightOffset = 28
  DimensionTopOffset = 46
  Font = DejaVu Sans
  FontSize = 3
  LineEndSymbol = 0
  LineMidPointSymbol = 1
  LineStartSymbol = 3
  LineStyle = 0
  LockPosition = false
  MultiRebar_LineEndSymbol = 0
  MultiRebar_LineStartSymbol = 0
  MultiRebar_OuterDimension = true
  MultiRebar_TextPositionType = 0
  ParentDrawingView = -> ReinforcementDrawingView004
  Rebar = -> Rebar001
  Rotation = 0
  Scale = 0.466667
  ScaleType = 2
  SingleRebar_LineEndSymbol = 0
  SingleRebar_LineStartSymbol = 3
  SingleRebar_OuterDimension = false
  SingleRebar_TextPositionType = 1
  StrokeWidth = 0.25
  Symbol = <svg version="1.1" xmlns="http://www.w3.org/2000/svg" xmlns:xlink="http://www.w3.org/1999/xlink" xmlns:freecad="http://www.freecadweb.org/wiki/index.php?title=Svg_Namespace" width="300.0mm" height="300.0mm" viewBox="0 0 300.0 300.0"><g transform="translate(150.0, 150.0)"><g><path d="M-160.7142857142857 91.99999999999966 L-171.42857142857142 91.99999999999966 L-171.42857142857142 -92.00000000000068 L-160.7142857142857 -92.00000000000068" style="stroke:#00007f;stroke-width:0.5357142857142857;stroke-linecap:round;fill:none;" stroke-dasharray="" /><path d="M0,0 -8,-1.5 V1.5 L0,0" style="stroke:#00007f;fill:#00007f;stroke-width:0.5357142857142857;stroke-linecap:round;stroke-linejoin:bevel;" transform="translate(-160.7142857142857 91.99999999999966) rotate(0.0 0 0)" /><g id="line_mid_points"><circle cx="0" cy="0" r="1.0714285714285714" fill="#00007f" transform="translate(-171.42857142857142 91.99999999999966) rotate(180.0 0 0)" /><circle cx="0" cy="0" r="1.0714285714285714" fill="#00007f" transform="translate(-171.42857142857142 -92.00000000000068) rotate(-90.0 0 0)" /></g><path d="M0,0 -8,-1.5 V1.5 L0,0" style="stroke:#00007f;fill:#00007f;stroke-width:0.5357142857142857;stroke-linecap:round;stroke-linejoin:bevel;" transform="translate(-160.7142857142857 -92.00000000000068) rotate(0.0 0 0)" /></g><text x="-171.42857142857142" y="-1.071428571429083" style="white-space:pre;" fill="#005400" font-family="DejaVu Sans" font-size="6.428571428571429" text-anchor="middle" dominant-baseline="baseline" xml:space="preserve" transform="rotate(-90 -171.42857142857142 -5.115907697472721e-13)">M 2⌀20,span=184</text></g></svg>
  TextPositionType = 0
  WayPoints = (2) [(0,0,0),(50,0,0)]
  WayPointsType = 0
  X = 148.5
  Y = 100
FEATURE [TechDraw::DrawPage] TechDraw__DrawPage004  label="Column Drawing004"
  KeepUpdated = true
  NextBalloonIndex = 1
  ProjectionType = 0
  Template = -> Template004
  Views = -> [ReinforcementDrawingView004,ReinforcementDimensioning050,ReinforcementDimensioning051,ReinforcementDimensioning052,ReinforcementDimensioning053,ReinforcementDimensioning054,ReinforcementDimensioning055,ReinforcementDimensioning056,ReinforcementDimensioning057,ReinforcementDimensioning058,ReinforcementDimensioning059,ReinforcementDimensioning060,ReinforcementDimensioning061,+3 more]
FEATURE [TechDraw::DrawSVGTemplate] Template005
  Height = 210
  Orientation = 1
  Width = 297
FEATURE [TechDraw::DrawViewSymbolPython] ReinforcementDrawingView005  label="Bottom View"  # drawing view (typed FeaturePython)
  DimensionBottomOffset = 34
  DimensionLeftOffset = 16
  DimensionRightOffset = 28
  DimensionTopOffset = 46
  Height = 300
  LeftOffset = 73.5
  LockPosition = false
  MaxHeight = 210
  MaxWidth = 297
  MinBottomOffset = 30
  MinRightOffset = 20
  PositionType = 0
  Rebars = -> [Rebar,Rebar001,Rebar002,Rebar015,Rebar016,Rebar017,Rebar018,Rebar019,Rebar020,Rebar021,Rebar022,Rebar023,Rebar024,Rebar025,Rebar026]
  RebarsColorStyle = 0
  RebarsStrokeWidth = 0.35
  Rotation = 0
  Scale = 0.466667
  ScaleType = 1
  Structure = -> Structure
  StructureColorStyle = 0
  StructureStrokeWidth = 0.5
  Symbol = <blob: 8973 chars omitted>
  Template = -> Template005
  TopOffset = 40
  View = 5
  VisibleRebars = -> [Rebar002,Rebar015,Rebar016,Rebar017,Rebar018,Rebar019,Rebar020,Rebar021,Rebar022,Rebar023,Rebar024,Rebar025,Rebar026,Rebar,Rebar001]
  Width = 300
  X = 143.5
  Y = 100
  expr: LeftOffset = .Template.Width.Value / 2 - .Width.Value * .Scale / 2
FEATURE [TechDraw::DrawViewSymbolPython] ReinforcementDimensioning065  # drawing view (typed FeaturePython)
  DimensionBottomOffset = 10
  DimensionFormat = %M %C⌀%D,span=%S
  DimensionLeftOffset = 10
  DimensionRightOffset = 10
  DimensionTopOffset = 10
  Font = DejaVu Sans
  FontSize = 3
  LineEndSymbol = 0
  LineMidPointSymbol = 1
  LineStartSymbol = 3
  LineStyle = 0
  LockPosition = false
  MultiRebar_LineEndSymbol = 0
  MultiRebar_LineStartSymbol = 0
  MultiRebar_OuterDimension = true
  MultiRebar_TextPositionType = 0
  ParentDrawingView = -> ReinforcementDrawingView005
  Rebar = -> Rebar002
  Rotation = 0
  Scale = 0.466667
  ScaleType = 2
  SingleRebar_LineEndSymbol = 0
  SingleRebar_LineStartSymbol = 3
  SingleRebar_OuterDimension = false
  SingleRebar_TextPositionType = 1
  StrokeWidth = 0.25
  Symbol = <svg version="1.1" xmlns="http://www.w3.org/2000/svg" xmlns:xlink="http://www.w3.org/1999/xlink" xmlns:freecad="http://www.freecadweb.org/wiki/index.php?title=Svg_Namespace" width="300.0mm" height="300.0mm" viewBox="0 0 300.0 300.0"><text x="106.0" y="-0.0" style="white-space:pre;" fill="#005400" font-family="DejaVu Sans" font-size="6.428571428571429" text-anchor="middle" dominant-baseline="baseline" xml:space="preserve" transform="translate(150.0, 150.0)">Strp 12⌀8,span=1300</text></svg>
  TextPositionType = 0
  WayPoints = (2) [(0,0,0),(50,0,0)]
  WayPointsType = 0
  X = 143.5
  Y = 100
FEATURE [TechDraw::DrawViewSymbolPython] ReinforcementDimensioning066  # drawing view (typed FeaturePython)
  DimensionBottomOffset = 10
  DimensionFormat = %M %C⌀%D,span=%S
  DimensionLeftOffset = 10
  DimensionRightOffset = 10
  DimensionTopOffset = 10
  Font = DejaVu Sans
  FontSize = 3
  LineEndSymbol = 0
  LineMidPointSymbol = 1
  LineStartSymbol = 3
  LineStyle = 0
  LockPosition = false
  MultiRebar_LineEndSymbol = 0
  MultiRebar_LineStartSymbol = 0
  MultiRebar_OuterDimension = true
  MultiRebar_TextPositionType = 0
  ParentDrawingView = -> ReinforcementDrawingView005
  Rebar = -> Rebar015
  Rotation = 0
  Scale = 0.466667
  ScaleType = 2
  SingleRebar_LineEndSymbol = 0
  SingleRebar_LineStartSymbol = 3
  SingleRebar_OuterDimension = false
  SingleRebar_TextPositionType = 1
  StrokeWidth = 0.25
  Symbol = <svg version="1.1" xmlns="http://www.w3.org/2000/svg" xmlns:xlink="http://www.w3.org/1999/xlink" xmlns:freecad="http://www.freecadweb.org/wiki/index.php?title=Svg_Namespace" width="300.0mm" height="300.0mm" viewBox="0 0 300.0 300.0"><g transform="translate(150.0, 150.0)"><g><path d="M60.66666666666667 -160.7142857142857 L60.66666666666667 -171.42857142857142 L29.333333333333357 -171.42857142857142 L29.333333333333357 -160.7142857142857" style="stroke:#00007f;stroke-width:0.5357142857142857;stroke-linecap:round;fill:none;" stroke-dasharray="" /><path d="M0,0 -8,-1.5 V1.5 L0,0" style="stroke:#00007f;fill:#00007f;stroke-width:0.5357142857142857;stroke-linecap:round;stroke-linejoin:bevel;" transform="translate(60.66666666666667 -160.7142857142857) rotate(90.0 0 0)" /><g id="line_mid_points"><circle cx="0" cy="0" r="1.0714285714285714" fill="#00007f" transform="translate(60.66666666666667 -171.42857142857142) rotate(-90.0 0 0)" /><circle cx="0" cy="0" r="1.0714285714285714" fill="#00007f" transform="translate(29.333333333333357 -171.42857142857142) rotate(180.0 0 0)" /></g><path d="M0,0 -8,-1.5 V1.5 L0,0" style="stroke:#00007f;fill:#00007f;stroke-width:0.5357142857142857;stroke-linecap:round;stroke-linejoin:bevel;" transform="translate(29.333333333333357 -160.7142857142857) rotate(90.0 0 0)" /></g><text x="45.000000000000014" y="-172.5" style="white-space:pre;" fill="#005400" font-family="DejaVu Sans" font-size="6.428571428571429" text-anchor="middle" dominant-baseline="baseline" xml:space="preserve" transform="rotate(-0.0 45.000000000000014 -171.42857142857142)">XD 2⌀20,span=31</text></g></svg>
  TextPositionType = 0
  WayPoints = (2) [(0,0,0),(50,0,0)]
  WayPointsType = 0
  X = 143.5
  Y = 100
FEATURE [TechDraw::DrawViewSymbolPython] ReinforcementDimensioning067  # drawing view (typed FeaturePython)
  DimensionBottomOffset = 10
  DimensionFormat = %M %C⌀%D,span=%S
  DimensionLeftOffset = 10
  DimensionRightOffset = 10
  DimensionTopOffset = 16
  Font = DejaVu Sans
  FontSize = 3
  LineEndSymbol = 0
  LineMidPointSymbol = 1
  LineStartSymbol = 3
  LineStyle = 0
  LockPosition = false
  MultiRebar_LineEndSymbol = 0
  MultiRebar_LineStartSymbol = 0
  MultiRebar_OuterDimension = true
  MultiRebar_TextPositionType = 0
  ParentDrawingView = -> ReinforcementDrawingView005
  Rebar = -> Rebar016
  Rotation = 0
  Scale = 0.466667
  ScaleType = 2
  SingleRebar_LineEndSymbol = 0
  SingleRebar_LineStartSymbol = 3
  SingleRebar_OuterDimension = false
  SingleRebar_TextPositionType = 1
  StrokeWidth = 0.25
  Symbol = <svg version="1.1" xmlns="http://www.w3.org/2000/svg" xmlns:xlink="http://www.w3.org/1999/xlink" xmlns:freecad="http://www.freecadweb.org/wiki/index.php?title=Svg_Namespace" width="300.0mm" height="300.0mm" viewBox="0 0 300.0 300.0"><g transform="translate(150.0, 150.0)"><g><path d="M171.42857142857142 -136.0 L0.0 -136.0" style="stroke:#00007f;stroke-width:0.5357142857142857;stroke-linecap:round;fill:none;" stroke-dasharray="" /><g id="line_mid_points" /><path d="M0,0 -8,-1.5 V1.5 L0,0" style="stroke:#00007f;fill:#00007f;stroke-width:0.5357142857142857;stroke-linecap:round;stroke-linejoin:bevel;" transform="translate(0.0 -136.0) rotate(180.0 0 0)" /></g><text x="171.42857142857142" y="-132.78571428571428" style="white-space:pre;" fill="#005400" font-family="DejaVu Sans" font-size="6.428571428571429" text-anchor="start" dominant-baseline="baseline" xml:space="preserve">XD 1⌀16,span=0</text></g></svg>
  TextPositionType = 0
  WayPoints = (2) [(0,0,0),(50,0,0)]
  WayPointsType = 0
  X = 143.5
  Y = 100
FEATURE [TechDraw::DrawViewSymbolPython] ReinforcementDimensioning068  # drawing view (typed FeaturePython)
  DimensionBottomOffset = 10
  DimensionFormat = %M %C⌀%D,span=%S
  DimensionLeftOffset = 10
  DimensionRightOffset = 16
  DimensionTopOffset = 16
  Font = DejaVu Sans
  FontSize = 3
  LineEndSymbol = 0
  LineMidPointSymbol = 1
  LineStartSymbol = 3
  LineStyle = 0
  LockPosition = false
  MultiRebar_LineEndSymbol = 0
  MultiRebar_LineStartSymbol = 0
  MultiRebar_OuterDimension = true
  MultiRebar_TextPositionType = 0
  ParentDrawingView = -> ReinforcementDrawingView005
  Rebar = -> Rebar017
  Rotation = 0
  Scale = 0.466667
  ScaleType = 2
  SingleRebar_LineEndSymbol = 0
  SingleRebar_LineStartSymbol = 3
  SingleRebar_OuterDimension = false
  SingleRebar_TextPositionType = 1
  StrokeWidth = 0.25
  Symbol = <svg version="1.1" xmlns="http://www.w3.org/2000/svg" xmlns:xlink="http://www.w3.org/1999/xlink" xmlns:freecad="http://www.freecadweb.org/wiki/index.php?title=Svg_Namespace" width="300.0mm" height="300.0mm" viewBox="0 0 300.0 300.0"><g transform="translate(150.0, 150.0)"><g><path d="M-29.333333333333343 -173.57142857142856 L-29.333333333333343 -184.28571428571428 L-60.66666666666666 -184.28571428571428 L-60.66666666666666 -173.57142857142856" style="stroke:#00007f;stroke-width:0.5357142857142857;stroke-linecap:round;fill:none;" stroke-dasharray="" /><path d="M0,0 -8,-1.5 V1.5 L0,0" style="stroke:#00007f;fill:#00007f;stroke-width:0.5357142857142857;stroke-linecap:round;stroke-linejoin:bevel;" transform="translate(-29.333333333333343 -173.57142857142856) rotate(90.0 0 0)" /><g id="line_mid_points"><circle cx="0" cy="0" r="1.0714285714285714" fill="#00007f" transform="translate(-29.333333333333343 -184.28571428571428) rotate(-90.0 0 0)" /><circle cx="0" cy="0" r="1.0714285714285714" fill="#00007f" transform="translate(-60.66666666666666 -184.28571428571428) rotate(180.0 0 0)" /></g><path d="M0,0 -8,-1.5 V1.5 L0,0" style="stroke:#00007f;fill:#00007f;stroke-width:0.5357142857142857;stroke-linecap:round;stroke-linejoin:bevel;" transform="translate(-60.66666666666666 -173.57142857142856) rotate(90.0 0 0)" /></g><text x="-45.0" y="-185.35714285714286" style="white-space:pre;" fill="#005400" font-family="DejaVu Sans" font-size="6.428571428571429" text-anchor="middle" dominant-baseline="baseline" xml:space="preserve" transform="rotate(-0.0 -45.0 -184.28571428571428)">XD 2⌀20,span=31</text></g></svg>
  TextPositionType = 0
  WayPoints = (2) [(0,0,0),(50,0,0)]
  WayPointsType = 0
  X = 143.5
  Y = 100
FEATURE [TechDraw::DrawViewSymbolPython] ReinforcementDimensioning069  # drawing view (typed FeaturePython)
  DimensionBottomOffset = 10
  DimensionFormat = %M %C⌀%D,span=%S
  DimensionLeftOffset = 10
  DimensionRightOffset = 16
  DimensionTopOffset = 22
  Font = DejaVu Sans
  FontSize = 3
  LineEndSymbol = 0
  LineMidPointSymbol = 1
  LineStartSymbol = 3
  LineStyle = 0
  LockPosition = false
  MultiRebar_LineEndSymbol = 0
  MultiRebar_LineStartSymbol = 0
  MultiRebar_OuterDimension = true
  MultiRebar_TextPositionType = 0
  ParentDrawingView = -> ReinforcementDrawingView005
  Rebar = -> Rebar018
  Rotation = 0
  Scale = 0.466667
  ScaleType = 2
  SingleRebar_LineEndSymbol = 0
  SingleRebar_LineStartSymbol = 3
  SingleRebar_OuterDimension = false
  SingleRebar_TextPositionType = 1
  StrokeWidth = 0.25
  Symbol = <svg version="1.1" xmlns="http://www.w3.org/2000/svg" xmlns:xlink="http://www.w3.org/1999/xlink" xmlns:freecad="http://www.freecadweb.org/wiki/index.php?title=Svg_Namespace" width="300.0mm" height="300.0mm" viewBox="0 0 300.0 300.0"><g transform="translate(150.0, 150.0)"><g><path d="M60.66666666666667 160.7142857142857 L60.66666666666667 171.42857142857142 L29.333333333333357 171.42857142857142 L29.333333333333357 160.7142857142857" style="stroke:#00007f;stroke-width:0.5357142857142857;stroke-linecap:round;fill:none;" stroke-dasharray="" /><path d="M0,0 -8,-1.5 V1.5 L0,0" style="stroke:#00007f;fill:#00007f;stroke-width:0.5357142857142857;stroke-linecap:round;stroke-linejoin:bevel;" transform="translate(60.66666666666667 160.7142857142857) rotate(-90.0 0 0)" /><g id="line_mid_points"><circle cx="0" cy="0" r="1.0714285714285714" fill="#00007f" transform="translate(60.66666666666667 171.42857142857142) rotate(90.0 0 0)" /><circle cx="0" cy="0" r="1.0714285714285714" fill="#00007f" transform="translate(29.333333333333357 171.42857142857142) rotate(180.0 0 0)" /></g><path d="M0,0 -8,-1.5 V1.5 L0,0" style="stroke:#00007f;fill:#00007f;stroke-width:0.5357142857142857;stroke-linecap:round;stroke-linejoin:bevel;" transform="translate(29.333333333333357 160.7142857142857) rotate(-90.0 0 0)" /></g><text x="45.000000000000014" y="170.35714285714283" style="white-space:pre;" fill="#005400" font-family="DejaVu Sans" font-size="6.428571428571429" text-anchor="middle" dominant-baseline="baseline" xml:space="preserve" transform="rotate(-0.0 45.000000000000014 171.42857142857142)">XD 2⌀20,span=31</text></g></svg>
  TextPositionType = 0
  WayPoints = (2) [(0,0,0),(50,0,0)]
  WayPointsType = 0
  X = 143.5
  Y = 100
FEATURE [TechDraw::DrawViewSymbolPython] ReinforcementDimensioning070  # drawing view (typed FeaturePython)
  DimensionBottomOffset = 16
  DimensionFormat = %M %C⌀%D,span=%S
  DimensionLeftOffset = 10
  DimensionRightOffset = 16
  DimensionTopOffset = 22
  Font = DejaVu Sans
  FontSize = 3
  LineEndSymbol = 0
  LineMidPointSymbol = 1
  LineStartSymbol = 3
  LineStyle = 0
  LockPosition = false
  MultiRebar_LineEndSymbol = 0
  MultiRebar_LineStartSymbol = 0
  MultiRebar_OuterDimension = true
  MultiRebar_TextPositionType = 0
  ParentDrawingView = -> ReinforcementDrawingView005
  Rebar = -> Rebar019
  Rotation = 0
  Scale = 0.466667
  ScaleType = 2
  SingleRebar_LineEndSymbol = 0
  SingleRebar_LineStartSymbol = 3
  SingleRebar_OuterDimension = false
  SingleRebar_TextPositionType = 1
  StrokeWidth = 0.25
  Symbol = <svg version="1.1" xmlns="http://www.w3.org/2000/svg" xmlns:xlink="http://www.w3.org/1999/xlink" xmlns:freecad="http://www.freecadweb.org/wiki/index.php?title=Svg_Namespace" width="300.0mm" height="300.0mm" viewBox="0 0 300.0 300.0"><g transform="translate(150.0, 150.0)"><g><path d="M184.28571428571428 99.0 L0.0 99.0" style="stroke:#00007f;stroke-width:0.5357142857142857;stroke-linecap:round;fill:none;" stroke-dasharray="" /><g id="line_mid_points" /><path d="M0,0 -8,-1.5 V1.5 L0,0" style="stroke:#00007f;fill:#00007f;stroke-width:0.5357142857142857;stroke-linecap:round;stroke-linejoin:bevel;" transform="translate(0.0 99.0) rotate(180.0 0 0)" /></g><text x="184.28571428571428" y="102.21428571428571" style="white-space:pre;" fill="#005400" font-family="DejaVu Sans" font-size="6.428571428571429" text-anchor="start" dominant-baseline="baseline" xml:space="preserve">XD 1⌀16,span=0</text></g></svg>
  TextPositionType = 0
  WayPoints = (2) [(0,0,0),(50,0,0)]
  WayPointsType = 0
  X = 143.5
  Y = 100
FEATURE [TechDraw::DrawViewSymbolPython] ReinforcementDimensioning071  # drawing view (typed FeaturePython)
  DimensionBottomOffset = 16
  DimensionFormat = %M %C⌀%D,span=%S
  DimensionLeftOffset = 10
  DimensionRightOffset = 22
  DimensionTopOffset = 22
  Font = DejaVu Sans
  FontSize = 3
  LineEndSymbol = 0
  LineMidPointSymbol = 1
  LineStartSymbol = 3
  LineStyle = 0
  LockPosition = false
  MultiRebar_LineEndSymbol = 0
  MultiRebar_LineStartSymbol = 0
  MultiRebar_OuterDimension = true
  MultiRebar_TextPositionType = 0
  ParentDrawingView = -> ReinforcementDrawingView005
  Rebar = -> Rebar020
  Rotation = 0
  Scale = 0.466667
  ScaleType = 2
  SingleRebar_LineEndSymbol = 0
  SingleRebar_LineStartSymbol = 3
  SingleRebar_OuterDimension = false
  SingleRebar_TextPositionType = 1
  StrokeWidth = 0.25
  Symbol = <svg version="1.1" xmlns="http://www.w3.org/2000/svg" xmlns:xlink="http://www.w3.org/1999/xlink" xmlns:freecad="http://www.freecadweb.org/wiki/index.php?title=Svg_Namespace" width="300.0mm" height="300.0mm" viewBox="0 0 300.0 300.0"><g transform="translate(150.0, 150.0)"><g><path d="M-29.333333333333343 173.57142857142856 L-29.333333333333343 184.28571428571428 L-60.66666666666666 184.28571428571428 L-60.66666666666666 173.57142857142856" style="stroke:#00007f;stroke-width:0.5357142857142857;stroke-linecap:round;fill:none;" stroke-dasharray="" /><path d="M0,0 -8,-1.5 V1.5 L0,0" style="stroke:#00007f;fill:#00007f;stroke-width:0.5357142857142857;stroke-linecap:round;stroke-linejoin:bevel;" transform="translate(-29.333333333333343 173.57142857142856) rotate(-90.0 0 0)" /><g id="line_mid_points"><circle cx="0" cy="0" r="1.0714285714285714" fill="#00007f" transform="translate(-29.333333333333343 184.28571428571428) rotate(90.0 0 0)" /><circle cx="0" cy="0" r="1.0714285714285714" fill="#00007f" transform="translate(-60.66666666666666 184.28571428571428) rotate(180.0 0 0)" /></g><path d="M0,0 -8,-1.5 V1.5 L0,0" style="stroke:#00007f;fill:#00007f;stroke-width:0.5357142857142857;stroke-linecap:round;stroke-linejoin:bevel;" transform="translate(-60.66666666666666 173.57142857142856) rotate(-90.0 0 0)" /></g><text x="-45.0" y="183.2142857142857" style="white-space:pre;" fill="#005400" font-family="DejaVu Sans" font-size="6.428571428571429" text-anchor="middle" dominant-baseline="baseline" xml:space="preserve" transform="rotate(-0.0 -45.0 184.28571428571428)">XD 2⌀20,span=31</text></g></svg>
  TextPositionType = 0
  WayPoints = (2) [(0,0,0),(50,0,0)]
  WayPointsType = 0
  X = 143.5
  Y = 100
FEATURE [TechDraw::DrawViewSymbolPython] ReinforcementDimensioning072  # drawing view (typed FeaturePython)
  DimensionBottomOffset = 22
  DimensionFormat = %M %C⌀%D,span=%S
  DimensionLeftOffset = 10
  DimensionRightOffset = 22
  DimensionTopOffset = 22
  Font = DejaVu Sans
  FontSize = 3
  LineEndSymbol = 0
  LineMidPointSymbol = 1
  LineStartSymbol = 3
  LineStyle = 0
  LockPosition = false
  MultiRebar_LineEndSymbol = 0
  MultiRebar_LineStartSymbol = 0
  MultiRebar_OuterDimension = true
  MultiRebar_TextPositionType = 0
  ParentDrawingView = -> ReinforcementDrawingView005
  Rebar = -> Rebar021
  Rotation = 0
  Scale = 0.466667
  ScaleType = 2
  SingleRebar_LineEndSymbol = 0
  SingleRebar_LineStartSymbol = 3
  SingleRebar_OuterDimension = false
  SingleRebar_TextPositionType = 1
  StrokeWidth = 0.25
  Symbol = <svg version="1.1" xmlns="http://www.w3.org/2000/svg" xmlns:xlink="http://www.w3.org/1999/xlink" xmlns:freecad="http://www.freecadweb.org/wiki/index.php?title=Svg_Namespace" width="300.0mm" height="300.0mm" viewBox="0 0 300.0 300.0"><g transform="translate(150.0, 150.0)"><g><path d="M-112.0 -197.14285714285714 L-112.0 -45.00000000000003" style="stroke:#00007f;stroke-width:0.5357142857142857;stroke-linecap:round;fill:none;" stroke-dasharray="" /><g id="line_mid_points" /><path d="M0,0 -8,-1.5 V1.5 L0,0" style="stroke:#00007f;fill:#00007f;stroke-width:0.5357142857142857;stroke-linecap:round;stroke-linejoin:bevel;" transform="translate(-112.0 -45.00000000000003) rotate(90.0 0 0)" /></g><text x="-112.0" y="-197.14285714285714" style="white-space:pre;" fill="#005400" font-family="DejaVu Sans" font-size="6.428571428571429" text-anchor="middle" dominant-baseline="baseline" xml:space="preserve">YD 1⌀20,span=0</text></g></svg>
  TextPositionType = 0
  WayPoints = (2) [(0,0,0),(50,0,0)]
  WayPointsType = 0
  X = 143.5
  Y = 100
FEATURE [TechDraw::DrawViewSymbolPython] ReinforcementDimensioning073  # drawing view (typed FeaturePython)
  DimensionBottomOffset = 22
  DimensionFormat = %M %C⌀%D,span=%S
  DimensionLeftOffset = 10
  DimensionRightOffset = 22
  DimensionTopOffset = 28
  Font = DejaVu Sans
  FontSize = 3
  LineEndSymbol = 0
  LineMidPointSymbol = 1
  LineStartSymbol = 3
  LineStyle = 0
  LockPosition = false
  MultiRebar_LineEndSymbol = 0
  MultiRebar_LineStartSymbol = 0
  MultiRebar_OuterDimension = true
  MultiRebar_TextPositionType = 0
  ParentDrawingView = -> ReinforcementDrawingView005
  Rebar = -> Rebar022
  Rotation = 0
  Scale = 0.466667
  ScaleType = 2
  SingleRebar_LineEndSymbol = 0
  SingleRebar_LineStartSymbol = 3
  SingleRebar_OuterDimension = false
  SingleRebar_TextPositionType = 1
  StrokeWidth = 0.25
  Symbol = <svg version="1.1" xmlns="http://www.w3.org/2000/svg" xmlns:xlink="http://www.w3.org/1999/xlink" xmlns:freecad="http://www.freecadweb.org/wiki/index.php?title=Svg_Namespace" width="300.0mm" height="300.0mm" viewBox="0 0 300.0 300.0"><g transform="translate(150.0, 150.0)"><g><path d="M-96.0 -210.0 L-96.0 -2.842170943040401e-14" style="stroke:#00007f;stroke-width:0.5357142857142857;stroke-linecap:round;fill:none;" stroke-dasharray="" /><g id="line_mid_points" /><path d="M0,0 -8,-1.5 V1.5 L0,0" style="stroke:#00007f;fill:#00007f;stroke-width:0.5357142857142857;stroke-linecap:round;stroke-linejoin:bevel;" transform="translate(-96.0 -2.842170943040401e-14) rotate(90.0 0 0)" /></g><text x="-96.0" y="-210.0" style="white-space:pre;" fill="#005400" font-family="DejaVu Sans" font-size="6.428571428571429" text-anchor="middle" dominant-baseline="baseline" xml:space="preserve">YD 1⌀16,span=0</text></g></svg>
  TextPositionType = 0
  WayPoints = (2) [(0,0,0),(50,0,0)]
  WayPointsType = 0
  X = 143.5
  Y = 100
FEATURE [TechDraw::DrawViewSymbolPython] ReinforcementDimensioning074  # drawing view (typed FeaturePython)
  DimensionBottomOffset = 22
  DimensionFormat = %M %C⌀%D,span=%S
  DimensionLeftOffset = 10
  DimensionRightOffset = 22
  DimensionTopOffset = 34
  Font = DejaVu Sans
  FontSize = 3
  LineEndSymbol = 0
  LineMidPointSymbol = 1
  LineStartSymbol = 3
  LineStyle = 0
  LockPosition = false
  MultiRebar_LineEndSymbol = 0
  MultiRebar_LineStartSymbol = 0
  MultiRebar_OuterDimension = true
  MultiRebar_TextPositionType = 0
  ParentDrawingView = -> ReinforcementDrawingView005
  Rebar = -> Rebar023
  Rotation = 0
  Scale = 0.466667
  ScaleType = 2
  SingleRebar_LineEndSymbol = 0
  SingleRebar_LineStartSymbol = 3
  SingleRebar_OuterDimension = false
  SingleRebar_TextPositionType = 1
  StrokeWidth = 0.25
  Symbol = <svg version="1.1" xmlns="http://www.w3.org/2000/svg" xmlns:xlink="http://www.w3.org/1999/xlink" xmlns:freecad="http://www.freecadweb.org/wiki/index.php?title=Svg_Namespace" width="300.0mm" height="300.0mm" viewBox="0 0 300.0 300.0"><g transform="translate(150.0, 150.0)"><g><path d="M-136.0 197.14285714285714 L-136.0 44.99999999999997" style="stroke:#00007f;stroke-width:0.5357142857142857;stroke-linecap:round;fill:none;" stroke-dasharray="" /><g id="line_mid_points" /><path d="M0,0 -8,-1.5 V1.5 L0,0" style="stroke:#00007f;fill:#00007f;stroke-width:0.5357142857142857;stroke-linecap:round;stroke-linejoin:bevel;" transform="translate(-136.0 44.99999999999997) rotate(-90.0 0 0)" /></g><text x="-136.0" y="200.35714285714286" style="white-space:pre;" fill="#005400" font-family="DejaVu Sans" font-size="6.428571428571429" text-anchor="middle" dominant-baseline="baseline" xml:space="preserve">YD 1⌀20,span=0</text></g></svg>
  TextPositionType = 0
  WayPoints = (2) [(0,0,0),(50,0,0)]
  WayPointsType = 0
  X = 143.5
  Y = 100
FEATURE [TechDraw::DrawViewSymbolPython] ReinforcementDimensioning075  # drawing view (typed FeaturePython)
  DimensionBottomOffset = 28
  DimensionFormat = %M %C⌀%D,span=%S
  DimensionLeftOffset = 10
  DimensionRightOffset = 22
  DimensionTopOffset = 34
  Font = DejaVu Sans
  FontSize = 3
  LineEndSymbol = 0
  LineMidPointSymbol = 1
  LineStartSymbol = 3
  LineStyle = 0
  LockPosition = false
  MultiRebar_LineEndSymbol = 0
  MultiRebar_LineStartSymbol = 0
  MultiRebar_OuterDimension = true
  MultiRebar_TextPositionType = 0
  ParentDrawingView = -> ReinforcementDrawingView005
  Rebar = -> Rebar024
  Rotation = 0
  Scale = 0.466667
  ScaleType = 2
  SingleRebar_LineEndSymbol = 0
  SingleRebar_LineStartSymbol = 3
  SingleRebar_OuterDimension = false
  SingleRebar_TextPositionType = 1
  StrokeWidth = 0.25
  Symbol = <svg version="1.1" xmlns="http://www.w3.org/2000/svg" xmlns:xlink="http://www.w3.org/1999/xlink" xmlns:freecad="http://www.freecadweb.org/wiki/index.php?title=Svg_Namespace" width="300.0mm" height="300.0mm" viewBox="0 0 300.0 300.0"><g transform="translate(150.0, 150.0)"><g><path d="M128.0 -222.85714285714286 L128.0 -45.00000000000003" style="stroke:#00007f;stroke-width:0.5357142857142857;stroke-linecap:round;fill:none;" stroke-dasharray="" /><g id="line_mid_points" /><path d="M0,0 -8,-1.5 V1.5 L0,0" style="stroke:#00007f;fill:#00007f;stroke-width:0.5357142857142857;stroke-linecap:round;stroke-linejoin:bevel;" transform="translate(128.0 -45.00000000000003) rotate(90.0 0 0)" /></g><text x="128.0" y="-222.85714285714286" style="white-space:pre;" fill="#005400" font-family="DejaVu Sans" font-size="6.428571428571429" text-anchor="middle" dominant-baseline="baseline" xml:space="preserve">YD 1⌀20,span=0</text></g></svg>
  TextPositionType = 0
  WayPoints = (2) [(0,0,0),(50,0,0)]
  WayPointsType = 0
  X = 143.5
  Y = 100
FEATURE [TechDraw::DrawViewSymbolPython] ReinforcementDimensioning076  # drawing view (typed FeaturePython)
  DimensionBottomOffset = 28
  DimensionFormat = %M %C⌀%D,span=%S
  DimensionLeftOffset = 10
  DimensionRightOffset = 22
  DimensionTopOffset = 40
  Font = DejaVu Sans
  FontSize = 3
  LineEndSymbol = 0
  LineMidPointSymbol = 1
  LineStartSymbol = 3
  LineStyle = 0
  LockPosition = false
  MultiRebar_LineEndSymbol = 0
  MultiRebar_LineStartSymbol = 0
  MultiRebar_OuterDimension = true
  MultiRebar_TextPositionType = 0
  ParentDrawingView = -> ReinforcementDrawingView005
  Rebar = -> Rebar025
  Rotation = 0
  Scale = 0.466667
  ScaleType = 2
  SingleRebar_LineEndSymbol = 0
  SingleRebar_LineStartSymbol = 3
  SingleRebar_OuterDimension = false
  SingleRebar_TextPositionType = 1
  StrokeWidth = 0.25
  Symbol = <svg version="1.1" xmlns="http://www.w3.org/2000/svg" xmlns:xlink="http://www.w3.org/1999/xlink" xmlns:freecad="http://www.freecadweb.org/wiki/index.php?title=Svg_Namespace" width="300.0mm" height="300.0mm" viewBox="0 0 300.0 300.0"><g transform="translate(150.0, 150.0)"><g><path d="M119.0 -235.71428571428572 L119.0 -2.842170943040401e-14" style="stroke:#00007f;stroke-width:0.5357142857142857;stroke-linecap:round;fill:none;" stroke-dasharray="" /><g id="line_mid_points" /><path d="M0,0 -8,-1.5 V1.5 L0,0" style="stroke:#00007f;fill:#00007f;stroke-width:0.5357142857142857;stroke-linecap:round;stroke-linejoin:bevel;" transform="translate(119.0 -2.842170943040401e-14) rotate(90.0 0 0)" /></g><text x="119.0" y="-235.71428571428572" style="white-space:pre;" fill="#005400" font-family="DejaVu Sans" font-size="6.428571428571429" text-anchor="middle" dominant-baseline="baseline" xml:space="preserve">YD 1⌀16,span=0</text></g></svg>
  TextPositionType = 0
  WayPoints = (2) [(0,0,0),(50,0,0)]
  WayPointsType = 0
  X = 143.5
  Y = 100
FEATURE [TechDraw::DrawViewSymbolPython] ReinforcementDimensioning077  # drawing view (typed FeaturePython)
  DimensionBottomOffset = 28
  DimensionFormat = %M %C⌀%D,span=%S
  DimensionLeftOffset = 10
  DimensionRightOffset = 22
  DimensionTopOffset = 46
  Font = DejaVu Sans
  FontSize = 3
  LineEndSymbol = 0
  LineMidPointSymbol = 1
  LineStartSymbol = 3
  LineStyle = 0
  LockPosition = false
  MultiRebar_LineEndSymbol = 0
  MultiRebar_LineStartSymbol = 0
  MultiRebar_OuterDimension = true
  MultiRebar_TextPositionType = 0
  ParentDrawingView = -> ReinforcementDrawingView005
  Rebar = -> Rebar026
  Rotation = 0
  Scale = 0.466667
  ScaleType = 2
  SingleRebar_LineEndSymbol = 0
  SingleRebar_LineStartSymbol = 3
  SingleRebar_OuterDimension = false
  SingleRebar_TextPositionType = 1
  StrokeWidth = 0.25
  Symbol = <svg version="1.1" xmlns="http://www.w3.org/2000/svg" xmlns:xlink="http://www.w3.org/1999/xlink" xmlns:freecad="http://www.freecadweb.org/wiki/index.php?title=Svg_Namespace" width="300.0mm" height="300.0mm" viewBox="0 0 300.0 300.0"><g transform="translate(150.0, 150.0)"><g><path d="M92.0 210.0 L92.0 44.99999999999997" style="stroke:#00007f;stroke-width:0.5357142857142857;stroke-linecap:round;fill:none;" stroke-dasharray="" /><g id="line_mid_points" /><path d="M0,0 -8,-1.5 V1.5 L0,0" style="stroke:#00007f;fill:#00007f;stroke-width:0.5357142857142857;stroke-linecap:round;stroke-linejoin:bevel;" transform="translate(92.0 44.99999999999997) rotate(-90.0 0 0)" /></g><text x="92.0" y="213.21428571428572" style="white-space:pre;" fill="#005400" font-family="DejaVu Sans" font-size="6.428571428571429" text-anchor="middle" dominant-baseline="baseline" xml:space="preserve">YD 1⌀20,span=0</text></g></svg>
  TextPositionType = 0
  WayPoints = (2) [(0,0,0),(50,0,0)]
  WayPointsType = 0
  X = 143.5
  Y = 100
FEATURE [TechDraw::DrawViewSymbolPython] ReinforcementDimensioning078  # drawing view (typed FeaturePython)
  DimensionBottomOffset = 34
  DimensionFormat = %M %C⌀%D,span=%S
  DimensionLeftOffset = 10
  DimensionRightOffset = 22
  DimensionTopOffset = 46
  Font = DejaVu Sans
  FontSize = 3
  LineEndSymbol = 0
  LineMidPointSymbol = 1
  LineStartSymbol = 3
  LineStyle = 0
  LockPosition = false
  MultiRebar_LineEndSymbol = 0
  MultiRebar_LineStartSymbol = 0
  MultiRebar_OuterDimension = true
  MultiRebar_TextPositionType = 0
  ParentDrawingView = -> ReinforcementDrawingView005
  Rebar = -> Rebar
  Rotation = 0
  Scale = 0.466667
  ScaleType = 2
  SingleRebar_LineEndSymbol = 0
  SingleRebar_LineStartSymbol = 3
  SingleRebar_OuterDimension = false
  SingleRebar_TextPositionType = 1
  StrokeWidth = 0.25
  Symbol = <svg version="1.1" xmlns="http://www.w3.org/2000/svg" xmlns:xlink="http://www.w3.org/1999/xlink" xmlns:freecad="http://www.freecadweb.org/wiki/index.php?title=Svg_Namespace" width="300.0mm" height="300.0mm" viewBox="0 0 300.0 300.0"><g transform="translate(150.0, 150.0)"><g><path d="M186.42857142857142 -91.99999999999966 L197.14285714285714 -91.99999999999966 L197.14285714285714 92.00000000000068 L186.42857142857142 92.00000000000068" style="stroke:#00007f;stroke-width:0.5357142857142857;stroke-linecap:round;fill:none;" stroke-dasharray="" /><path d="M0,0 -8,-1.5 V1.5 L0,0" style="stroke:#00007f;fill:#00007f;stroke-width:0.5357142857142857;stroke-linecap:round;stroke-linejoin:bevel;" transform="translate(186.42857142857142 -91.99999999999966) rotate(180.0 0 0)" /><g id="line_mid_points"><circle cx="0" cy="0" r="1.0714285714285714" fill="#00007f" transform="translate(197.14285714285714 -91.99999999999966) rotate(0.0 0 0)" /><circle cx="0" cy="0" r="1.0714285714285714" fill="#00007f" transform="translate(197.14285714285714 92.00000000000068) rotate(90.0 0 0)" /></g><path d="M0,0 -8,-1.5 V1.5 L0,0" style="stroke:#00007f;fill:#00007f;stroke-width:0.5357142857142857;stroke-linecap:round;stroke-linejoin:bevel;" transform="translate(186.42857142857142 92.00000000000068) rotate(180.0 0 0)" /></g><text x="197.14285714285714" y="-1.0714285714280598" style="white-space:pre;" fill="#005400" font-family="DejaVu Sans" font-size="6.428571428571429" text-anchor="middle" dominant-baseline="baseline" xml:space="preserve" transform="rotate(-90 197.14285714285714 5.115907697472721e-13)">M 2⌀20,span=184</text></g></svg>
  TextPositionType = 0
  WayPoints = (2) [(0,0,0),(50,0,0)]
  WayPointsType = 0
  X = 143.5
  Y = 100
FEATURE [TechDraw::DrawViewSymbolPython] ReinforcementDimensioning079  # drawing view (typed FeaturePython)
  DimensionBottomOffset = 34
  DimensionFormat = %M %C⌀%D,span=%S
  DimensionLeftOffset = 10
  DimensionRightOffset = 28
  DimensionTopOffset = 46
  Font = DejaVu Sans
  FontSize = 3
  LineEndSymbol = 0
  LineMidPointSymbol = 1
  LineStartSymbol = 3
  LineStyle = 0
  LockPosition = false
  MultiRebar_LineEndSymbol = 0
  MultiRebar_LineStartSymbol = 0
  MultiRebar_OuterDimension = true
  MultiRebar_TextPositionType = 0
  ParentDrawingView = -> ReinforcementDrawingView005
  Rebar = -> Rebar001
  Rotation = 0
  Scale = 0.466667
  ScaleType = 2
  SingleRebar_LineEndSymbol = 0
  SingleRebar_LineStartSymbol = 3
  SingleRebar_OuterDimension = false
  SingleRebar_TextPositionType = 1
  StrokeWidth = 0.25
  Symbol = <svg version="1.1" xmlns="http://www.w3.org/2000/svg" xmlns:xlink="http://www.w3.org/1999/xlink" xmlns:freecad="http://www.freecadweb.org/wiki/index.php?title=Svg_Namespace" width="300.0mm" height="300.0mm" viewBox="0 0 300.0 300.0"><g transform="translate(150.0, 150.0)"><g><path d="M-160.7142857142857 -91.99999999999966 L-171.42857142857142 -91.99999999999966 L-171.42857142857142 92.00000000000068 L-160.7142857142857 92.00000000000068" style="stroke:#00007f;stroke-width:0.5357142857142857;stroke-linecap:round;fill:none;" stroke-dasharray="" /><path d="M0,0 -8,-1.5 V1.5 L0,0" style="stroke:#00007f;fill:#00007f;stroke-width:0.5357142857142857;stroke-linecap:round;stroke-linejoin:bevel;" transform="translate(-160.7142857142857 -91.99999999999966) rotate(0.0 0 0)" /><g id="line_mid_points"><circle cx="0" cy="0" r="1.0714285714285714" fill="#00007f" transform="translate(-171.42857142857142 -91.99999999999966) rotate(180.0 0 0)" /><circle cx="0" cy="0" r="1.0714285714285714" fill="#00007f" transform="translate(-171.42857142857142 92.00000000000068) rotate(90.0 0 0)" /></g><path d="M0,0 -8,-1.5 V1.5 L0,0" style="stroke:#00007f;fill:#00007f;stroke-width:0.5357142857142857;stroke-linecap:round;stroke-linejoin:bevel;" transform="translate(-160.7142857142857 92.00000000000068) rotate(0.0 0 0)" /></g><text x="-171.42857142857142" y="-1.0714285714280598" style="white-space:pre;" fill="#005400" font-family="DejaVu Sans" font-size="6.428571428571429" text-anchor="middle" dominant-baseline="baseline" xml:space="preserve" transform="rotate(-90 -171.42857142857142 5.115907697472721e-13)">M 2⌀20,span=184</text></g></svg>
  TextPositionType = 0
  WayPoints = (2) [(0,0,0),(50,0,0)]
  WayPointsType = 0
  X = 143.5
  Y = 100
FEATURE [TechDraw::DrawPage] TechDraw__DrawPage005  label="Column Drawing005"
  KeepUpdated = true
  NextBalloonIndex = 1
  ProjectionType = 0
  Template = -> Template005
  Views = -> [ReinforcementDrawingView005,ReinforcementDimensioning065,ReinforcementDimensioning066,ReinforcementDimensioning067,ReinforcementDimensioning068,ReinforcementDimensioning069,ReinforcementDimensioning070,ReinforcementDimensioning071,ReinforcementDimensioning072,ReinforcementDimensioning073,ReinforcementDimensioning074,ReinforcementDimensioning075,ReinforcementDimensioning076,+3 more]
